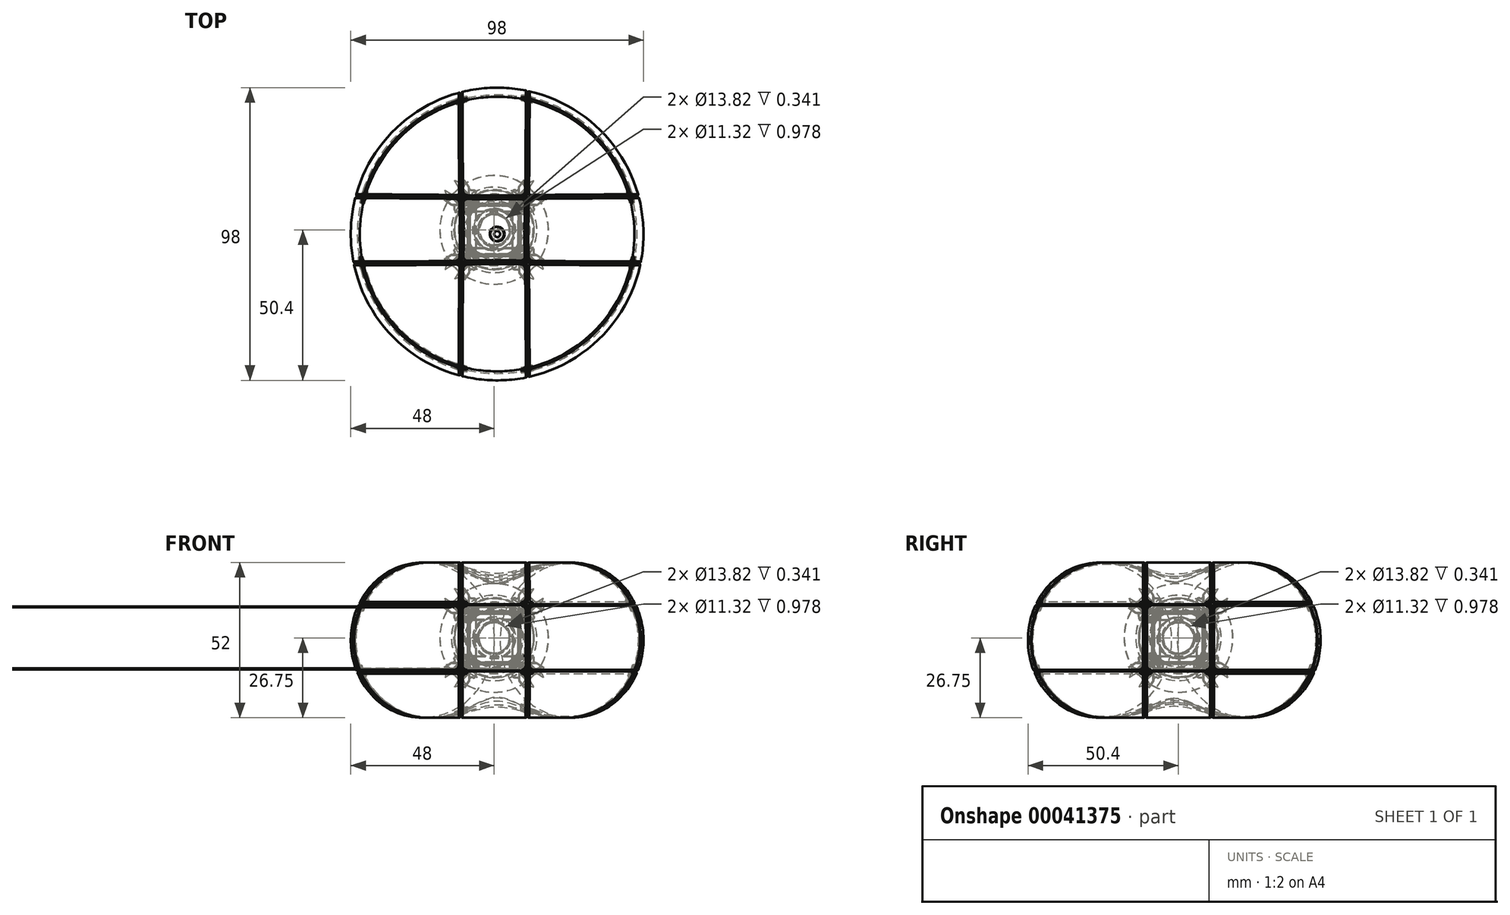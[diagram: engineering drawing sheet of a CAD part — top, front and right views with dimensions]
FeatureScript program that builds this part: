
annotation { "Feature Type Name" : "Feature", "Feature Type Description" : "" }
export const myFeature = defineFeature(function(context is Context, id is Id, definition is map)
    precondition{}
    {
        {
            var Q0;
            Q0=qCreatedBy(makeId("Front.planeOp"),FACE);
            cPlane(context, id + "F0", {"entities" : qUnion([Q0]), "cplaneType" : CPlaneType.OFFSET, "offset" : 1.4 * mm, "width" : 150 * mm, "height" : 150 * mm});
        }
        {
            var Q0;
            Q0=qCreatedBy(id+"F0.planeOp",FACE);
            var sketch = newSketch(context, id + "F1", { "sketchPlane" : qUnion([Q0])});
            skLineSegment(sketch, "E0", {"start": v(1, 6.41) * mm, "end": v(1, -8.32) * mm, "construction": true});
            skLineSegment(sketch, "E1", {"start": v(1, -0.75) * mm, "end": v(26, -0.75) * mm});
            skCircle(sketch, "E2", {"center": v(26, -0.75) * mm, "radius": 24 * mm});
            skEllipse(sketch, "E3", {"center": v(26, -0.75) * mm, "majorRadius": 26 * mm, "minorRadius": 24 * mm, "majorAxis": v(0, 1)});
            skSolve(sketch);
        }
        {
            var Q0;
            {var subQ0=sQuery(id+"F1.wireOp",EDGE,"E3");var subQ1=sQuery(id+"F1.wireOp",EDGE,"E2");var subQ3=makeQuery(id+"F1.imprint","INTERSECT",VERTEX,{"disambiguationData":[OD(0.0)],"derivedFrom":[subQ1,subQ0]});Q0=makeQuery(id+"F1.imprint","IMPRINT",FACE,{"disambiguationData":[TD([[makeQuery(id+"F1.imprint","IMPRINT",EDGE,{"disambiguationData":[TD([[subQ3,1.0]])],"derivedFrom":subQ1}),-1.0]])]});}
            var Q1;
            {var subQ0=sQuery(id+"F1.wireOp",EDGE,"E2");var subQ1=sQuery(id+"F1.wireOp",EDGE,"E3");var subQ3=makeQuery(id+"F1.imprint","INTERSECT",VERTEX,{"disambiguationData":[OD(0.0)],"derivedFrom":[subQ0,subQ1]});Q1=makeQuery(id+"F1.imprint","IMPRINT",FACE,{"disambiguationData":[TD([[makeQuery(id+"F1.imprint","IMPRINT",EDGE,{"disambiguationData":[TD([[subQ3,1.0]])],"derivedFrom":subQ0}),1.0]])]});}
            var Q2;
            {var subQ0=sQuery(id+"F1.wireOp",EDGE,"E3");var subQ1=sQuery(id+"F1.wireOp",EDGE,"E2");var subQ3=makeQuery(id+"F1.imprint","INTERSECT",VERTEX,{"disambiguationData":[OD(0.0)],"derivedFrom":[subQ1,subQ0]});Q2=makeQuery(id+"F1.imprint","IMPRINT",FACE,{"disambiguationData":[TD([[makeQuery(id+"F1.imprint","IMPRINT",EDGE,{"disambiguationData":[TD([[subQ3,-1.0]])],"derivedFrom":subQ1}),-1.0]])]});}
            var Q3;
            Q3=sQuery(id+"F1.wireOp",EDGE,"E0");
            revolve(context, id + "F2", {"entities" : qUnion([Q0, Q1, Q2]), "axis" : qUnion([Q3]), "revolveType" : RevolveType.FULL});
        }
        {
            var Q0;
            Q0=qCreatedBy(makeId("Front.planeOp"),FACE);
            var sketch = newSketch(context, id + "F3", { "sketchPlane" : qUnion([Q0])});
            skLineSegment(sketch, "E4", {"start": v(6, 60.75) * mm, "end": v(6.25, 60.75) * mm});
            skLineSegment(sketch, "E5.bottom", {"start": v(0, 0) * mm, "end": v(20, 0) * mm, "construction": true});
            skLineSegment(sketch, "E5.top", {"start": v(0, 20) * mm, "end": v(20, 20) * mm, "construction": true});
            skLineSegment(sketch, "E5.left", {"start": v(0, 0) * mm, "end": v(0, 20) * mm, "construction": true});
            skLineSegment(sketch, "E5.right", {"start": v(20, 0) * mm, "end": v(20, 20) * mm, "construction": true});
            skLineSegment(sketch, "E6", {"start": v(0, 0) * mm, "end": v(20, 20) * mm, "construction": true});
            skLineSegment(sketch, "E7.top", {"start": v(0, 28.28) * mm, "end": v(20, 28.28) * mm, "construction": true});
            skLineSegment(sketch, "E7.left", {"start": v(0, 0) * mm, "end": v(0, 28.28) * mm, "construction": true});
            skLineSegment(sketch, "E7.right", {"start": v(20, 0) * mm, "end": v(20, 28.28) * mm, "construction": true});
            skLineSegment(sketch, "E8", {"start": v(0, 0) * mm, "end": v(20, 28.28) * mm, "construction": true});
            skLineSegment(sketch, "E9.0", {"start": v(8.25, 14.07) * mm, "end": v(8.25, 14.34) * mm});
            skCircle(sketch, "E10", {"center": v(25, 0) * mm, "radius": 24 * mm, "construction": true});
            skEllipse(sketch, "E11", {"center": v(25, 0) * mm, "majorRadius": 25 * mm, "minorRadius": 24 * mm, "majorAxis": v(0, -1), "construction": true});
            skArc(sketch, "E12", {"start": v(7.21, 13.38) * mm, "mid": v(7.92, 13.44) * mm, "end": v(8.25, 14.07) * mm});
            skArc(sketch, "E13", {"start": v(7.21, 13.38) * mm, "mid": v(6.39, 13.3) * mm, "end": v(6, 12.57) * mm});
            skLineSegment(sketch, "E14", {"start": v(8.25, 14.07) * mm, "end": v(8.25, 14.07) * mm});
            skLineSegment(sketch, "E15", {"start": v(6, 11.54) * mm, "end": v(6, 12.57) * mm});
            skLineSegment(sketch, "E16.0", {"start": v(8.5, 14.07) * mm, "end": v(8.5, 14.26) * mm});
            skLineSegment(sketch, "E16.1", {"start": v(8.5, 14.07) * mm, "end": v(8.5, 14.07) * mm});
            skLineSegment(sketch, "E16.3", {"start": v(6.25, 12) * mm, "end": v(6.25, 12.57) * mm});
            skArc(sketch, "E16.4", {"start": v(7.12, 13.15) * mm, "mid": v(6.53, 13.09) * mm, "end": v(6.25, 12.57) * mm});
            skArc(sketch, "E16.5", {"start": v(7.12, 13.15) * mm, "mid": v(8.05, 13.24) * mm, "end": v(8.5, 14.07) * mm});
            skLineSegment(sketch, "E17", {"start": v(8.25, 14.34) * mm, "end": v(11, 18.23) * mm});
            skLineSegment(sketch, "E18", {"start": v(11, 18.23) * mm, "end": v(11, 58.23) * mm});
            skLineSegment(sketch, "E19.0", {"start": v(11.25, 18.15) * mm, "end": v(11.25, 58.23) * mm});
            skLineSegment(sketch, "E19.1", {"start": v(8.5, 14.26) * mm, "end": v(11.25, 18.15) * mm});
            skLineSegment(sketch, "E20", {"start": v(11, 58.23) * mm, "end": v(11.25, 58.23) * mm});
            skLineSegment(sketch, "E21", {"start": v(0, 8) * mm, "end": v(11.08, 8) * mm, "construction": true});
            skLineSegment(sketch, "E22", {"start": v(8, 6.66) * mm, "end": v(8.98, 6.66) * mm});
            skLineSegment(sketch, "E23", {"start": v(8.98, 5.66) * mm, "end": v(8, 5.66) * mm});
            skLineSegment(sketch, "E24.1", {"start": v(8.43, 6.9) * mm, "end": v(8.77, 6.9) * mm});
            skLineSegment(sketch, "E25", {"start": v(9.5, 6.67) * mm, "end": v(9.5, 5.65) * mm});
            skArc(sketch, "E26", {"start": v(8.98, 5.66) * mm, "mid": v(10.22, 6.16) * mm, "end": v(8.98, 6.66) * mm});
            skArc(sketch, "E27", {"start": v(8.77, 5.4) * mm, "mid": v(10.55, 6.16) * mm, "end": v(8.77, 6.9) * mm});
            skLineSegment(sketch, "E28.trimOffspring", {"start": v(8.77, 5.4) * mm, "end": v(8.25, 5.4) * mm});
            skLineSegment(sketch, "E29", {"start": v(9.5, 6.16) * mm, "end": v(8.75, 6.16) * mm});
            skLineSegment(sketch, "E30", {"start": v(8.77, 5.4) * mm, "end": v(8.77, 6.9) * mm, "construction": true});
            skLineSegment(sketch, "E31", {"start": v(8, 6.66) * mm, "end": v(8, 9.54) * mm});
            skLineSegment(sketch, "E32", {"start": v(8, 5.66) * mm, "end": v(8, 0) * mm});
            skLineSegment(sketch, "E33", {"start": v(8, 0) * mm, "end": v(8.25, 0) * mm});
            skLineSegment(sketch, "E34", {"start": v(8.25, 0) * mm, "end": v(8.25, 5.4) * mm});
            skLineSegment(sketch, "E35", {"start": v(6, 11.54) * mm, "end": v(8, 9.54) * mm});
            skLineSegment(sketch, "E36.0", {"start": v(6.25, 12) * mm, "end": v(8.43, 9.82) * mm});
            skLineSegment(sketch, "E37.trimOffspring", {"start": v(8.43, 9.82) * mm, "end": v(8.43, 6.9) * mm});
            skSolve(sketch);
        }
        {
            var Q0;
            Q0=makeQuery(id+"F3.imprint","IMPRINT",FACE,{"disambiguationData":[TD([[makeQuery(id+"F3.imprint","IMPRINT",EDGE,{"derivedFrom":sQuery(id+"F3.wireOp",EDGE,"E9.0")}),-1.0]])]});
            var Q1;
            Q1=sQuery(id+"F3.wireOp",EDGE,"E33");
            revolve(context, id + "F4", {"entities" : qUnion([Q0]), "axis" : qUnion([Q1]), "revolveType" : RevolveType.FULL, "oppositeDirection" : true});
        }
        {
            var Q0;
            Q0=makeQuery(id+"F4.opRevolve","SWEPT_BODY",BODY,{"disambiguationData":[OSD([sQuery(id+"F3.wireOp",EDGE,"e49f9d83-1361-4242-9c47-cf3f22957d33"),sQuery(id+"F3.wireOp",EDGE,"8730d663-9635-4a8c-ab1e-4514442db75a"),sQuery(id+"F3.wireOp",EDGE,"964f677f-81cd-4849-92fc-20bc6bd24689"),sQuery(id+"F3.wireOp",EDGE,"5875af96-867b-470c-aa94-be0c1ef376cd"),sQuery(id+"F3.wireOp",EDGE,"1ed69cf5-0fa4-4409-b8ec-72a7ec0a6539.trimOffspring"),sQuery(id+"F3.wireOp",EDGE,"80e836a5-1244-4908-9c79-18195465c5bf.0"),sQuery(id+"F3.wireOp",EDGE,"80e836a5-1244-4908-9c79-18195465c5bf.1"),sQuery(id+"F3.wireOp",EDGE,"80e836a5-1244-4908-9c79-18195465c5bf.2"),sQuery(id+"F3.wireOp",EDGE,"80e836a5-1244-4908-9c79-18195465c5bf.3"),sQuery(id+"F3.wireOp",EDGE,"80e836a5-1244-4908-9c79-18195465c5bf.4"),sQuery(id+"F3.wireOp",EDGE,"E4"),sQuery(id+"F3.wireOp",EDGE,"951da4eb-9f43-4ae5-b708-2bc6142b5415")])]});
            var Q1;
            Q1=makeQuery(id+"F4.opRevolve","SWEPT_BODY",BODY,{"disambiguationData":[OSD([sQuery(id+"F3.wireOp",EDGE,"E9.0"),sQuery(id+"F3.wireOp",EDGE,"E9.2"),sQuery(id+"F3.wireOp",EDGE,"E12"),sQuery(id+"F3.wireOp",EDGE,"E13"),sQuery(id+"F3.wireOp",EDGE,"E14"),sQuery(id+"F3.wireOp",EDGE,"E15"),sQuery(id+"F3.wireOp",EDGE,"E16.0"),sQuery(id+"F3.wireOp",EDGE,"E16.1"),sQuery(id+"F3.wireOp",EDGE,"E16.2"),sQuery(id+"F3.wireOp",EDGE,"E16.3"),sQuery(id+"F3.wireOp",EDGE,"E16.4"),sQuery(id+"F3.wireOp",EDGE,"E16.5"),sQuery(id+"F3.wireOp",EDGE,"49baa046-a65a-4210-b3a2-b618f89a0829"),sQuery(id+"F3.wireOp",EDGE,"98141963-c407-4e79-8dff-f83a4dca13c9")])]});
            var Q2;
            Q2=qCreatedBy(makeId("Right.planeOp"),FACE);
            mirror(context, id + "F5", {"entities" : qUnion([Q0, Q1]), "mirrorPlane" : qUnion([Q2])});
        }
        {
            var Q0;
            Q0=qCreatedBy(makeId("Right.planeOp"),FACE);
            var Q1;
            Q1=qCreatedBy(makeId("Front.planeOp"),FACE);
            cPlane(context, id + "F6", {"entities" : qUnion([Q0, Q1]), "cplaneType" : CPlaneType.MID_PLANE, "offset" : 150 * mm, "width" : 150 * mm, "height" : 150 * mm});
        }
        {
            var Q0;
            Q0=qCreatedBy(id+"F6.planeOp",FACE);
            var sketch = newSketch(context, id + "F7", { "sketchPlane" : qUnion([Q0])});
            skLineSegment(sketch, "E38.bottom", {"start": v(0, 0) * mm, "end": v(-70.71, 0) * mm, "construction": true});
            skLineSegment(sketch, "E38.top", {"start": v(0, 50) * mm, "end": v(-70.71, 50) * mm, "construction": true});
            skLineSegment(sketch, "E38.left", {"start": v(0, 0) * mm, "end": v(0, 50) * mm, "construction": true});
            skLineSegment(sketch, "E38.right", {"start": v(-70.71, 0) * mm, "end": v(-70.71, 50) * mm, "construction": true});
            skLineSegment(sketch, "E39", {"start": v(0, 0) * mm, "end": v(-70.71, 50) * mm});
            skSolve(sketch);
        }
        {
            var Q0;
            Q0=makeQuery(id+"F5.opPattern","COPY",BODY,{"derivedFrom":makeQuery(id+"F4.opRevolve","SWEPT_BODY",BODY,{"disambiguationData":[OSD([sQuery(id+"F3.wireOp",EDGE,"e49f9d83-1361-4242-9c47-cf3f22957d33"),sQuery(id+"F3.wireOp",EDGE,"8730d663-9635-4a8c-ab1e-4514442db75a"),sQuery(id+"F3.wireOp",EDGE,"964f677f-81cd-4849-92fc-20bc6bd24689"),sQuery(id+"F3.wireOp",EDGE,"5875af96-867b-470c-aa94-be0c1ef376cd"),sQuery(id+"F3.wireOp",EDGE,"1ed69cf5-0fa4-4409-b8ec-72a7ec0a6539.trimOffspring"),sQuery(id+"F3.wireOp",EDGE,"80e836a5-1244-4908-9c79-18195465c5bf.0"),sQuery(id+"F3.wireOp",EDGE,"80e836a5-1244-4908-9c79-18195465c5bf.1"),sQuery(id+"F3.wireOp",EDGE,"80e836a5-1244-4908-9c79-18195465c5bf.2"),sQuery(id+"F3.wireOp",EDGE,"80e836a5-1244-4908-9c79-18195465c5bf.3"),sQuery(id+"F3.wireOp",EDGE,"80e836a5-1244-4908-9c79-18195465c5bf.4"),sQuery(id+"F3.wireOp",EDGE,"E4"),sQuery(id+"F3.wireOp",EDGE,"951da4eb-9f43-4ae5-b708-2bc6142b5415")])]}),"instanceName":"1"});
            var Q1;
            Q1=makeQuery(id+"F4.opRevolve","SWEPT_BODY",BODY,{"disambiguationData":[OSD([sQuery(id+"F3.wireOp",EDGE,"e49f9d83-1361-4242-9c47-cf3f22957d33"),sQuery(id+"F3.wireOp",EDGE,"8730d663-9635-4a8c-ab1e-4514442db75a"),sQuery(id+"F3.wireOp",EDGE,"964f677f-81cd-4849-92fc-20bc6bd24689"),sQuery(id+"F3.wireOp",EDGE,"5875af96-867b-470c-aa94-be0c1ef376cd"),sQuery(id+"F3.wireOp",EDGE,"1ed69cf5-0fa4-4409-b8ec-72a7ec0a6539.trimOffspring"),sQuery(id+"F3.wireOp",EDGE,"80e836a5-1244-4908-9c79-18195465c5bf.0"),sQuery(id+"F3.wireOp",EDGE,"80e836a5-1244-4908-9c79-18195465c5bf.1"),sQuery(id+"F3.wireOp",EDGE,"80e836a5-1244-4908-9c79-18195465c5bf.2"),sQuery(id+"F3.wireOp",EDGE,"80e836a5-1244-4908-9c79-18195465c5bf.3"),sQuery(id+"F3.wireOp",EDGE,"80e836a5-1244-4908-9c79-18195465c5bf.4"),sQuery(id+"F3.wireOp",EDGE,"E4"),sQuery(id+"F3.wireOp",EDGE,"951da4eb-9f43-4ae5-b708-2bc6142b5415")])]});
            var Q2;
            Q2=makeQuery(id+"F5.opPattern","COPY",BODY,{"derivedFrom":makeQuery(id+"F4.opRevolve","SWEPT_BODY",BODY,{"disambiguationData":[OSD([sQuery(id+"F3.wireOp",EDGE,"E9.0"),sQuery(id+"F3.wireOp",EDGE,"E9.2"),sQuery(id+"F3.wireOp",EDGE,"E12"),sQuery(id+"F3.wireOp",EDGE,"E13"),sQuery(id+"F3.wireOp",EDGE,"E14"),sQuery(id+"F3.wireOp",EDGE,"E15"),sQuery(id+"F3.wireOp",EDGE,"E16.0"),sQuery(id+"F3.wireOp",EDGE,"E16.1"),sQuery(id+"F3.wireOp",EDGE,"E16.2"),sQuery(id+"F3.wireOp",EDGE,"E16.3"),sQuery(id+"F3.wireOp",EDGE,"E16.4"),sQuery(id+"F3.wireOp",EDGE,"E16.5"),sQuery(id+"F3.wireOp",EDGE,"49baa046-a65a-4210-b3a2-b618f89a0829"),sQuery(id+"F3.wireOp",EDGE,"98141963-c407-4e79-8dff-f83a4dca13c9")])]}),"instanceName":"1"});
            var Q3;
            Q3=makeQuery(id+"F4.opRevolve","SWEPT_BODY",BODY,{"disambiguationData":[OSD([sQuery(id+"F3.wireOp",EDGE,"E9.0"),sQuery(id+"F3.wireOp",EDGE,"E9.2"),sQuery(id+"F3.wireOp",EDGE,"E12"),sQuery(id+"F3.wireOp",EDGE,"E13"),sQuery(id+"F3.wireOp",EDGE,"E14"),sQuery(id+"F3.wireOp",EDGE,"E15"),sQuery(id+"F3.wireOp",EDGE,"E16.0"),sQuery(id+"F3.wireOp",EDGE,"E16.1"),sQuery(id+"F3.wireOp",EDGE,"E16.2"),sQuery(id+"F3.wireOp",EDGE,"E16.3"),sQuery(id+"F3.wireOp",EDGE,"E16.4"),sQuery(id+"F3.wireOp",EDGE,"E16.5"),sQuery(id+"F3.wireOp",EDGE,"49baa046-a65a-4210-b3a2-b618f89a0829"),sQuery(id+"F3.wireOp",EDGE,"98141963-c407-4e79-8dff-f83a4dca13c9")])]});
            var Q4;
            Q4=sQuery(id+"F7.wireOp",EDGE,"E39");
            circularPattern(context, id + "F8", {"entities" : qUnion([Q0, Q1, Q2, Q3]), "axis" : qUnion([Q4]), "angle" : 360 * degree, "instanceCount" : 3, "equalSpace" : true});
        }
        {
            var Q0;
            Q0=makeQuery(id+"F4.opRevolve","SWEPT_BODY",BODY,{"disambiguationData":[OSD([sQuery(id+"F3.wireOp",EDGE,"E9.0"),sQuery(id+"F3.wireOp",EDGE,"E9.2"),sQuery(id+"F3.wireOp",EDGE,"E12"),sQuery(id+"F3.wireOp",EDGE,"E13"),sQuery(id+"F3.wireOp",EDGE,"E14"),sQuery(id+"F3.wireOp",EDGE,"E15"),sQuery(id+"F3.wireOp",EDGE,"E16.0"),sQuery(id+"F3.wireOp",EDGE,"E16.1"),sQuery(id+"F3.wireOp",EDGE,"E16.2"),sQuery(id+"F3.wireOp",EDGE,"E16.3"),sQuery(id+"F3.wireOp",EDGE,"E16.4"),sQuery(id+"F3.wireOp",EDGE,"E16.5"),sQuery(id+"F3.wireOp",EDGE,"49baa046-a65a-4210-b3a2-b618f89a0829"),sQuery(id+"F3.wireOp",EDGE,"98141963-c407-4e79-8dff-f83a4dca13c9")])]});
            var Q1;
            Q1=makeQuery(id+"F5.opPattern","COPY",BODY,{"derivedFrom":makeQuery(id+"F4.opRevolve","SWEPT_BODY",BODY,{"disambiguationData":[OSD([sQuery(id+"F3.wireOp",EDGE,"E9.0"),sQuery(id+"F3.wireOp",EDGE,"E9.2"),sQuery(id+"F3.wireOp",EDGE,"E12"),sQuery(id+"F3.wireOp",EDGE,"E13"),sQuery(id+"F3.wireOp",EDGE,"E14"),sQuery(id+"F3.wireOp",EDGE,"E15"),sQuery(id+"F3.wireOp",EDGE,"E16.0"),sQuery(id+"F3.wireOp",EDGE,"E16.1"),sQuery(id+"F3.wireOp",EDGE,"E16.2"),sQuery(id+"F3.wireOp",EDGE,"E16.3"),sQuery(id+"F3.wireOp",EDGE,"E16.4"),sQuery(id+"F3.wireOp",EDGE,"E16.5"),sQuery(id+"F3.wireOp",EDGE,"49baa046-a65a-4210-b3a2-b618f89a0829"),sQuery(id+"F3.wireOp",EDGE,"98141963-c407-4e79-8dff-f83a4dca13c9")])]}),"instanceName":"1"});
            var Q2;
            Q2=makeQuery(id+"F8.opPattern","COPY",BODY,{"derivedFrom":makeQuery(id+"F4.opRevolve","SWEPT_BODY",BODY,{"disambiguationData":[OSD([sQuery(id+"F3.wireOp",EDGE,"E9.0"),sQuery(id+"F3.wireOp",EDGE,"E9.2"),sQuery(id+"F3.wireOp",EDGE,"E12"),sQuery(id+"F3.wireOp",EDGE,"E13"),sQuery(id+"F3.wireOp",EDGE,"E14"),sQuery(id+"F3.wireOp",EDGE,"E15"),sQuery(id+"F3.wireOp",EDGE,"E16.0"),sQuery(id+"F3.wireOp",EDGE,"E16.1"),sQuery(id+"F3.wireOp",EDGE,"E16.2"),sQuery(id+"F3.wireOp",EDGE,"E16.3"),sQuery(id+"F3.wireOp",EDGE,"E16.4"),sQuery(id+"F3.wireOp",EDGE,"E16.5"),sQuery(id+"F3.wireOp",EDGE,"49baa046-a65a-4210-b3a2-b618f89a0829"),sQuery(id+"F3.wireOp",EDGE,"98141963-c407-4e79-8dff-f83a4dca13c9")])]}),"instanceName":"2"});
            var Q3;
            Q3=makeQuery(id+"F8.opPattern","COPY",BODY,{"derivedFrom":makeQuery(id+"F5.opPattern","COPY",BODY,{"derivedFrom":makeQuery(id+"F4.opRevolve","SWEPT_BODY",BODY,{"disambiguationData":[OSD([sQuery(id+"F3.wireOp",EDGE,"E9.0"),sQuery(id+"F3.wireOp",EDGE,"E9.2"),sQuery(id+"F3.wireOp",EDGE,"E12"),sQuery(id+"F3.wireOp",EDGE,"E13"),sQuery(id+"F3.wireOp",EDGE,"E14"),sQuery(id+"F3.wireOp",EDGE,"E15"),sQuery(id+"F3.wireOp",EDGE,"E16.0"),sQuery(id+"F3.wireOp",EDGE,"E16.1"),sQuery(id+"F3.wireOp",EDGE,"E16.2"),sQuery(id+"F3.wireOp",EDGE,"E16.3"),sQuery(id+"F3.wireOp",EDGE,"E16.4"),sQuery(id+"F3.wireOp",EDGE,"E16.5"),sQuery(id+"F3.wireOp",EDGE,"49baa046-a65a-4210-b3a2-b618f89a0829"),sQuery(id+"F3.wireOp",EDGE,"98141963-c407-4e79-8dff-f83a4dca13c9")])]}),"instanceName":"1"}),"instanceName":"2"});
            var Q4;
            Q4=makeQuery(id+"F8.opPattern","COPY",BODY,{"derivedFrom":makeQuery(id+"F4.opRevolve","SWEPT_BODY",BODY,{"disambiguationData":[OSD([sQuery(id+"F3.wireOp",EDGE,"E9.0"),sQuery(id+"F3.wireOp",EDGE,"E9.2"),sQuery(id+"F3.wireOp",EDGE,"E12"),sQuery(id+"F3.wireOp",EDGE,"E13"),sQuery(id+"F3.wireOp",EDGE,"E14"),sQuery(id+"F3.wireOp",EDGE,"E15"),sQuery(id+"F3.wireOp",EDGE,"E16.0"),sQuery(id+"F3.wireOp",EDGE,"E16.1"),sQuery(id+"F3.wireOp",EDGE,"E16.2"),sQuery(id+"F3.wireOp",EDGE,"E16.3"),sQuery(id+"F3.wireOp",EDGE,"E16.4"),sQuery(id+"F3.wireOp",EDGE,"E16.5"),sQuery(id+"F3.wireOp",EDGE,"49baa046-a65a-4210-b3a2-b618f89a0829"),sQuery(id+"F3.wireOp",EDGE,"98141963-c407-4e79-8dff-f83a4dca13c9")])]}),"instanceName":"1"});
            var Q5;
            Q5=makeQuery(id+"F8.opPattern","COPY",BODY,{"derivedFrom":makeQuery(id+"F5.opPattern","COPY",BODY,{"derivedFrom":makeQuery(id+"F4.opRevolve","SWEPT_BODY",BODY,{"disambiguationData":[OSD([sQuery(id+"F3.wireOp",EDGE,"E9.0"),sQuery(id+"F3.wireOp",EDGE,"E9.2"),sQuery(id+"F3.wireOp",EDGE,"E12"),sQuery(id+"F3.wireOp",EDGE,"E13"),sQuery(id+"F3.wireOp",EDGE,"E14"),sQuery(id+"F3.wireOp",EDGE,"E15"),sQuery(id+"F3.wireOp",EDGE,"E16.0"),sQuery(id+"F3.wireOp",EDGE,"E16.1"),sQuery(id+"F3.wireOp",EDGE,"E16.2"),sQuery(id+"F3.wireOp",EDGE,"E16.3"),sQuery(id+"F3.wireOp",EDGE,"E16.4"),sQuery(id+"F3.wireOp",EDGE,"E16.5"),sQuery(id+"F3.wireOp",EDGE,"49baa046-a65a-4210-b3a2-b618f89a0829"),sQuery(id+"F3.wireOp",EDGE,"98141963-c407-4e79-8dff-f83a4dca13c9")])]}),"instanceName":"1"}),"instanceName":"1"});
            booleanBodies(context, id + "F9", {"operationType" : BooleanOperationType.UNION, "tools" : qUnion([Q0, Q1, Q2, Q3, Q4, Q5])});
        }
        {
            var Q0;
            Q0=makeQuery(id+"F4.opRevolve","SWEPT_BODY",BODY,{"disambiguationData":[OSD([sQuery(id+"F3.wireOp",EDGE,"E9.0"),sQuery(id+"F3.wireOp",EDGE,"E9.2"),sQuery(id+"F3.wireOp",EDGE,"E12"),sQuery(id+"F3.wireOp",EDGE,"E13"),sQuery(id+"F3.wireOp",EDGE,"E14"),sQuery(id+"F3.wireOp",EDGE,"E15"),sQuery(id+"F3.wireOp",EDGE,"E16.0"),sQuery(id+"F3.wireOp",EDGE,"E16.1"),sQuery(id+"F3.wireOp",EDGE,"E16.2"),sQuery(id+"F3.wireOp",EDGE,"E16.3"),sQuery(id+"F3.wireOp",EDGE,"E16.4"),sQuery(id+"F3.wireOp",EDGE,"E16.5"),sQuery(id+"F3.wireOp",EDGE,"49baa046-a65a-4210-b3a2-b618f89a0829"),sQuery(id+"F3.wireOp",EDGE,"98141963-c407-4e79-8dff-f83a4dca13c9")])]});
            var Q1;
            Q1=makeQuery(id+"F2.opRevolve","SWEPT_BODY",BODY,{"disambiguationData":[OSD([sQuery(id+"F1.wireOp",EDGE,"E2")])]});
            var Q2;
            Q2=makeQuery(id+"F2.opRevolve","SWEPT_BODY",BODY,{"disambiguationData":[OSD([sQuery(id+"F1.wireOp",EDGE,"E3")])]});
            booleanBodies(context, id + "F10", {"operationType" : BooleanOperationType.SUBTRACTION, "tools" : qUnion([Q0]), "targets" : qUnion([Q1, Q2])});
        }
        {
            var Q0;
            {var subQ0=makeQuery(id+"F4.opRevolve","SWEPT_FACE",FACE,{"disambiguationData":[OSD([sQuery(id+"F3.wireOp",EDGE,"E18")])]});Q0=makeQuery(id+"F10.opBoolean","COPY",EDGE,{"derivedFrom":makeQuery(id+"F9.opBoolean","INTERSECT",EDGE,{"disambiguationData":[OD(0.0)],"derivedFrom":[subQ0,makeQuery(id+"F8.opPattern","COPY",FACE,{"derivedFrom":subQ0,"instanceName":"2"})]})});}
            var Q1;
            {var subQ0=makeQuery(id+"F4.opRevolve","SWEPT_FACE",FACE,{"disambiguationData":[OSD([sQuery(id+"F3.wireOp",EDGE,"E18")])]});Q1=makeQuery(id+"F10.opBoolean","COPY",EDGE,{"derivedFrom":makeQuery(id+"F9.opBoolean","INTERSECT",EDGE,{"disambiguationData":[OD(0.0)],"derivedFrom":[makeQuery(id+"F5.opPattern","COPY",FACE,{"derivedFrom":subQ0,"instanceName":"1"}),makeQuery(id+"F8.opPattern","COPY",FACE,{"derivedFrom":subQ0,"instanceName":"2"})]})});}
            var Q2;
            {var subQ0=makeQuery(id+"F4.opRevolve","SWEPT_FACE",FACE,{"disambiguationData":[OSD([sQuery(id+"F3.wireOp",EDGE,"E18")])]});Q2=makeQuery(id+"F10.opBoolean","COPY",EDGE,{"derivedFrom":makeQuery(id+"F9.opBoolean","INTERSECT",EDGE,{"disambiguationData":[OD(0.0)],"derivedFrom":[subQ0,makeQuery(id+"F8.opPattern","COPY",FACE,{"derivedFrom":makeQuery(id+"F5.opPattern","COPY",FACE,{"derivedFrom":subQ0,"instanceName":"1"}),"instanceName":"2"})]})});}
            var Q3;
            {var subQ0=makeQuery(id+"F5.opPattern","COPY",FACE,{"derivedFrom":makeQuery(id+"F4.opRevolve","SWEPT_FACE",FACE,{"disambiguationData":[OSD([sQuery(id+"F3.wireOp",EDGE,"E18")])]}),"instanceName":"1"});Q3=makeQuery(id+"F10.opBoolean","COPY",EDGE,{"derivedFrom":makeQuery(id+"F9.opBoolean","INTERSECT",EDGE,{"disambiguationData":[OD(0.0)],"derivedFrom":[subQ0,makeQuery(id+"F8.opPattern","COPY",FACE,{"derivedFrom":subQ0,"instanceName":"2"})]})});}
            var Q4;
            {var subQ0=makeQuery(id+"F4.opRevolve","SWEPT_FACE",FACE,{"disambiguationData":[OSD([sQuery(id+"F3.wireOp",EDGE,"E18")])]});Q4=makeQuery(id+"F10.opBoolean","COPY",EDGE,{"derivedFrom":makeQuery(id+"F9.opBoolean","INTERSECT",EDGE,{"disambiguationData":[OD(1.0)],"derivedFrom":[makeQuery(id+"F8.opPattern","COPY",FACE,{"derivedFrom":makeQuery(id+"F5.opPattern","COPY",FACE,{"derivedFrom":subQ0,"instanceName":"1"}),"instanceName":"1"}),makeQuery(id+"F8.opPattern","COPY",FACE,{"derivedFrom":subQ0,"instanceName":"2"})]})});}
            var Q5;
            {var subQ0=makeQuery(id+"F4.opRevolve","SWEPT_FACE",FACE,{"disambiguationData":[OSD([sQuery(id+"F3.wireOp",EDGE,"E18")])]});Q5=makeQuery(id+"F10.opBoolean","COPY",EDGE,{"derivedFrom":makeQuery(id+"F9.opBoolean","INTERSECT",EDGE,{"disambiguationData":[OD(1.0)],"derivedFrom":[makeQuery(id+"F8.opPattern","COPY",FACE,{"derivedFrom":subQ0,"instanceName":"1"}),makeQuery(id+"F8.opPattern","COPY",FACE,{"derivedFrom":subQ0,"instanceName":"2"})]})});}
            var Q6;
            {var subQ0=makeQuery(id+"F4.opRevolve","SWEPT_FACE",FACE,{"disambiguationData":[OSD([sQuery(id+"F3.wireOp",EDGE,"E18")])]});Q6=makeQuery(id+"F10.opBoolean","COPY",EDGE,{"derivedFrom":makeQuery(id+"F9.opBoolean","INTERSECT",EDGE,{"disambiguationData":[OD(1.0)],"derivedFrom":[makeQuery(id+"F8.opPattern","COPY",FACE,{"derivedFrom":subQ0,"instanceName":"1"}),makeQuery(id+"F8.opPattern","COPY",FACE,{"derivedFrom":makeQuery(id+"F5.opPattern","COPY",FACE,{"derivedFrom":subQ0,"instanceName":"1"}),"instanceName":"2"})]})});}
            var Q7;
            {var subQ0=makeQuery(id+"F5.opPattern","COPY",FACE,{"derivedFrom":makeQuery(id+"F4.opRevolve","SWEPT_FACE",FACE,{"disambiguationData":[OSD([sQuery(id+"F3.wireOp",EDGE,"E18")])]}),"instanceName":"1"});Q7=makeQuery(id+"F10.opBoolean","COPY",EDGE,{"derivedFrom":makeQuery(id+"F9.opBoolean","INTERSECT",EDGE,{"disambiguationData":[OD(1.0)],"derivedFrom":[makeQuery(id+"F8.opPattern","COPY",FACE,{"derivedFrom":subQ0,"instanceName":"1"}),makeQuery(id+"F8.opPattern","COPY",FACE,{"derivedFrom":subQ0,"instanceName":"2"})]})});}
            var Q8;
            {var subQ0=makeQuery(id+"F4.opRevolve","SWEPT_FACE",FACE,{"disambiguationData":[OSD([sQuery(id+"F3.wireOp",EDGE,"E18")])]});Q8=makeQuery(id+"F10.opBoolean","COPY",EDGE,{"derivedFrom":makeQuery(id+"F9.opBoolean","INTERSECT",EDGE,{"disambiguationData":[OD(1.0)],"derivedFrom":[subQ0,makeQuery(id+"F8.opPattern","COPY",FACE,{"derivedFrom":makeQuery(id+"F5.opPattern","COPY",FACE,{"derivedFrom":subQ0,"instanceName":"1"}),"instanceName":"1"})]})});}
            var Q9;
            {var subQ0=makeQuery(id+"F5.opPattern","COPY",FACE,{"derivedFrom":makeQuery(id+"F4.opRevolve","SWEPT_FACE",FACE,{"disambiguationData":[OSD([sQuery(id+"F3.wireOp",EDGE,"E18")])]}),"instanceName":"1"});Q9=makeQuery(id+"F10.opBoolean","COPY",EDGE,{"derivedFrom":makeQuery(id+"F9.opBoolean","INTERSECT",EDGE,{"disambiguationData":[OD(1.0)],"derivedFrom":[subQ0,makeQuery(id+"F8.opPattern","COPY",FACE,{"derivedFrom":subQ0,"instanceName":"1"})]})});}
            var Q10;
            {var subQ0=makeQuery(id+"F4.opRevolve","SWEPT_FACE",FACE,{"disambiguationData":[OSD([sQuery(id+"F3.wireOp",EDGE,"E18")])]});Q10=makeQuery(id+"F10.opBoolean","COPY",EDGE,{"derivedFrom":makeQuery(id+"F9.opBoolean","INTERSECT",EDGE,{"disambiguationData":[OD(1.0)],"derivedFrom":[subQ0,makeQuery(id+"F8.opPattern","COPY",FACE,{"derivedFrom":subQ0,"instanceName":"1"})]})});}
            var Q11;
            {var subQ0=makeQuery(id+"F4.opRevolve","SWEPT_FACE",FACE,{"disambiguationData":[OSD([sQuery(id+"F3.wireOp",EDGE,"E18")])]});Q11=makeQuery(id+"F10.opBoolean","COPY",EDGE,{"derivedFrom":makeQuery(id+"F9.opBoolean","INTERSECT",EDGE,{"disambiguationData":[OD(1.0)],"derivedFrom":[makeQuery(id+"F5.opPattern","COPY",FACE,{"derivedFrom":subQ0,"instanceName":"1"}),makeQuery(id+"F8.opPattern","COPY",FACE,{"derivedFrom":subQ0,"instanceName":"1"})]})});}
            var Q12;
            {var subQ0=makeQuery(id+"F4.opRevolve","SWEPT_FACE",FACE,{"disambiguationData":[OSD([sQuery(id+"F3.wireOp",EDGE,"E18")])]});Q12=makeQuery(id+"F10.opBoolean","COPY",EDGE,{"derivedFrom":makeQuery(id+"F9.opBoolean","INTERSECT",EDGE,{"disambiguationData":[OD(1.0)],"derivedFrom":[subQ0,makeQuery(id+"F8.opPattern","COPY",FACE,{"derivedFrom":subQ0,"instanceName":"2"})]})});}
            var Q13;
            {var subQ0=makeQuery(id+"F4.opRevolve","SWEPT_FACE",FACE,{"disambiguationData":[OSD([sQuery(id+"F3.wireOp",EDGE,"E18")])]});Q13=makeQuery(id+"F10.opBoolean","COPY",EDGE,{"derivedFrom":makeQuery(id+"F9.opBoolean","INTERSECT",EDGE,{"disambiguationData":[OD(1.0)],"derivedFrom":[subQ0,makeQuery(id+"F8.opPattern","COPY",FACE,{"derivedFrom":makeQuery(id+"F5.opPattern","COPY",FACE,{"derivedFrom":subQ0,"instanceName":"1"}),"instanceName":"2"})]})});}
            var Q14;
            {var subQ0=makeQuery(id+"F4.opRevolve","SWEPT_FACE",FACE,{"disambiguationData":[OSD([sQuery(id+"F3.wireOp",EDGE,"E18")])]});Q14=makeQuery(id+"F10.opBoolean","COPY",EDGE,{"derivedFrom":makeQuery(id+"F9.opBoolean","INTERSECT",EDGE,{"disambiguationData":[OD(1.0)],"derivedFrom":[makeQuery(id+"F5.opPattern","COPY",FACE,{"derivedFrom":subQ0,"instanceName":"1"}),makeQuery(id+"F8.opPattern","COPY",FACE,{"derivedFrom":subQ0,"instanceName":"2"})]})});}
            var Q15;
            {var subQ0=makeQuery(id+"F5.opPattern","COPY",FACE,{"derivedFrom":makeQuery(id+"F4.opRevolve","SWEPT_FACE",FACE,{"disambiguationData":[OSD([sQuery(id+"F3.wireOp",EDGE,"E18")])]}),"instanceName":"1"});Q15=makeQuery(id+"F10.opBoolean","COPY",EDGE,{"derivedFrom":makeQuery(id+"F9.opBoolean","INTERSECT",EDGE,{"disambiguationData":[OD(1.0)],"derivedFrom":[subQ0,makeQuery(id+"F8.opPattern","COPY",FACE,{"derivedFrom":subQ0,"instanceName":"2"})]})});}
            var Q16;
            {var subQ0=makeQuery(id+"F5.opPattern","COPY",FACE,{"derivedFrom":makeQuery(id+"F4.opRevolve","SWEPT_FACE",FACE,{"disambiguationData":[OSD([sQuery(id+"F3.wireOp",EDGE,"E18")])]}),"instanceName":"1"});Q16=makeQuery(id+"F10.opBoolean","COPY",EDGE,{"derivedFrom":makeQuery(id+"F9.opBoolean","INTERSECT",EDGE,{"disambiguationData":[OD(0.0)],"derivedFrom":[subQ0,makeQuery(id+"F8.opPattern","COPY",FACE,{"derivedFrom":subQ0,"instanceName":"1"})]})});}
            var Q17;
            {var subQ0=makeQuery(id+"F4.opRevolve","SWEPT_FACE",FACE,{"disambiguationData":[OSD([sQuery(id+"F3.wireOp",EDGE,"E18")])]});Q17=makeQuery(id+"F10.opBoolean","COPY",EDGE,{"derivedFrom":makeQuery(id+"F9.opBoolean","INTERSECT",EDGE,{"disambiguationData":[OD(0.0)],"derivedFrom":[subQ0,makeQuery(id+"F8.opPattern","COPY",FACE,{"derivedFrom":makeQuery(id+"F5.opPattern","COPY",FACE,{"derivedFrom":subQ0,"instanceName":"1"}),"instanceName":"1"})]})});}
            var Q18;
            {var subQ0=makeQuery(id+"F4.opRevolve","SWEPT_FACE",FACE,{"disambiguationData":[OSD([sQuery(id+"F3.wireOp",EDGE,"E18")])]});Q18=makeQuery(id+"F10.opBoolean","COPY",EDGE,{"derivedFrom":makeQuery(id+"F9.opBoolean","INTERSECT",EDGE,{"disambiguationData":[OD(0.0)],"derivedFrom":[makeQuery(id+"F5.opPattern","COPY",FACE,{"derivedFrom":subQ0,"instanceName":"1"}),makeQuery(id+"F8.opPattern","COPY",FACE,{"derivedFrom":subQ0,"instanceName":"1"})]})});}
            var Q19;
            {var subQ0=makeQuery(id+"F4.opRevolve","SWEPT_FACE",FACE,{"disambiguationData":[OSD([sQuery(id+"F3.wireOp",EDGE,"E18")])]});Q19=makeQuery(id+"F10.opBoolean","COPY",EDGE,{"derivedFrom":makeQuery(id+"F9.opBoolean","INTERSECT",EDGE,{"disambiguationData":[OD(0.0)],"derivedFrom":[subQ0,makeQuery(id+"F8.opPattern","COPY",FACE,{"derivedFrom":subQ0,"instanceName":"1"})]})});}
            var Q20;
            {var subQ0=makeQuery(id+"F4.opRevolve","SWEPT_FACE",FACE,{"disambiguationData":[OSD([sQuery(id+"F3.wireOp",EDGE,"E18")])]});Q20=makeQuery(id+"F10.opBoolean","COPY",EDGE,{"derivedFrom":makeQuery(id+"F9.opBoolean","INTERSECT",EDGE,{"disambiguationData":[OD(0.0)],"derivedFrom":[makeQuery(id+"F8.opPattern","COPY",FACE,{"derivedFrom":subQ0,"instanceName":"1"}),makeQuery(id+"F8.opPattern","COPY",FACE,{"derivedFrom":subQ0,"instanceName":"2"})]})});}
            var Q21;
            {var subQ0=makeQuery(id+"F4.opRevolve","SWEPT_FACE",FACE,{"disambiguationData":[OSD([sQuery(id+"F3.wireOp",EDGE,"E18")])]});Q21=makeQuery(id+"F10.opBoolean","COPY",EDGE,{"derivedFrom":makeQuery(id+"F9.opBoolean","INTERSECT",EDGE,{"disambiguationData":[OD(0.0)],"derivedFrom":[makeQuery(id+"F8.opPattern","COPY",FACE,{"derivedFrom":subQ0,"instanceName":"1"}),makeQuery(id+"F8.opPattern","COPY",FACE,{"derivedFrom":makeQuery(id+"F5.opPattern","COPY",FACE,{"derivedFrom":subQ0,"instanceName":"1"}),"instanceName":"2"})]})});}
            var Q22;
            {var subQ0=makeQuery(id+"F4.opRevolve","SWEPT_FACE",FACE,{"disambiguationData":[OSD([sQuery(id+"F3.wireOp",EDGE,"E18")])]});Q22=makeQuery(id+"F10.opBoolean","COPY",EDGE,{"derivedFrom":makeQuery(id+"F9.opBoolean","INTERSECT",EDGE,{"disambiguationData":[OD(0.0)],"derivedFrom":[makeQuery(id+"F8.opPattern","COPY",FACE,{"derivedFrom":makeQuery(id+"F5.opPattern","COPY",FACE,{"derivedFrom":subQ0,"instanceName":"1"}),"instanceName":"1"}),makeQuery(id+"F8.opPattern","COPY",FACE,{"derivedFrom":subQ0,"instanceName":"2"})]})});}
            var Q23;
            {var subQ0=makeQuery(id+"F5.opPattern","COPY",FACE,{"derivedFrom":makeQuery(id+"F4.opRevolve","SWEPT_FACE",FACE,{"disambiguationData":[OSD([sQuery(id+"F3.wireOp",EDGE,"E18")])]}),"instanceName":"1"});Q23=makeQuery(id+"F10.opBoolean","COPY",EDGE,{"derivedFrom":makeQuery(id+"F9.opBoolean","INTERSECT",EDGE,{"disambiguationData":[OD(0.0)],"derivedFrom":[makeQuery(id+"F8.opPattern","COPY",FACE,{"derivedFrom":subQ0,"instanceName":"1"}),makeQuery(id+"F8.opPattern","COPY",FACE,{"derivedFrom":subQ0,"instanceName":"2"})]})});}
            fillet(context, id + "F11", {"entities" : qUnion([Q0, Q1, Q2, Q3, Q4, Q5, Q6, Q7, Q8, Q9, Q10, Q11, Q12, Q13, Q14, Q15, Q16, Q17, Q18, Q19, Q20, Q21, Q22, Q23]), "radius" : 2 * mm, "tangentPropagation" : true, "allowEdgeOverflow" : false});
        }
        {
            var Q0;
            {var subQ0=makeQuery(id+"F4.opRevolve","SWEPT_FACE",FACE,{"disambiguationData":[OSD([sQuery(id+"F3.wireOp",EDGE,"E18")])]});var subQ1=makeQuery(id+"F5.opPattern","COPY",FACE,{"derivedFrom":subQ0,"instanceName":"1"});var subQ2=makeQuery(id+"F4.opRevolve","SWEPT_FACE",FACE,{"disambiguationData":[OSD([sQuery(id+"F3.wireOp",EDGE,"E20")])]});var subQ3=makeQuery(id+"F5.opPattern","COPY",FACE,{"derivedFrom":subQ2,"instanceName":"1"});var subQ4=makeQuery(id+"F4.opRevolve","SWEPT_FACE",FACE,{"disambiguationData":[OSD([sQuery(id+"F3.wireOp",EDGE,"E17")])]});var subQ5=makeQuery(id+"F5.opPattern","COPY",FACE,{"derivedFrom":subQ4,"instanceName":"1"});Q0=makeQuery(id+"F10.opBoolean","INTERSECT",EDGE,{"derivedFrom":[makeQuery(id+"F2.opRevolve","SWEPT_FACE",FACE,{"disambiguationData":[OSD([sQuery(id+"F1.wireOp",EDGE,"E3")])]}),makeQuery(id+"F9.opBoolean","SPLIT",FACE,{"disambiguationData":[TD([makeQuery(id+"F8.opPattern","COPY",FACE,{"derivedFrom":subQ5,"instanceName":"1"}),makeQuery(id+"F8.opPattern","COPY",FACE,{"derivedFrom":subQ3,"instanceName":"1"}),makeQuery(id+"F8.opPattern","COPY",FACE,{"derivedFrom":subQ4,"instanceName":"2"}),makeQuery(id+"F8.opPattern","COPY",FACE,{"derivedFrom":subQ0,"instanceName":"2"}),makeQuery(id+"F8.opPattern","COPY",FACE,{"derivedFrom":subQ2,"instanceName":"2"}),makeQuery(id+"F8.opPattern","COPY",FACE,{"derivedFrom":subQ5,"instanceName":"2"}),makeQuery(id+"F8.opPattern","COPY",FACE,{"derivedFrom":subQ1,"instanceName":"2"}),makeQuery(id+"F8.opPattern","COPY",FACE,{"derivedFrom":subQ3,"instanceName":"2"})]),OD(1.0)],"derivedFrom":makeQuery(id+"F8.opPattern","COPY",FACE,{"derivedFrom":subQ1,"instanceName":"1"})})]});}
            var Q1;
            {var subQ0=makeQuery(id+"F4.opRevolve","SWEPT_FACE",FACE,{"disambiguationData":[OSD([sQuery(id+"F3.wireOp",EDGE,"E18")])]});var subQ1=makeQuery(id+"F5.opPattern","COPY",FACE,{"derivedFrom":subQ0,"instanceName":"1"});var subQ2=makeQuery(id+"F4.opRevolve","SWEPT_FACE",FACE,{"disambiguationData":[OSD([sQuery(id+"F3.wireOp",EDGE,"E20")])]});var subQ3=makeQuery(id+"F5.opPattern","COPY",FACE,{"derivedFrom":subQ2,"instanceName":"1"});var subQ4=makeQuery(id+"F4.opRevolve","SWEPT_FACE",FACE,{"disambiguationData":[OSD([sQuery(id+"F3.wireOp",EDGE,"E17")])]});var subQ5=makeQuery(id+"F5.opPattern","COPY",FACE,{"derivedFrom":subQ4,"instanceName":"1"});Q1=makeQuery(id+"F10.opBoolean","INTERSECT",EDGE,{"derivedFrom":[makeQuery(id+"F2.opRevolve","SWEPT_FACE",FACE,{"disambiguationData":[OSD([sQuery(id+"F1.wireOp",EDGE,"E3")])]}),makeQuery(id+"F9.opBoolean","SPLIT",FACE,{"disambiguationData":[TD([subQ4,subQ0,subQ2,subQ5,subQ1,subQ3,makeQuery(id+"F8.opPattern","COPY",FACE,{"derivedFrom":subQ5,"instanceName":"2"}),makeQuery(id+"F8.opPattern","COPY",FACE,{"derivedFrom":subQ3,"instanceName":"2"})]),OD(1.0)],"derivedFrom":makeQuery(id+"F8.opPattern","COPY",FACE,{"derivedFrom":subQ1,"instanceName":"2"})})]});}
            var Q2;
            {var subQ0=makeQuery(id+"F4.opRevolve","SWEPT_FACE",FACE,{"disambiguationData":[OSD([sQuery(id+"F3.wireOp",EDGE,"E18")])]});var subQ1=makeQuery(id+"F5.opPattern","COPY",FACE,{"derivedFrom":subQ0,"instanceName":"1"});var subQ2=makeQuery(id+"F4.opRevolve","SWEPT_FACE",FACE,{"disambiguationData":[OSD([sQuery(id+"F3.wireOp",EDGE,"E20")])]});var subQ3=makeQuery(id+"F5.opPattern","COPY",FACE,{"derivedFrom":subQ2,"instanceName":"1"});var subQ4=makeQuery(id+"F4.opRevolve","SWEPT_FACE",FACE,{"disambiguationData":[OSD([sQuery(id+"F3.wireOp",EDGE,"E17")])]});var subQ5=makeQuery(id+"F5.opPattern","COPY",FACE,{"derivedFrom":subQ4,"instanceName":"1"});Q2=makeQuery(id+"F10.opBoolean","INTERSECT",EDGE,{"derivedFrom":[makeQuery(id+"F2.opRevolve","SWEPT_FACE",FACE,{"disambiguationData":[OSD([sQuery(id+"F1.wireOp",EDGE,"E3")])]}),makeQuery(id+"F9.opBoolean","SPLIT",FACE,{"disambiguationData":[TD([subQ4,subQ0,subQ2,subQ5,subQ1,subQ3,makeQuery(id+"F8.opPattern","COPY",FACE,{"derivedFrom":subQ5,"instanceName":"1"}),makeQuery(id+"F8.opPattern","COPY",FACE,{"derivedFrom":subQ3,"instanceName":"1"})]),OD(1.0)],"derivedFrom":makeQuery(id+"F8.opPattern","COPY",FACE,{"derivedFrom":subQ1,"instanceName":"1"})})]});}
            var Q3;
            {var subQ0=makeQuery(id+"F4.opRevolve","SWEPT_FACE",FACE,{"disambiguationData":[OSD([sQuery(id+"F3.wireOp",EDGE,"E18")])]});var subQ1=makeQuery(id+"F5.opPattern","COPY",FACE,{"derivedFrom":subQ0,"instanceName":"1"});var subQ2=makeQuery(id+"F4.opRevolve","SWEPT_FACE",FACE,{"disambiguationData":[OSD([sQuery(id+"F3.wireOp",EDGE,"E20")])]});var subQ3=makeQuery(id+"F5.opPattern","COPY",FACE,{"derivedFrom":subQ2,"instanceName":"1"});var subQ4=makeQuery(id+"F4.opRevolve","SWEPT_FACE",FACE,{"disambiguationData":[OSD([sQuery(id+"F3.wireOp",EDGE,"E17")])]});var subQ5=makeQuery(id+"F5.opPattern","COPY",FACE,{"derivedFrom":subQ4,"instanceName":"1"});Q3=makeQuery(id+"F10.opBoolean","INTERSECT",EDGE,{"derivedFrom":[makeQuery(id+"F2.opRevolve","SWEPT_FACE",FACE,{"disambiguationData":[OSD([sQuery(id+"F1.wireOp",EDGE,"E3")])]}),makeQuery(id+"F9.opBoolean","SPLIT",FACE,{"disambiguationData":[TD([subQ4,subQ0,subQ2,subQ5,subQ1,subQ3,makeQuery(id+"F8.opPattern","COPY",FACE,{"derivedFrom":subQ5,"instanceName":"1"}),makeQuery(id+"F8.opPattern","COPY",FACE,{"derivedFrom":subQ3,"instanceName":"1"})]),OD(1.0)],"derivedFrom":makeQuery(id+"F8.opPattern","COPY",FACE,{"derivedFrom":subQ1,"instanceName":"1"})})]});}
            var Q4;
            {var subQ0=makeQuery(id+"F4.opRevolve","SWEPT_FACE",FACE,{"disambiguationData":[OSD([sQuery(id+"F3.wireOp",EDGE,"E18")])]});var subQ1=makeQuery(id+"F5.opPattern","COPY",FACE,{"derivedFrom":subQ0,"instanceName":"1"});var subQ2=makeQuery(id+"F4.opRevolve","SWEPT_FACE",FACE,{"disambiguationData":[OSD([sQuery(id+"F3.wireOp",EDGE,"E20")])]});var subQ3=makeQuery(id+"F5.opPattern","COPY",FACE,{"derivedFrom":subQ2,"instanceName":"1"});var subQ4=makeQuery(id+"F4.opRevolve","SWEPT_FACE",FACE,{"disambiguationData":[OSD([sQuery(id+"F3.wireOp",EDGE,"E17")])]});var subQ5=makeQuery(id+"F5.opPattern","COPY",FACE,{"derivedFrom":subQ4,"instanceName":"1"});Q4=makeQuery(id+"F10.opBoolean","INTERSECT",EDGE,{"derivedFrom":[makeQuery(id+"F2.opRevolve","SWEPT_FACE",FACE,{"disambiguationData":[OSD([sQuery(id+"F1.wireOp",EDGE,"E3")])]}),makeQuery(id+"F9.opBoolean","SPLIT",FACE,{"disambiguationData":[TD([makeQuery(id+"F8.opPattern","COPY",FACE,{"derivedFrom":subQ5,"instanceName":"1"}),makeQuery(id+"F8.opPattern","COPY",FACE,{"derivedFrom":subQ3,"instanceName":"1"}),makeQuery(id+"F8.opPattern","COPY",FACE,{"derivedFrom":subQ4,"instanceName":"2"}),makeQuery(id+"F8.opPattern","COPY",FACE,{"derivedFrom":subQ0,"instanceName":"2"}),makeQuery(id+"F8.opPattern","COPY",FACE,{"derivedFrom":subQ2,"instanceName":"2"}),makeQuery(id+"F8.opPattern","COPY",FACE,{"derivedFrom":subQ5,"instanceName":"2"}),makeQuery(id+"F8.opPattern","COPY",FACE,{"derivedFrom":subQ1,"instanceName":"2"}),makeQuery(id+"F8.opPattern","COPY",FACE,{"derivedFrom":subQ3,"instanceName":"2"})]),OD(0.0)],"derivedFrom":makeQuery(id+"F8.opPattern","COPY",FACE,{"derivedFrom":subQ1,"instanceName":"1"})})]});}
            var Q5;
            {var subQ0=makeQuery(id+"F4.opRevolve","SWEPT_FACE",FACE,{"disambiguationData":[OSD([sQuery(id+"F3.wireOp",EDGE,"E18")])]});var subQ1=makeQuery(id+"F5.opPattern","COPY",FACE,{"derivedFrom":subQ0,"instanceName":"1"});var subQ2=makeQuery(id+"F4.opRevolve","SWEPT_FACE",FACE,{"disambiguationData":[OSD([sQuery(id+"F3.wireOp",EDGE,"E20")])]});var subQ3=makeQuery(id+"F5.opPattern","COPY",FACE,{"derivedFrom":subQ2,"instanceName":"1"});var subQ4=makeQuery(id+"F4.opRevolve","SWEPT_FACE",FACE,{"disambiguationData":[OSD([sQuery(id+"F3.wireOp",EDGE,"E17")])]});var subQ5=makeQuery(id+"F5.opPattern","COPY",FACE,{"derivedFrom":subQ4,"instanceName":"1"});Q5=makeQuery(id+"F10.opBoolean","INTERSECT",EDGE,{"derivedFrom":[makeQuery(id+"F2.opRevolve","SWEPT_FACE",FACE,{"disambiguationData":[OSD([sQuery(id+"F1.wireOp",EDGE,"E3")])]}),makeQuery(id+"F9.opBoolean","SPLIT",FACE,{"disambiguationData":[TD([subQ4,subQ0,subQ2,subQ5,subQ1,subQ3,makeQuery(id+"F8.opPattern","COPY",FACE,{"derivedFrom":subQ5,"instanceName":"2"}),makeQuery(id+"F8.opPattern","COPY",FACE,{"derivedFrom":subQ3,"instanceName":"2"})]),OD(0.0)],"derivedFrom":makeQuery(id+"F8.opPattern","COPY",FACE,{"derivedFrom":subQ1,"instanceName":"2"})})]});}
            var Q6;
            {var subQ0=makeQuery(id+"F4.opRevolve","SWEPT_FACE",FACE,{"disambiguationData":[OSD([sQuery(id+"F3.wireOp",EDGE,"E18")])]});var subQ1=makeQuery(id+"F5.opPattern","COPY",FACE,{"derivedFrom":subQ0,"instanceName":"1"});var subQ2=makeQuery(id+"F4.opRevolve","SWEPT_FACE",FACE,{"disambiguationData":[OSD([sQuery(id+"F3.wireOp",EDGE,"E20")])]});var subQ3=makeQuery(id+"F5.opPattern","COPY",FACE,{"derivedFrom":subQ2,"instanceName":"1"});var subQ4=makeQuery(id+"F4.opRevolve","SWEPT_FACE",FACE,{"disambiguationData":[OSD([sQuery(id+"F3.wireOp",EDGE,"E17")])]});var subQ5=makeQuery(id+"F5.opPattern","COPY",FACE,{"derivedFrom":subQ4,"instanceName":"1"});Q6=makeQuery(id+"F10.opBoolean","INTERSECT",EDGE,{"derivedFrom":[makeQuery(id+"F2.opRevolve","SWEPT_FACE",FACE,{"disambiguationData":[OSD([sQuery(id+"F1.wireOp",EDGE,"E3")])]}),makeQuery(id+"F9.opBoolean","SPLIT",FACE,{"disambiguationData":[TD([subQ4,subQ0,subQ2,subQ5,subQ1,subQ3,makeQuery(id+"F8.opPattern","COPY",FACE,{"derivedFrom":subQ5,"instanceName":"1"}),makeQuery(id+"F8.opPattern","COPY",FACE,{"derivedFrom":subQ3,"instanceName":"1"})]),OD(0.0)],"derivedFrom":makeQuery(id+"F8.opPattern","COPY",FACE,{"derivedFrom":subQ1,"instanceName":"1"})})]});}
            fillet(context, id + "F12", {"entities" : qUnion([Q0, Q1, Q2, Q3, Q4, Q5, Q6]), "radius" : .5 * mm, "tangentPropagation" : true, "allowEdgeOverflow" : false});
        }
        {
            var Q0;
            Q0=makeQuery(id+"F10.opBoolean","COPY",EDGE,{"derivedFrom":makeQuery(id+"F9.opBoolean","INTERSECT",EDGE,{"disambiguationData":[OD(1.0)],"derivedFrom":[makeQuery(id+"F5.opPattern","COPY",FACE,{"derivedFrom":makeQuery(id+"F4.opRevolve","SWEPT_FACE",FACE,{"disambiguationData":[OSD([sQuery(id+"F3.wireOp",EDGE,"E19.0")])]}),"instanceName":"1"}),makeQuery(id+"F8.opPattern","COPY",FACE,{"derivedFrom":makeQuery(id+"F4.opRevolve","SWEPT_FACE",FACE,{"disambiguationData":[OSD([sQuery(id+"F3.wireOp",EDGE,"E18")])]}),"instanceName":"2"})]})});
            var Q1;
            Q1=makeQuery(id+"F10.opBoolean","COPY",EDGE,{"derivedFrom":makeQuery(id+"F9.opBoolean","INTERSECT",EDGE,{"disambiguationData":[OD(1.0)],"derivedFrom":[makeQuery(id+"F5.opPattern","COPY",FACE,{"derivedFrom":makeQuery(id+"F4.opRevolve","SWEPT_FACE",FACE,{"disambiguationData":[OSD([sQuery(id+"F3.wireOp",EDGE,"E18")])]}),"instanceName":"1"}),makeQuery(id+"F8.opPattern","COPY",FACE,{"derivedFrom":makeQuery(id+"F4.opRevolve","SWEPT_FACE",FACE,{"disambiguationData":[OSD([sQuery(id+"F3.wireOp",EDGE,"E19.0")])]}),"instanceName":"2"})]})});
            var Q2;
            Q2=makeQuery(id+"F10.opBoolean","COPY",EDGE,{"derivedFrom":makeQuery(id+"F9.opBoolean","INTERSECT",EDGE,{"disambiguationData":[OD(1.0)],"derivedFrom":[makeQuery(id+"F5.opPattern","COPY",FACE,{"derivedFrom":makeQuery(id+"F4.opRevolve","SWEPT_FACE",FACE,{"disambiguationData":[OSD([sQuery(id+"F3.wireOp",EDGE,"E18")])]}),"instanceName":"1"}),makeQuery(id+"F8.opPattern","COPY",FACE,{"derivedFrom":makeQuery(id+"F5.opPattern","COPY",FACE,{"derivedFrom":makeQuery(id+"F4.opRevolve","SWEPT_FACE",FACE,{"disambiguationData":[OSD([sQuery(id+"F3.wireOp",EDGE,"E19.0")])]}),"instanceName":"1"}),"instanceName":"2"})]})});
            var Q3;
            Q3=makeQuery(id+"F10.opBoolean","COPY",EDGE,{"derivedFrom":makeQuery(id+"F9.opBoolean","INTERSECT",EDGE,{"disambiguationData":[OD(1.0)],"derivedFrom":[makeQuery(id+"F5.opPattern","COPY",FACE,{"derivedFrom":makeQuery(id+"F4.opRevolve","SWEPT_FACE",FACE,{"disambiguationData":[OSD([sQuery(id+"F3.wireOp",EDGE,"E19.0")])]}),"instanceName":"1"}),makeQuery(id+"F8.opPattern","COPY",FACE,{"derivedFrom":makeQuery(id+"F5.opPattern","COPY",FACE,{"derivedFrom":makeQuery(id+"F4.opRevolve","SWEPT_FACE",FACE,{"disambiguationData":[OSD([sQuery(id+"F3.wireOp",EDGE,"E18")])]}),"instanceName":"1"}),"instanceName":"2"})]})});
            var Q4;
            Q4=makeQuery(id+"F10.opBoolean","COPY",EDGE,{"derivedFrom":makeQuery(id+"F9.opBoolean","INTERSECT",EDGE,{"disambiguationData":[OD(1.0)],"derivedFrom":[makeQuery(id+"F4.opRevolve","SWEPT_FACE",FACE,{"disambiguationData":[OSD([sQuery(id+"F3.wireOp",EDGE,"E18")])]}),makeQuery(id+"F8.opPattern","COPY",FACE,{"derivedFrom":makeQuery(id+"F5.opPattern","COPY",FACE,{"derivedFrom":makeQuery(id+"F4.opRevolve","SWEPT_FACE",FACE,{"disambiguationData":[OSD([sQuery(id+"F3.wireOp",EDGE,"E19.0")])]}),"instanceName":"1"}),"instanceName":"2"})]})});
            var Q5;
            Q5=makeQuery(id+"F10.opBoolean","COPY",EDGE,{"derivedFrom":makeQuery(id+"F9.opBoolean","INTERSECT",EDGE,{"disambiguationData":[OD(1.0)],"derivedFrom":[makeQuery(id+"F4.opRevolve","SWEPT_FACE",FACE,{"disambiguationData":[OSD([sQuery(id+"F3.wireOp",EDGE,"E19.0")])]}),makeQuery(id+"F8.opPattern","COPY",FACE,{"derivedFrom":makeQuery(id+"F5.opPattern","COPY",FACE,{"derivedFrom":makeQuery(id+"F4.opRevolve","SWEPT_FACE",FACE,{"disambiguationData":[OSD([sQuery(id+"F3.wireOp",EDGE,"E18")])]}),"instanceName":"1"}),"instanceName":"2"})]})});
            var Q6;
            Q6=makeQuery(id+"F10.opBoolean","COPY",EDGE,{"derivedFrom":makeQuery(id+"F9.opBoolean","INTERSECT",EDGE,{"disambiguationData":[OD(1.0)],"derivedFrom":[makeQuery(id+"F4.opRevolve","SWEPT_FACE",FACE,{"disambiguationData":[OSD([sQuery(id+"F3.wireOp",EDGE,"E19.0")])]}),makeQuery(id+"F8.opPattern","COPY",FACE,{"derivedFrom":makeQuery(id+"F4.opRevolve","SWEPT_FACE",FACE,{"disambiguationData":[OSD([sQuery(id+"F3.wireOp",EDGE,"E18")])]}),"instanceName":"2"})]})});
            var Q7;
            Q7=makeQuery(id+"F10.opBoolean","COPY",EDGE,{"derivedFrom":makeQuery(id+"F9.opBoolean","INTERSECT",EDGE,{"disambiguationData":[OD(1.0)],"derivedFrom":[makeQuery(id+"F4.opRevolve","SWEPT_FACE",FACE,{"disambiguationData":[OSD([sQuery(id+"F3.wireOp",EDGE,"E18")])]}),makeQuery(id+"F8.opPattern","COPY",FACE,{"derivedFrom":makeQuery(id+"F4.opRevolve","SWEPT_FACE",FACE,{"disambiguationData":[OSD([sQuery(id+"F3.wireOp",EDGE,"E19.0")])]}),"instanceName":"2"})]})});
            var Q8;
            Q8=makeQuery(id+"F10.opBoolean","COPY",EDGE,{"derivedFrom":makeQuery(id+"F9.opBoolean","INTERSECT",EDGE,{"disambiguationData":[OD(0.0)],"derivedFrom":[makeQuery(id+"F5.opPattern","COPY",FACE,{"derivedFrom":makeQuery(id+"F4.opRevolve","SWEPT_FACE",FACE,{"disambiguationData":[OSD([sQuery(id+"F3.wireOp",EDGE,"E18")])]}),"instanceName":"1"}),makeQuery(id+"F8.opPattern","COPY",FACE,{"derivedFrom":makeQuery(id+"F5.opPattern","COPY",FACE,{"derivedFrom":makeQuery(id+"F4.opRevolve","SWEPT_FACE",FACE,{"disambiguationData":[OSD([sQuery(id+"F3.wireOp",EDGE,"E19.0")])]}),"instanceName":"1"}),"instanceName":"1"})]})});
            var Q9;
            Q9=makeQuery(id+"F10.opBoolean","COPY",EDGE,{"derivedFrom":makeQuery(id+"F9.opBoolean","INTERSECT",EDGE,{"disambiguationData":[OD(0.0)],"derivedFrom":[makeQuery(id+"F5.opPattern","COPY",FACE,{"derivedFrom":makeQuery(id+"F4.opRevolve","SWEPT_FACE",FACE,{"disambiguationData":[OSD([sQuery(id+"F3.wireOp",EDGE,"E19.0")])]}),"instanceName":"1"}),makeQuery(id+"F8.opPattern","COPY",FACE,{"derivedFrom":makeQuery(id+"F5.opPattern","COPY",FACE,{"derivedFrom":makeQuery(id+"F4.opRevolve","SWEPT_FACE",FACE,{"disambiguationData":[OSD([sQuery(id+"F3.wireOp",EDGE,"E18")])]}),"instanceName":"1"}),"instanceName":"1"})]})});
            var Q10;
            Q10=makeQuery(id+"F10.opBoolean","COPY",EDGE,{"derivedFrom":makeQuery(id+"F9.opBoolean","INTERSECT",EDGE,{"disambiguationData":[OD(0.0)],"derivedFrom":[makeQuery(id+"F4.opRevolve","SWEPT_FACE",FACE,{"disambiguationData":[OSD([sQuery(id+"F3.wireOp",EDGE,"E19.0")])]}),makeQuery(id+"F8.opPattern","COPY",FACE,{"derivedFrom":makeQuery(id+"F5.opPattern","COPY",FACE,{"derivedFrom":makeQuery(id+"F4.opRevolve","SWEPT_FACE",FACE,{"disambiguationData":[OSD([sQuery(id+"F3.wireOp",EDGE,"E18")])]}),"instanceName":"1"}),"instanceName":"1"})]})});
            var Q11;
            Q11=makeQuery(id+"F10.opBoolean","COPY",EDGE,{"derivedFrom":makeQuery(id+"F9.opBoolean","INTERSECT",EDGE,{"disambiguationData":[OD(0.0)],"derivedFrom":[makeQuery(id+"F4.opRevolve","SWEPT_FACE",FACE,{"disambiguationData":[OSD([sQuery(id+"F3.wireOp",EDGE,"E18")])]}),makeQuery(id+"F8.opPattern","COPY",FACE,{"derivedFrom":makeQuery(id+"F5.opPattern","COPY",FACE,{"derivedFrom":makeQuery(id+"F4.opRevolve","SWEPT_FACE",FACE,{"disambiguationData":[OSD([sQuery(id+"F3.wireOp",EDGE,"E19.0")])]}),"instanceName":"1"}),"instanceName":"1"})]})});
            var Q12;
            Q12=makeQuery(id+"F10.opBoolean","COPY",EDGE,{"derivedFrom":makeQuery(id+"F9.opBoolean","INTERSECT",EDGE,{"disambiguationData":[OD(0.0)],"derivedFrom":[makeQuery(id+"F5.opPattern","COPY",FACE,{"derivedFrom":makeQuery(id+"F4.opRevolve","SWEPT_FACE",FACE,{"disambiguationData":[OSD([sQuery(id+"F3.wireOp",EDGE,"E18")])]}),"instanceName":"1"}),makeQuery(id+"F8.opPattern","COPY",FACE,{"derivedFrom":makeQuery(id+"F4.opRevolve","SWEPT_FACE",FACE,{"disambiguationData":[OSD([sQuery(id+"F3.wireOp",EDGE,"E19.0")])]}),"instanceName":"1"})]})});
            var Q13;
            Q13=makeQuery(id+"F10.opBoolean","COPY",EDGE,{"derivedFrom":makeQuery(id+"F9.opBoolean","INTERSECT",EDGE,{"disambiguationData":[OD(0.0)],"derivedFrom":[makeQuery(id+"F5.opPattern","COPY",FACE,{"derivedFrom":makeQuery(id+"F4.opRevolve","SWEPT_FACE",FACE,{"disambiguationData":[OSD([sQuery(id+"F3.wireOp",EDGE,"E19.0")])]}),"instanceName":"1"}),makeQuery(id+"F8.opPattern","COPY",FACE,{"derivedFrom":makeQuery(id+"F4.opRevolve","SWEPT_FACE",FACE,{"disambiguationData":[OSD([sQuery(id+"F3.wireOp",EDGE,"E18")])]}),"instanceName":"1"})]})});
            var Q14;
            Q14=makeQuery(id+"F10.opBoolean","COPY",EDGE,{"derivedFrom":makeQuery(id+"F9.opBoolean","INTERSECT",EDGE,{"disambiguationData":[OD(0.0)],"derivedFrom":[makeQuery(id+"F4.opRevolve","SWEPT_FACE",FACE,{"disambiguationData":[OSD([sQuery(id+"F3.wireOp",EDGE,"E19.0")])]}),makeQuery(id+"F8.opPattern","COPY",FACE,{"derivedFrom":makeQuery(id+"F4.opRevolve","SWEPT_FACE",FACE,{"disambiguationData":[OSD([sQuery(id+"F3.wireOp",EDGE,"E18")])]}),"instanceName":"1"})]})});
            var Q15;
            Q15=makeQuery(id+"F10.opBoolean","COPY",EDGE,{"derivedFrom":makeQuery(id+"F9.opBoolean","INTERSECT",EDGE,{"disambiguationData":[OD(0.0)],"derivedFrom":[makeQuery(id+"F4.opRevolve","SWEPT_FACE",FACE,{"disambiguationData":[OSD([sQuery(id+"F3.wireOp",EDGE,"E18")])]}),makeQuery(id+"F8.opPattern","COPY",FACE,{"derivedFrom":makeQuery(id+"F4.opRevolve","SWEPT_FACE",FACE,{"disambiguationData":[OSD([sQuery(id+"F3.wireOp",EDGE,"E19.0")])]}),"instanceName":"1"})]})});
            var Q16;
            Q16=makeQuery(id+"F10.opBoolean","COPY",EDGE,{"derivedFrom":makeQuery(id+"F9.opBoolean","INTERSECT",EDGE,{"disambiguationData":[OD(1.0)],"derivedFrom":[makeQuery(id+"F8.opPattern","COPY",FACE,{"derivedFrom":makeQuery(id+"F4.opRevolve","SWEPT_FACE",FACE,{"disambiguationData":[OSD([sQuery(id+"F3.wireOp",EDGE,"E18")])]}),"instanceName":"1"}),makeQuery(id+"F8.opPattern","COPY",FACE,{"derivedFrom":makeQuery(id+"F5.opPattern","COPY",FACE,{"derivedFrom":makeQuery(id+"F4.opRevolve","SWEPT_FACE",FACE,{"disambiguationData":[OSD([sQuery(id+"F3.wireOp",EDGE,"E19.0")])]}),"instanceName":"1"}),"instanceName":"2"})]})});
            var Q17;
            Q17=makeQuery(id+"F10.opBoolean","COPY",EDGE,{"derivedFrom":makeQuery(id+"F9.opBoolean","INTERSECT",EDGE,{"disambiguationData":[OD(1.0)],"derivedFrom":[makeQuery(id+"F8.opPattern","COPY",FACE,{"derivedFrom":makeQuery(id+"F4.opRevolve","SWEPT_FACE",FACE,{"disambiguationData":[OSD([sQuery(id+"F3.wireOp",EDGE,"E19.0")])]}),"instanceName":"1"}),makeQuery(id+"F8.opPattern","COPY",FACE,{"derivedFrom":makeQuery(id+"F5.opPattern","COPY",FACE,{"derivedFrom":makeQuery(id+"F4.opRevolve","SWEPT_FACE",FACE,{"disambiguationData":[OSD([sQuery(id+"F3.wireOp",EDGE,"E18")])]}),"instanceName":"1"}),"instanceName":"2"})]})});
            var Q18;
            Q18=makeQuery(id+"F10.opBoolean","COPY",EDGE,{"derivedFrom":makeQuery(id+"F9.opBoolean","INTERSECT",EDGE,{"disambiguationData":[OD(1.0)],"derivedFrom":[makeQuery(id+"F8.opPattern","COPY",FACE,{"derivedFrom":makeQuery(id+"F5.opPattern","COPY",FACE,{"derivedFrom":makeQuery(id+"F4.opRevolve","SWEPT_FACE",FACE,{"disambiguationData":[OSD([sQuery(id+"F3.wireOp",EDGE,"E18")])]}),"instanceName":"1"}),"instanceName":"1"}),makeQuery(id+"F8.opPattern","COPY",FACE,{"derivedFrom":makeQuery(id+"F4.opRevolve","SWEPT_FACE",FACE,{"disambiguationData":[OSD([sQuery(id+"F3.wireOp",EDGE,"E19.0")])]}),"instanceName":"2"})]})});
            var Q19;
            Q19=makeQuery(id+"F10.opBoolean","COPY",EDGE,{"derivedFrom":makeQuery(id+"F9.opBoolean","INTERSECT",EDGE,{"disambiguationData":[OD(1.0)],"derivedFrom":[makeQuery(id+"F8.opPattern","COPY",FACE,{"derivedFrom":makeQuery(id+"F5.opPattern","COPY",FACE,{"derivedFrom":makeQuery(id+"F4.opRevolve","SWEPT_FACE",FACE,{"disambiguationData":[OSD([sQuery(id+"F3.wireOp",EDGE,"E19.0")])]}),"instanceName":"1"}),"instanceName":"1"}),makeQuery(id+"F8.opPattern","COPY",FACE,{"derivedFrom":makeQuery(id+"F4.opRevolve","SWEPT_FACE",FACE,{"disambiguationData":[OSD([sQuery(id+"F3.wireOp",EDGE,"E18")])]}),"instanceName":"2"})]})});
            var Q20;
            Q20=makeQuery(id+"F10.opBoolean","COPY",EDGE,{"derivedFrom":makeQuery(id+"F9.opBoolean","INTERSECT",EDGE,{"disambiguationData":[OD(1.0)],"derivedFrom":[makeQuery(id+"F8.opPattern","COPY",FACE,{"derivedFrom":makeQuery(id+"F5.opPattern","COPY",FACE,{"derivedFrom":makeQuery(id+"F4.opRevolve","SWEPT_FACE",FACE,{"disambiguationData":[OSD([sQuery(id+"F3.wireOp",EDGE,"E18")])]}),"instanceName":"1"}),"instanceName":"1"}),makeQuery(id+"F8.opPattern","COPY",FACE,{"derivedFrom":makeQuery(id+"F5.opPattern","COPY",FACE,{"derivedFrom":makeQuery(id+"F4.opRevolve","SWEPT_FACE",FACE,{"disambiguationData":[OSD([sQuery(id+"F3.wireOp",EDGE,"E19.0")])]}),"instanceName":"1"}),"instanceName":"2"})]})});
            var Q21;
            Q21=makeQuery(id+"F10.opBoolean","COPY",EDGE,{"derivedFrom":makeQuery(id+"F9.opBoolean","INTERSECT",EDGE,{"disambiguationData":[OD(1.0)],"derivedFrom":[makeQuery(id+"F8.opPattern","COPY",FACE,{"derivedFrom":makeQuery(id+"F5.opPattern","COPY",FACE,{"derivedFrom":makeQuery(id+"F4.opRevolve","SWEPT_FACE",FACE,{"disambiguationData":[OSD([sQuery(id+"F3.wireOp",EDGE,"E19.0")])]}),"instanceName":"1"}),"instanceName":"1"}),makeQuery(id+"F8.opPattern","COPY",FACE,{"derivedFrom":makeQuery(id+"F5.opPattern","COPY",FACE,{"derivedFrom":makeQuery(id+"F4.opRevolve","SWEPT_FACE",FACE,{"disambiguationData":[OSD([sQuery(id+"F3.wireOp",EDGE,"E18")])]}),"instanceName":"1"}),"instanceName":"2"})]})});
            var Q22;
            Q22=makeQuery(id+"F10.opBoolean","COPY",EDGE,{"derivedFrom":makeQuery(id+"F9.opBoolean","INTERSECT",EDGE,{"disambiguationData":[OD(1.0)],"derivedFrom":[makeQuery(id+"F8.opPattern","COPY",FACE,{"derivedFrom":makeQuery(id+"F4.opRevolve","SWEPT_FACE",FACE,{"disambiguationData":[OSD([sQuery(id+"F3.wireOp",EDGE,"E19.0")])]}),"instanceName":"1"}),makeQuery(id+"F8.opPattern","COPY",FACE,{"derivedFrom":makeQuery(id+"F4.opRevolve","SWEPT_FACE",FACE,{"disambiguationData":[OSD([sQuery(id+"F3.wireOp",EDGE,"E18")])]}),"instanceName":"2"})]})});
            var Q23;
            Q23=makeQuery(id+"F10.opBoolean","COPY",EDGE,{"derivedFrom":makeQuery(id+"F9.opBoolean","INTERSECT",EDGE,{"disambiguationData":[OD(1.0)],"derivedFrom":[makeQuery(id+"F8.opPattern","COPY",FACE,{"derivedFrom":makeQuery(id+"F4.opRevolve","SWEPT_FACE",FACE,{"disambiguationData":[OSD([sQuery(id+"F3.wireOp",EDGE,"E18")])]}),"instanceName":"1"}),makeQuery(id+"F8.opPattern","COPY",FACE,{"derivedFrom":makeQuery(id+"F4.opRevolve","SWEPT_FACE",FACE,{"disambiguationData":[OSD([sQuery(id+"F3.wireOp",EDGE,"E19.0")])]}),"instanceName":"2"})]})});
            fillet(context, id + "F13", {"entities" : qUnion([Q0, Q1, Q2, Q3, Q4, Q5, Q6, Q7, Q8, Q9, Q10, Q11, Q12, Q13, Q14, Q15, Q16, Q17, Q18, Q19, Q20, Q21, Q22, Q23]), "radius" : 2 * mm, "tangentPropagation" : true, "allowEdgeOverflow" : false});
        }
        {
            var Q0;
            Q0=makeQuery(id+"F10.opBoolean","COPY",EDGE,{"derivedFrom":makeQuery(id+"F9.opBoolean","INTERSECT",EDGE,{"disambiguationData":[OD(0.0)],"derivedFrom":[makeQuery(id+"F5.opPattern","COPY",FACE,{"derivedFrom":makeQuery(id+"F4.opRevolve","SWEPT_FACE",FACE,{"disambiguationData":[OSD([sQuery(id+"F3.wireOp",EDGE,"E18")])]}),"instanceName":"1"}),makeQuery(id+"F8.opPattern","COPY",FACE,{"derivedFrom":makeQuery(id+"F4.opRevolve","SWEPT_FACE",FACE,{"disambiguationData":[OSD([sQuery(id+"F3.wireOp",EDGE,"E19.0")])]}),"instanceName":"2"})]})});
            var Q1;
            Q1=makeQuery(id+"F10.opBoolean","COPY",EDGE,{"derivedFrom":makeQuery(id+"F9.opBoolean","INTERSECT",EDGE,{"disambiguationData":[OD(0.0)],"derivedFrom":[makeQuery(id+"F5.opPattern","COPY",FACE,{"derivedFrom":makeQuery(id+"F4.opRevolve","SWEPT_FACE",FACE,{"disambiguationData":[OSD([sQuery(id+"F3.wireOp",EDGE,"E19.0")])]}),"instanceName":"1"}),makeQuery(id+"F8.opPattern","COPY",FACE,{"derivedFrom":makeQuery(id+"F4.opRevolve","SWEPT_FACE",FACE,{"disambiguationData":[OSD([sQuery(id+"F3.wireOp",EDGE,"E18")])]}),"instanceName":"2"})]})});
            var Q2;
            Q2=makeQuery(id+"F10.opBoolean","COPY",EDGE,{"derivedFrom":makeQuery(id+"F9.opBoolean","INTERSECT",EDGE,{"disambiguationData":[OD(0.0)],"derivedFrom":[makeQuery(id+"F4.opRevolve","SWEPT_FACE",FACE,{"disambiguationData":[OSD([sQuery(id+"F3.wireOp",EDGE,"E19.0")])]}),makeQuery(id+"F8.opPattern","COPY",FACE,{"derivedFrom":makeQuery(id+"F4.opRevolve","SWEPT_FACE",FACE,{"disambiguationData":[OSD([sQuery(id+"F3.wireOp",EDGE,"E18")])]}),"instanceName":"2"})]})});
            var Q3;
            Q3=makeQuery(id+"F10.opBoolean","COPY",EDGE,{"derivedFrom":makeQuery(id+"F9.opBoolean","INTERSECT",EDGE,{"disambiguationData":[OD(0.0)],"derivedFrom":[makeQuery(id+"F4.opRevolve","SWEPT_FACE",FACE,{"disambiguationData":[OSD([sQuery(id+"F3.wireOp",EDGE,"E18")])]}),makeQuery(id+"F8.opPattern","COPY",FACE,{"derivedFrom":makeQuery(id+"F4.opRevolve","SWEPT_FACE",FACE,{"disambiguationData":[OSD([sQuery(id+"F3.wireOp",EDGE,"E19.0")])]}),"instanceName":"2"})]})});
            var Q4;
            Q4=makeQuery(id+"F10.opBoolean","COPY",EDGE,{"derivedFrom":makeQuery(id+"F9.opBoolean","INTERSECT",EDGE,{"disambiguationData":[OD(0.0)],"derivedFrom":[makeQuery(id+"F5.opPattern","COPY",FACE,{"derivedFrom":makeQuery(id+"F4.opRevolve","SWEPT_FACE",FACE,{"disambiguationData":[OSD([sQuery(id+"F3.wireOp",EDGE,"E18")])]}),"instanceName":"1"}),makeQuery(id+"F8.opPattern","COPY",FACE,{"derivedFrom":makeQuery(id+"F5.opPattern","COPY",FACE,{"derivedFrom":makeQuery(id+"F4.opRevolve","SWEPT_FACE",FACE,{"disambiguationData":[OSD([sQuery(id+"F3.wireOp",EDGE,"E19.0")])]}),"instanceName":"1"}),"instanceName":"2"})]})});
            var Q5;
            Q5=makeQuery(id+"F10.opBoolean","COPY",EDGE,{"derivedFrom":makeQuery(id+"F9.opBoolean","INTERSECT",EDGE,{"disambiguationData":[OD(0.0)],"derivedFrom":[makeQuery(id+"F5.opPattern","COPY",FACE,{"derivedFrom":makeQuery(id+"F4.opRevolve","SWEPT_FACE",FACE,{"disambiguationData":[OSD([sQuery(id+"F3.wireOp",EDGE,"E19.0")])]}),"instanceName":"1"}),makeQuery(id+"F8.opPattern","COPY",FACE,{"derivedFrom":makeQuery(id+"F5.opPattern","COPY",FACE,{"derivedFrom":makeQuery(id+"F4.opRevolve","SWEPT_FACE",FACE,{"disambiguationData":[OSD([sQuery(id+"F3.wireOp",EDGE,"E18")])]}),"instanceName":"1"}),"instanceName":"2"})]})});
            var Q6;
            Q6=makeQuery(id+"F10.opBoolean","COPY",EDGE,{"derivedFrom":makeQuery(id+"F9.opBoolean","INTERSECT",EDGE,{"disambiguationData":[OD(0.0)],"derivedFrom":[makeQuery(id+"F4.opRevolve","SWEPT_FACE",FACE,{"disambiguationData":[OSD([sQuery(id+"F3.wireOp",EDGE,"E18")])]}),makeQuery(id+"F8.opPattern","COPY",FACE,{"derivedFrom":makeQuery(id+"F5.opPattern","COPY",FACE,{"derivedFrom":makeQuery(id+"F4.opRevolve","SWEPT_FACE",FACE,{"disambiguationData":[OSD([sQuery(id+"F3.wireOp",EDGE,"E19.0")])]}),"instanceName":"1"}),"instanceName":"2"})]})});
            var Q7;
            Q7=makeQuery(id+"F10.opBoolean","COPY",EDGE,{"derivedFrom":makeQuery(id+"F9.opBoolean","INTERSECT",EDGE,{"disambiguationData":[OD(0.0)],"derivedFrom":[makeQuery(id+"F4.opRevolve","SWEPT_FACE",FACE,{"disambiguationData":[OSD([sQuery(id+"F3.wireOp",EDGE,"E19.0")])]}),makeQuery(id+"F8.opPattern","COPY",FACE,{"derivedFrom":makeQuery(id+"F5.opPattern","COPY",FACE,{"derivedFrom":makeQuery(id+"F4.opRevolve","SWEPT_FACE",FACE,{"disambiguationData":[OSD([sQuery(id+"F3.wireOp",EDGE,"E18")])]}),"instanceName":"1"}),"instanceName":"2"})]})});
            var Q8;
            Q8=makeQuery(id+"F10.opBoolean","COPY",EDGE,{"derivedFrom":makeQuery(id+"F9.opBoolean","INTERSECT",EDGE,{"disambiguationData":[OD(0.0)],"derivedFrom":[makeQuery(id+"F8.opPattern","COPY",FACE,{"derivedFrom":makeQuery(id+"F5.opPattern","COPY",FACE,{"derivedFrom":makeQuery(id+"F4.opRevolve","SWEPT_FACE",FACE,{"disambiguationData":[OSD([sQuery(id+"F3.wireOp",EDGE,"E19.0")])]}),"instanceName":"1"}),"instanceName":"1"}),makeQuery(id+"F8.opPattern","COPY",FACE,{"derivedFrom":makeQuery(id+"F4.opRevolve","SWEPT_FACE",FACE,{"disambiguationData":[OSD([sQuery(id+"F3.wireOp",EDGE,"E18")])]}),"instanceName":"2"})]})});
            var Q9;
            Q9=makeQuery(id+"F10.opBoolean","COPY",EDGE,{"derivedFrom":makeQuery(id+"F9.opBoolean","INTERSECT",EDGE,{"disambiguationData":[OD(0.0)],"derivedFrom":[makeQuery(id+"F8.opPattern","COPY",FACE,{"derivedFrom":makeQuery(id+"F5.opPattern","COPY",FACE,{"derivedFrom":makeQuery(id+"F4.opRevolve","SWEPT_FACE",FACE,{"disambiguationData":[OSD([sQuery(id+"F3.wireOp",EDGE,"E18")])]}),"instanceName":"1"}),"instanceName":"1"}),makeQuery(id+"F8.opPattern","COPY",FACE,{"derivedFrom":makeQuery(id+"F4.opRevolve","SWEPT_FACE",FACE,{"disambiguationData":[OSD([sQuery(id+"F3.wireOp",EDGE,"E19.0")])]}),"instanceName":"2"})]})});
            var Q10;
            Q10=makeQuery(id+"F10.opBoolean","COPY",EDGE,{"derivedFrom":makeQuery(id+"F9.opBoolean","INTERSECT",EDGE,{"disambiguationData":[OD(0.0)],"derivedFrom":[makeQuery(id+"F8.opPattern","COPY",FACE,{"derivedFrom":makeQuery(id+"F5.opPattern","COPY",FACE,{"derivedFrom":makeQuery(id+"F4.opRevolve","SWEPT_FACE",FACE,{"disambiguationData":[OSD([sQuery(id+"F3.wireOp",EDGE,"E18")])]}),"instanceName":"1"}),"instanceName":"1"}),makeQuery(id+"F8.opPattern","COPY",FACE,{"derivedFrom":makeQuery(id+"F5.opPattern","COPY",FACE,{"derivedFrom":makeQuery(id+"F4.opRevolve","SWEPT_FACE",FACE,{"disambiguationData":[OSD([sQuery(id+"F3.wireOp",EDGE,"E19.0")])]}),"instanceName":"1"}),"instanceName":"2"})]})});
            var Q11;
            Q11=makeQuery(id+"F10.opBoolean","COPY",EDGE,{"derivedFrom":makeQuery(id+"F9.opBoolean","INTERSECT",EDGE,{"disambiguationData":[OD(0.0)],"derivedFrom":[makeQuery(id+"F8.opPattern","COPY",FACE,{"derivedFrom":makeQuery(id+"F5.opPattern","COPY",FACE,{"derivedFrom":makeQuery(id+"F4.opRevolve","SWEPT_FACE",FACE,{"disambiguationData":[OSD([sQuery(id+"F3.wireOp",EDGE,"E19.0")])]}),"instanceName":"1"}),"instanceName":"1"}),makeQuery(id+"F8.opPattern","COPY",FACE,{"derivedFrom":makeQuery(id+"F5.opPattern","COPY",FACE,{"derivedFrom":makeQuery(id+"F4.opRevolve","SWEPT_FACE",FACE,{"disambiguationData":[OSD([sQuery(id+"F3.wireOp",EDGE,"E18")])]}),"instanceName":"1"}),"instanceName":"2"})]})});
            var Q12;
            Q12=makeQuery(id+"F10.opBoolean","COPY",EDGE,{"derivedFrom":makeQuery(id+"F9.opBoolean","INTERSECT",EDGE,{"disambiguationData":[OD(0.0)],"derivedFrom":[makeQuery(id+"F8.opPattern","COPY",FACE,{"derivedFrom":makeQuery(id+"F4.opRevolve","SWEPT_FACE",FACE,{"disambiguationData":[OSD([sQuery(id+"F3.wireOp",EDGE,"E18")])]}),"instanceName":"1"}),makeQuery(id+"F8.opPattern","COPY",FACE,{"derivedFrom":makeQuery(id+"F5.opPattern","COPY",FACE,{"derivedFrom":makeQuery(id+"F4.opRevolve","SWEPT_FACE",FACE,{"disambiguationData":[OSD([sQuery(id+"F3.wireOp",EDGE,"E19.0")])]}),"instanceName":"1"}),"instanceName":"2"})]})});
            var Q13;
            Q13=makeQuery(id+"F10.opBoolean","COPY",EDGE,{"derivedFrom":makeQuery(id+"F9.opBoolean","INTERSECT",EDGE,{"disambiguationData":[OD(0.0)],"derivedFrom":[makeQuery(id+"F8.opPattern","COPY",FACE,{"derivedFrom":makeQuery(id+"F4.opRevolve","SWEPT_FACE",FACE,{"disambiguationData":[OSD([sQuery(id+"F3.wireOp",EDGE,"E19.0")])]}),"instanceName":"1"}),makeQuery(id+"F8.opPattern","COPY",FACE,{"derivedFrom":makeQuery(id+"F5.opPattern","COPY",FACE,{"derivedFrom":makeQuery(id+"F4.opRevolve","SWEPT_FACE",FACE,{"disambiguationData":[OSD([sQuery(id+"F3.wireOp",EDGE,"E18")])]}),"instanceName":"1"}),"instanceName":"2"})]})});
            var Q14;
            Q14=makeQuery(id+"F10.opBoolean","COPY",EDGE,{"derivedFrom":makeQuery(id+"F9.opBoolean","INTERSECT",EDGE,{"disambiguationData":[OD(0.0)],"derivedFrom":[makeQuery(id+"F8.opPattern","COPY",FACE,{"derivedFrom":makeQuery(id+"F4.opRevolve","SWEPT_FACE",FACE,{"disambiguationData":[OSD([sQuery(id+"F3.wireOp",EDGE,"E19.0")])]}),"instanceName":"1"}),makeQuery(id+"F8.opPattern","COPY",FACE,{"derivedFrom":makeQuery(id+"F4.opRevolve","SWEPT_FACE",FACE,{"disambiguationData":[OSD([sQuery(id+"F3.wireOp",EDGE,"E18")])]}),"instanceName":"2"})]})});
            var Q15;
            Q15=makeQuery(id+"F10.opBoolean","COPY",EDGE,{"derivedFrom":makeQuery(id+"F9.opBoolean","INTERSECT",EDGE,{"disambiguationData":[OD(0.0)],"derivedFrom":[makeQuery(id+"F8.opPattern","COPY",FACE,{"derivedFrom":makeQuery(id+"F4.opRevolve","SWEPT_FACE",FACE,{"disambiguationData":[OSD([sQuery(id+"F3.wireOp",EDGE,"E18")])]}),"instanceName":"1"}),makeQuery(id+"F8.opPattern","COPY",FACE,{"derivedFrom":makeQuery(id+"F4.opRevolve","SWEPT_FACE",FACE,{"disambiguationData":[OSD([sQuery(id+"F3.wireOp",EDGE,"E19.0")])]}),"instanceName":"2"})]})});
            var Q16;
            Q16=makeQuery(id+"F10.opBoolean","COPY",EDGE,{"derivedFrom":makeQuery(id+"F9.opBoolean","INTERSECT",EDGE,{"disambiguationData":[OD(1.0)],"derivedFrom":[makeQuery(id+"F4.opRevolve","SWEPT_FACE",FACE,{"disambiguationData":[OSD([sQuery(id+"F3.wireOp",EDGE,"E19.0")])]}),makeQuery(id+"F8.opPattern","COPY",FACE,{"derivedFrom":makeQuery(id+"F5.opPattern","COPY",FACE,{"derivedFrom":makeQuery(id+"F4.opRevolve","SWEPT_FACE",FACE,{"disambiguationData":[OSD([sQuery(id+"F3.wireOp",EDGE,"E18")])]}),"instanceName":"1"}),"instanceName":"1"})]})});
            var Q17;
            Q17=makeQuery(id+"F10.opBoolean","COPY",EDGE,{"derivedFrom":makeQuery(id+"F9.opBoolean","INTERSECT",EDGE,{"disambiguationData":[OD(1.0)],"derivedFrom":[makeQuery(id+"F4.opRevolve","SWEPT_FACE",FACE,{"disambiguationData":[OSD([sQuery(id+"F3.wireOp",EDGE,"E18")])]}),makeQuery(id+"F8.opPattern","COPY",FACE,{"derivedFrom":makeQuery(id+"F5.opPattern","COPY",FACE,{"derivedFrom":makeQuery(id+"F4.opRevolve","SWEPT_FACE",FACE,{"disambiguationData":[OSD([sQuery(id+"F3.wireOp",EDGE,"E19.0")])]}),"instanceName":"1"}),"instanceName":"1"})]})});
            var Q18;
            Q18=makeQuery(id+"F10.opBoolean","COPY",EDGE,{"derivedFrom":makeQuery(id+"F9.opBoolean","INTERSECT",EDGE,{"disambiguationData":[OD(1.0)],"derivedFrom":[makeQuery(id+"F4.opRevolve","SWEPT_FACE",FACE,{"disambiguationData":[OSD([sQuery(id+"F3.wireOp",EDGE,"E18")])]}),makeQuery(id+"F8.opPattern","COPY",FACE,{"derivedFrom":makeQuery(id+"F4.opRevolve","SWEPT_FACE",FACE,{"disambiguationData":[OSD([sQuery(id+"F3.wireOp",EDGE,"E19.0")])]}),"instanceName":"1"})]})});
            var Q19;
            Q19=makeQuery(id+"F10.opBoolean","COPY",EDGE,{"derivedFrom":makeQuery(id+"F9.opBoolean","INTERSECT",EDGE,{"disambiguationData":[OD(1.0)],"derivedFrom":[makeQuery(id+"F4.opRevolve","SWEPT_FACE",FACE,{"disambiguationData":[OSD([sQuery(id+"F3.wireOp",EDGE,"E19.0")])]}),makeQuery(id+"F8.opPattern","COPY",FACE,{"derivedFrom":makeQuery(id+"F4.opRevolve","SWEPT_FACE",FACE,{"disambiguationData":[OSD([sQuery(id+"F3.wireOp",EDGE,"E18")])]}),"instanceName":"1"})]})});
            var Q20;
            Q20=makeQuery(id+"F10.opBoolean","COPY",EDGE,{"derivedFrom":makeQuery(id+"F9.opBoolean","INTERSECT",EDGE,{"disambiguationData":[OD(1.0)],"derivedFrom":[makeQuery(id+"F5.opPattern","COPY",FACE,{"derivedFrom":makeQuery(id+"F4.opRevolve","SWEPT_FACE",FACE,{"disambiguationData":[OSD([sQuery(id+"F3.wireOp",EDGE,"E19.0")])]}),"instanceName":"1"}),makeQuery(id+"F8.opPattern","COPY",FACE,{"derivedFrom":makeQuery(id+"F4.opRevolve","SWEPT_FACE",FACE,{"disambiguationData":[OSD([sQuery(id+"F3.wireOp",EDGE,"E18")])]}),"instanceName":"1"})]})});
            var Q21;
            Q21=makeQuery(id+"F10.opBoolean","COPY",EDGE,{"derivedFrom":makeQuery(id+"F9.opBoolean","INTERSECT",EDGE,{"disambiguationData":[OD(1.0)],"derivedFrom":[makeQuery(id+"F5.opPattern","COPY",FACE,{"derivedFrom":makeQuery(id+"F4.opRevolve","SWEPT_FACE",FACE,{"disambiguationData":[OSD([sQuery(id+"F3.wireOp",EDGE,"E18")])]}),"instanceName":"1"}),makeQuery(id+"F8.opPattern","COPY",FACE,{"derivedFrom":makeQuery(id+"F4.opRevolve","SWEPT_FACE",FACE,{"disambiguationData":[OSD([sQuery(id+"F3.wireOp",EDGE,"E19.0")])]}),"instanceName":"1"})]})});
            var Q22;
            Q22=makeQuery(id+"F10.opBoolean","COPY",EDGE,{"derivedFrom":makeQuery(id+"F9.opBoolean","INTERSECT",EDGE,{"disambiguationData":[OD(1.0)],"derivedFrom":[makeQuery(id+"F5.opPattern","COPY",FACE,{"derivedFrom":makeQuery(id+"F4.opRevolve","SWEPT_FACE",FACE,{"disambiguationData":[OSD([sQuery(id+"F3.wireOp",EDGE,"E19.0")])]}),"instanceName":"1"}),makeQuery(id+"F8.opPattern","COPY",FACE,{"derivedFrom":makeQuery(id+"F5.opPattern","COPY",FACE,{"derivedFrom":makeQuery(id+"F4.opRevolve","SWEPT_FACE",FACE,{"disambiguationData":[OSD([sQuery(id+"F3.wireOp",EDGE,"E18")])]}),"instanceName":"1"}),"instanceName":"1"})]})});
            var Q23;
            Q23=makeQuery(id+"F10.opBoolean","COPY",EDGE,{"derivedFrom":makeQuery(id+"F9.opBoolean","INTERSECT",EDGE,{"disambiguationData":[OD(1.0)],"derivedFrom":[makeQuery(id+"F5.opPattern","COPY",FACE,{"derivedFrom":makeQuery(id+"F4.opRevolve","SWEPT_FACE",FACE,{"disambiguationData":[OSD([sQuery(id+"F3.wireOp",EDGE,"E18")])]}),"instanceName":"1"}),makeQuery(id+"F8.opPattern","COPY",FACE,{"derivedFrom":makeQuery(id+"F5.opPattern","COPY",FACE,{"derivedFrom":makeQuery(id+"F4.opRevolve","SWEPT_FACE",FACE,{"disambiguationData":[OSD([sQuery(id+"F3.wireOp",EDGE,"E19.0")])]}),"instanceName":"1"}),"instanceName":"1"})]})});
            fillet(context, id + "F14", {"entities" : qUnion([Q0, Q1, Q2, Q3, Q4, Q5, Q6, Q7, Q8, Q9, Q10, Q11, Q12, Q13, Q14, Q15, Q16, Q17, Q18, Q19, Q20, Q21, Q22, Q23]), "radius" : 2 * mm, "tangentPropagation" : true, "allowEdgeOverflow" : false});
        }
        {
            var Q0;
            Q0=makeQuery(id+"F10.opBoolean","COPY",EDGE,{"derivedFrom":makeQuery(id+"F9.opBoolean","INTERSECT",EDGE,{"disambiguationData":[OD(0.0)],"derivedFrom":[makeQuery(id+"F5.opPattern","COPY",FACE,{"derivedFrom":makeQuery(id+"F4.opRevolve","SWEPT_FACE",FACE,{"disambiguationData":[OSD([sQuery(id+"F3.wireOp",EDGE,"E19.1")])]}),"instanceName":"1"}),makeQuery(id+"F8.opPattern","COPY",FACE,{"derivedFrom":makeQuery(id+"F5.opPattern","COPY",FACE,{"derivedFrom":makeQuery(id+"F4.opRevolve","SWEPT_FACE",FACE,{"disambiguationData":[OSD([sQuery(id+"F3.wireOp",EDGE,"E18")])]}),"instanceName":"1"}),"instanceName":"2"})]})});
            var Q1;
            Q1=makeQuery(id+"F10.opBoolean","COPY",EDGE,{"derivedFrom":makeQuery(id+"F9.opBoolean","INTERSECT",EDGE,{"disambiguationData":[OD(0.0)],"derivedFrom":[makeQuery(id+"F5.opPattern","COPY",FACE,{"derivedFrom":makeQuery(id+"F4.opRevolve","SWEPT_FACE",FACE,{"disambiguationData":[OSD([sQuery(id+"F3.wireOp",EDGE,"E18")])]}),"instanceName":"1"}),makeQuery(id+"F8.opPattern","COPY",FACE,{"derivedFrom":makeQuery(id+"F5.opPattern","COPY",FACE,{"derivedFrom":makeQuery(id+"F4.opRevolve","SWEPT_FACE",FACE,{"disambiguationData":[OSD([sQuery(id+"F3.wireOp",EDGE,"E19.1")])]}),"instanceName":"1"}),"instanceName":"2"})]})});
            var Q2;
            Q2=makeQuery(id+"F10.opBoolean","COPY",EDGE,{"derivedFrom":makeQuery(id+"F9.opBoolean","INTERSECT",EDGE,{"disambiguationData":[OD(1.0)],"derivedFrom":[makeQuery(id+"F8.opPattern","COPY",FACE,{"derivedFrom":makeQuery(id+"F4.opRevolve","SWEPT_FACE",FACE,{"disambiguationData":[OSD([sQuery(id+"F3.wireOp",EDGE,"E19.1")])]}),"instanceName":"1"}),makeQuery(id+"F8.opPattern","COPY",FACE,{"derivedFrom":makeQuery(id+"F5.opPattern","COPY",FACE,{"derivedFrom":makeQuery(id+"F4.opRevolve","SWEPT_FACE",FACE,{"disambiguationData":[OSD([sQuery(id+"F3.wireOp",EDGE,"E18")])]}),"instanceName":"1"}),"instanceName":"2"})]})});
            var Q3;
            Q3=makeQuery(id+"F10.opBoolean","COPY",EDGE,{"derivedFrom":makeQuery(id+"F9.opBoolean","INTERSECT",EDGE,{"disambiguationData":[OD(1.0)],"derivedFrom":[makeQuery(id+"F8.opPattern","COPY",FACE,{"derivedFrom":makeQuery(id+"F4.opRevolve","SWEPT_FACE",FACE,{"disambiguationData":[OSD([sQuery(id+"F3.wireOp",EDGE,"E18")])]}),"instanceName":"1"}),makeQuery(id+"F8.opPattern","COPY",FACE,{"derivedFrom":makeQuery(id+"F5.opPattern","COPY",FACE,{"derivedFrom":makeQuery(id+"F4.opRevolve","SWEPT_FACE",FACE,{"disambiguationData":[OSD([sQuery(id+"F3.wireOp",EDGE,"E19.1")])]}),"instanceName":"1"}),"instanceName":"2"})]})});
            var Q4;
            Q4=makeQuery(id+"F10.opBoolean","COPY",EDGE,{"derivedFrom":makeQuery(id+"F9.opBoolean","INTERSECT",EDGE,{"disambiguationData":[OD(1.0)],"derivedFrom":[makeQuery(id+"F5.opPattern","COPY",FACE,{"derivedFrom":makeQuery(id+"F4.opRevolve","SWEPT_FACE",FACE,{"disambiguationData":[OSD([sQuery(id+"F3.wireOp",EDGE,"E19.1")])]}),"instanceName":"1"}),makeQuery(id+"F8.opPattern","COPY",FACE,{"derivedFrom":makeQuery(id+"F4.opRevolve","SWEPT_FACE",FACE,{"disambiguationData":[OSD([sQuery(id+"F3.wireOp",EDGE,"E18")])]}),"instanceName":"1"})]})});
            var Q5;
            Q5=makeQuery(id+"F10.opBoolean","COPY",EDGE,{"derivedFrom":makeQuery(id+"F9.opBoolean","INTERSECT",EDGE,{"disambiguationData":[OD(1.0)],"derivedFrom":[makeQuery(id+"F5.opPattern","COPY",FACE,{"derivedFrom":makeQuery(id+"F4.opRevolve","SWEPT_FACE",FACE,{"disambiguationData":[OSD([sQuery(id+"F3.wireOp",EDGE,"E18")])]}),"instanceName":"1"}),makeQuery(id+"F8.opPattern","COPY",FACE,{"derivedFrom":makeQuery(id+"F4.opRevolve","SWEPT_FACE",FACE,{"disambiguationData":[OSD([sQuery(id+"F3.wireOp",EDGE,"E19.1")])]}),"instanceName":"1"})]})});
            var Q6;
            Q6=makeQuery(id+"F10.opBoolean","COPY",EDGE,{"derivedFrom":makeQuery(id+"F9.opBoolean","INTERSECT",EDGE,{"disambiguationData":[OD(0.0)],"derivedFrom":[makeQuery(id+"F4.opRevolve","SWEPT_FACE",FACE,{"disambiguationData":[OSD([sQuery(id+"F3.wireOp",EDGE,"E19.1")])]}),makeQuery(id+"F8.opPattern","COPY",FACE,{"derivedFrom":makeQuery(id+"F5.opPattern","COPY",FACE,{"derivedFrom":makeQuery(id+"F4.opRevolve","SWEPT_FACE",FACE,{"disambiguationData":[OSD([sQuery(id+"F3.wireOp",EDGE,"E18")])]}),"instanceName":"1"}),"instanceName":"2"})]})});
            var Q7;
            Q7=makeQuery(id+"F10.opBoolean","COPY",EDGE,{"derivedFrom":makeQuery(id+"F9.opBoolean","INTERSECT",EDGE,{"disambiguationData":[OD(0.0)],"derivedFrom":[makeQuery(id+"F8.opPattern","COPY",FACE,{"derivedFrom":makeQuery(id+"F4.opRevolve","SWEPT_FACE",FACE,{"disambiguationData":[OSD([sQuery(id+"F3.wireOp",EDGE,"E19.1")])]}),"instanceName":"1"}),makeQuery(id+"F8.opPattern","COPY",FACE,{"derivedFrom":makeQuery(id+"F5.opPattern","COPY",FACE,{"derivedFrom":makeQuery(id+"F4.opRevolve","SWEPT_FACE",FACE,{"disambiguationData":[OSD([sQuery(id+"F3.wireOp",EDGE,"E18")])]}),"instanceName":"1"}),"instanceName":"2"})]})});
            var Q8;
            Q8=makeQuery(id+"F10.opBoolean","COPY",EDGE,{"derivedFrom":makeQuery(id+"F9.opBoolean","INTERSECT",EDGE,{"disambiguationData":[OD(0.0)],"derivedFrom":[makeQuery(id+"F8.opPattern","COPY",FACE,{"derivedFrom":makeQuery(id+"F4.opRevolve","SWEPT_FACE",FACE,{"disambiguationData":[OSD([sQuery(id+"F3.wireOp",EDGE,"E18")])]}),"instanceName":"1"}),makeQuery(id+"F8.opPattern","COPY",FACE,{"derivedFrom":makeQuery(id+"F5.opPattern","COPY",FACE,{"derivedFrom":makeQuery(id+"F4.opRevolve","SWEPT_FACE",FACE,{"disambiguationData":[OSD([sQuery(id+"F3.wireOp",EDGE,"E19.1")])]}),"instanceName":"1"}),"instanceName":"2"})]})});
            var Q9;
            Q9=makeQuery(id+"F10.opBoolean","COPY",EDGE,{"derivedFrom":makeQuery(id+"F9.opBoolean","INTERSECT",EDGE,{"disambiguationData":[OD(1.0)],"derivedFrom":[makeQuery(id+"F4.opRevolve","SWEPT_FACE",FACE,{"disambiguationData":[OSD([sQuery(id+"F3.wireOp",EDGE,"E19.1")])]}),makeQuery(id+"F8.opPattern","COPY",FACE,{"derivedFrom":makeQuery(id+"F4.opRevolve","SWEPT_FACE",FACE,{"disambiguationData":[OSD([sQuery(id+"F3.wireOp",EDGE,"E18")])]}),"instanceName":"1"})]})});
            var Q10;
            Q10=makeQuery(id+"F10.opBoolean","COPY",EDGE,{"derivedFrom":makeQuery(id+"F9.opBoolean","INTERSECT",EDGE,{"disambiguationData":[OD(0.0)],"derivedFrom":[makeQuery(id+"F4.opRevolve","SWEPT_FACE",FACE,{"disambiguationData":[OSD([sQuery(id+"F3.wireOp",EDGE,"E18")])]}),makeQuery(id+"F8.opPattern","COPY",FACE,{"derivedFrom":makeQuery(id+"F5.opPattern","COPY",FACE,{"derivedFrom":makeQuery(id+"F4.opRevolve","SWEPT_FACE",FACE,{"disambiguationData":[OSD([sQuery(id+"F3.wireOp",EDGE,"E19.1")])]}),"instanceName":"1"}),"instanceName":"2"})]})});
            var Q11;
            Q11=makeQuery(id+"F10.opBoolean","COPY",EDGE,{"derivedFrom":makeQuery(id+"F9.opBoolean","INTERSECT",EDGE,{"disambiguationData":[OD(1.0)],"derivedFrom":[makeQuery(id+"F4.opRevolve","SWEPT_FACE",FACE,{"disambiguationData":[OSD([sQuery(id+"F3.wireOp",EDGE,"E18")])]}),makeQuery(id+"F8.opPattern","COPY",FACE,{"derivedFrom":makeQuery(id+"F4.opRevolve","SWEPT_FACE",FACE,{"disambiguationData":[OSD([sQuery(id+"F3.wireOp",EDGE,"E19.1")])]}),"instanceName":"1"})]})});
            var Q12;
            Q12=makeQuery(id+"F10.opBoolean","COPY",EDGE,{"derivedFrom":makeQuery(id+"F9.opBoolean","INTERSECT",EDGE,{"disambiguationData":[OD(1.0)],"derivedFrom":[makeQuery(id+"F4.opRevolve","SWEPT_FACE",FACE,{"disambiguationData":[OSD([sQuery(id+"F3.wireOp",EDGE,"E18")])]}),makeQuery(id+"F8.opPattern","COPY",FACE,{"derivedFrom":makeQuery(id+"F5.opPattern","COPY",FACE,{"derivedFrom":makeQuery(id+"F4.opRevolve","SWEPT_FACE",FACE,{"disambiguationData":[OSD([sQuery(id+"F3.wireOp",EDGE,"E19.1")])]}),"instanceName":"1"}),"instanceName":"1"})]})});
            var Q13;
            Q13=makeQuery(id+"F10.opBoolean","COPY",EDGE,{"derivedFrom":makeQuery(id+"F9.opBoolean","INTERSECT",EDGE,{"disambiguationData":[OD(1.0)],"derivedFrom":[makeQuery(id+"F4.opRevolve","SWEPT_FACE",FACE,{"disambiguationData":[OSD([sQuery(id+"F3.wireOp",EDGE,"E18")])]}),makeQuery(id+"F8.opPattern","COPY",FACE,{"derivedFrom":makeQuery(id+"F5.opPattern","COPY",FACE,{"derivedFrom":makeQuery(id+"F4.opRevolve","SWEPT_FACE",FACE,{"disambiguationData":[OSD([sQuery(id+"F3.wireOp",EDGE,"E19.1")])]}),"instanceName":"1"}),"instanceName":"2"})]})});
            var Q14;
            Q14=makeQuery(id+"F10.opBoolean","COPY",EDGE,{"derivedFrom":makeQuery(id+"F9.opBoolean","INTERSECT",EDGE,{"disambiguationData":[OD(1.0)],"derivedFrom":[makeQuery(id+"F4.opRevolve","SWEPT_FACE",FACE,{"disambiguationData":[OSD([sQuery(id+"F3.wireOp",EDGE,"E19.1")])]}),makeQuery(id+"F8.opPattern","COPY",FACE,{"derivedFrom":makeQuery(id+"F5.opPattern","COPY",FACE,{"derivedFrom":makeQuery(id+"F4.opRevolve","SWEPT_FACE",FACE,{"disambiguationData":[OSD([sQuery(id+"F3.wireOp",EDGE,"E18")])]}),"instanceName":"1"}),"instanceName":"2"})]})});
            var Q15;
            Q15=makeQuery(id+"F10.opBoolean","COPY",EDGE,{"derivedFrom":makeQuery(id+"F9.opBoolean","INTERSECT",EDGE,{"disambiguationData":[OD(0.0)],"derivedFrom":[makeQuery(id+"F8.opPattern","COPY",FACE,{"derivedFrom":makeQuery(id+"F5.opPattern","COPY",FACE,{"derivedFrom":makeQuery(id+"F4.opRevolve","SWEPT_FACE",FACE,{"disambiguationData":[OSD([sQuery(id+"F3.wireOp",EDGE,"E19.1")])]}),"instanceName":"1"}),"instanceName":"1"}),makeQuery(id+"F8.opPattern","COPY",FACE,{"derivedFrom":makeQuery(id+"F5.opPattern","COPY",FACE,{"derivedFrom":makeQuery(id+"F4.opRevolve","SWEPT_FACE",FACE,{"disambiguationData":[OSD([sQuery(id+"F3.wireOp",EDGE,"E18")])]}),"instanceName":"1"}),"instanceName":"2"})]})});
            var Q16;
            Q16=makeQuery(id+"F10.opBoolean","COPY",EDGE,{"derivedFrom":makeQuery(id+"F9.opBoolean","INTERSECT",EDGE,{"disambiguationData":[OD(0.0)],"derivedFrom":[makeQuery(id+"F8.opPattern","COPY",FACE,{"derivedFrom":makeQuery(id+"F5.opPattern","COPY",FACE,{"derivedFrom":makeQuery(id+"F4.opRevolve","SWEPT_FACE",FACE,{"disambiguationData":[OSD([sQuery(id+"F3.wireOp",EDGE,"E18")])]}),"instanceName":"1"}),"instanceName":"1"}),makeQuery(id+"F8.opPattern","COPY",FACE,{"derivedFrom":makeQuery(id+"F5.opPattern","COPY",FACE,{"derivedFrom":makeQuery(id+"F4.opRevolve","SWEPT_FACE",FACE,{"disambiguationData":[OSD([sQuery(id+"F3.wireOp",EDGE,"E19.1")])]}),"instanceName":"1"}),"instanceName":"2"})]})});
            var Q17;
            Q17=makeQuery(id+"F10.opBoolean","COPY",EDGE,{"derivedFrom":makeQuery(id+"F9.opBoolean","INTERSECT",EDGE,{"disambiguationData":[OD(1.0)],"derivedFrom":[makeQuery(id+"F4.opRevolve","SWEPT_FACE",FACE,{"disambiguationData":[OSD([sQuery(id+"F3.wireOp",EDGE,"E19.1")])]}),makeQuery(id+"F8.opPattern","COPY",FACE,{"derivedFrom":makeQuery(id+"F5.opPattern","COPY",FACE,{"derivedFrom":makeQuery(id+"F4.opRevolve","SWEPT_FACE",FACE,{"disambiguationData":[OSD([sQuery(id+"F3.wireOp",EDGE,"E18")])]}),"instanceName":"1"}),"instanceName":"1"})]})});
            var Q18;
            Q18=makeQuery(id+"F10.opBoolean","COPY",EDGE,{"derivedFrom":makeQuery(id+"F9.opBoolean","INTERSECT",EDGE,{"disambiguationData":[OD(1.0)],"derivedFrom":[makeQuery(id+"F5.opPattern","COPY",FACE,{"derivedFrom":makeQuery(id+"F4.opRevolve","SWEPT_FACE",FACE,{"disambiguationData":[OSD([sQuery(id+"F3.wireOp",EDGE,"E18")])]}),"instanceName":"1"}),makeQuery(id+"F8.opPattern","COPY",FACE,{"derivedFrom":makeQuery(id+"F5.opPattern","COPY",FACE,{"derivedFrom":makeQuery(id+"F4.opRevolve","SWEPT_FACE",FACE,{"disambiguationData":[OSD([sQuery(id+"F3.wireOp",EDGE,"E19.1")])]}),"instanceName":"1"}),"instanceName":"2"})]})});
            var Q19;
            Q19=makeQuery(id+"F10.opBoolean","COPY",EDGE,{"derivedFrom":makeQuery(id+"F9.opBoolean","INTERSECT",EDGE,{"disambiguationData":[OD(1.0)],"derivedFrom":[makeQuery(id+"F5.opPattern","COPY",FACE,{"derivedFrom":makeQuery(id+"F4.opRevolve","SWEPT_FACE",FACE,{"disambiguationData":[OSD([sQuery(id+"F3.wireOp",EDGE,"E19.1")])]}),"instanceName":"1"}),makeQuery(id+"F8.opPattern","COPY",FACE,{"derivedFrom":makeQuery(id+"F5.opPattern","COPY",FACE,{"derivedFrom":makeQuery(id+"F4.opRevolve","SWEPT_FACE",FACE,{"disambiguationData":[OSD([sQuery(id+"F3.wireOp",EDGE,"E18")])]}),"instanceName":"1"}),"instanceName":"2"})]})});
            var Q20;
            Q20=makeQuery(id+"F10.opBoolean","COPY",EDGE,{"derivedFrom":makeQuery(id+"F9.opBoolean","INTERSECT",EDGE,{"disambiguationData":[OD(1.0)],"derivedFrom":[makeQuery(id+"F5.opPattern","COPY",FACE,{"derivedFrom":makeQuery(id+"F4.opRevolve","SWEPT_FACE",FACE,{"disambiguationData":[OSD([sQuery(id+"F3.wireOp",EDGE,"E18")])]}),"instanceName":"1"}),makeQuery(id+"F8.opPattern","COPY",FACE,{"derivedFrom":makeQuery(id+"F5.opPattern","COPY",FACE,{"derivedFrom":makeQuery(id+"F4.opRevolve","SWEPT_FACE",FACE,{"disambiguationData":[OSD([sQuery(id+"F3.wireOp",EDGE,"E19.1")])]}),"instanceName":"1"}),"instanceName":"1"})]})});
            var Q21;
            Q21=makeQuery(id+"F10.opBoolean","COPY",EDGE,{"derivedFrom":makeQuery(id+"F9.opBoolean","INTERSECT",EDGE,{"disambiguationData":[OD(1.0)],"derivedFrom":[makeQuery(id+"F5.opPattern","COPY",FACE,{"derivedFrom":makeQuery(id+"F4.opRevolve","SWEPT_FACE",FACE,{"disambiguationData":[OSD([sQuery(id+"F3.wireOp",EDGE,"E19.1")])]}),"instanceName":"1"}),makeQuery(id+"F8.opPattern","COPY",FACE,{"derivedFrom":makeQuery(id+"F5.opPattern","COPY",FACE,{"derivedFrom":makeQuery(id+"F4.opRevolve","SWEPT_FACE",FACE,{"disambiguationData":[OSD([sQuery(id+"F3.wireOp",EDGE,"E18")])]}),"instanceName":"1"}),"instanceName":"1"})]})});
            var Q22;
            Q22=makeQuery(id+"F10.opBoolean","COPY",EDGE,{"derivedFrom":makeQuery(id+"F9.opBoolean","INTERSECT",EDGE,{"disambiguationData":[OD(1.0)],"derivedFrom":[makeQuery(id+"F8.opPattern","COPY",FACE,{"derivedFrom":makeQuery(id+"F5.opPattern","COPY",FACE,{"derivedFrom":makeQuery(id+"F4.opRevolve","SWEPT_FACE",FACE,{"disambiguationData":[OSD([sQuery(id+"F3.wireOp",EDGE,"E18")])]}),"instanceName":"1"}),"instanceName":"1"}),makeQuery(id+"F8.opPattern","COPY",FACE,{"derivedFrom":makeQuery(id+"F5.opPattern","COPY",FACE,{"derivedFrom":makeQuery(id+"F4.opRevolve","SWEPT_FACE",FACE,{"disambiguationData":[OSD([sQuery(id+"F3.wireOp",EDGE,"E19.1")])]}),"instanceName":"1"}),"instanceName":"2"})]})});
            var Q23;
            Q23=makeQuery(id+"F10.opBoolean","COPY",EDGE,{"derivedFrom":makeQuery(id+"F9.opBoolean","INTERSECT",EDGE,{"disambiguationData":[OD(1.0)],"derivedFrom":[makeQuery(id+"F8.opPattern","COPY",FACE,{"derivedFrom":makeQuery(id+"F5.opPattern","COPY",FACE,{"derivedFrom":makeQuery(id+"F4.opRevolve","SWEPT_FACE",FACE,{"disambiguationData":[OSD([sQuery(id+"F3.wireOp",EDGE,"E19.1")])]}),"instanceName":"1"}),"instanceName":"1"}),makeQuery(id+"F8.opPattern","COPY",FACE,{"derivedFrom":makeQuery(id+"F5.opPattern","COPY",FACE,{"derivedFrom":makeQuery(id+"F4.opRevolve","SWEPT_FACE",FACE,{"disambiguationData":[OSD([sQuery(id+"F3.wireOp",EDGE,"E18")])]}),"instanceName":"1"}),"instanceName":"2"})]})});
            fillet(context, id + "F15", {"entities" : qUnion([Q0, Q1, Q2, Q3, Q4, Q5, Q6, Q7, Q8, Q9, Q10, Q11, Q12, Q13, Q14, Q15, Q16, Q17, Q18, Q19, Q20, Q21, Q22, Q23]), "radius" : 1 * mm, "tangentPropagation" : true, "allowEdgeOverflow" : false});
        }
        {
            var Q0;
            Q0=makeQuery(id+"F10.opBoolean","COPY",EDGE,{"derivedFrom":makeQuery(id+"F9.opBoolean","INTERSECT",EDGE,{"disambiguationData":[OD(0.0)],"derivedFrom":[makeQuery(id+"F5.opPattern","COPY",FACE,{"derivedFrom":makeQuery(id+"F4.opRevolve","SWEPT_FACE",FACE,{"disambiguationData":[OSD([sQuery(id+"F3.wireOp",EDGE,"E18")])]}),"instanceName":"1"}),makeQuery(id+"F8.opPattern","COPY",FACE,{"derivedFrom":makeQuery(id+"F5.opPattern","COPY",FACE,{"derivedFrom":makeQuery(id+"F4.opRevolve","SWEPT_FACE",FACE,{"disambiguationData":[OSD([sQuery(id+"F3.wireOp",EDGE,"E19.1")])]}),"instanceName":"1"}),"instanceName":"1"})]})});
            var Q1;
            Q1=makeQuery(id+"F10.opBoolean","COPY",EDGE,{"derivedFrom":makeQuery(id+"F9.opBoolean","INTERSECT",EDGE,{"disambiguationData":[OD(0.0)],"derivedFrom":[makeQuery(id+"F5.opPattern","COPY",FACE,{"derivedFrom":makeQuery(id+"F4.opRevolve","SWEPT_FACE",FACE,{"disambiguationData":[OSD([sQuery(id+"F3.wireOp",EDGE,"E19.1")])]}),"instanceName":"1"}),makeQuery(id+"F8.opPattern","COPY",FACE,{"derivedFrom":makeQuery(id+"F5.opPattern","COPY",FACE,{"derivedFrom":makeQuery(id+"F4.opRevolve","SWEPT_FACE",FACE,{"disambiguationData":[OSD([sQuery(id+"F3.wireOp",EDGE,"E18")])]}),"instanceName":"1"}),"instanceName":"1"})]})});
            var Q2;
            Q2=makeQuery(id+"F10.opBoolean","COPY",EDGE,{"derivedFrom":makeQuery(id+"F9.opBoolean","INTERSECT",EDGE,{"disambiguationData":[OD(1.0)],"derivedFrom":[makeQuery(id+"F8.opPattern","COPY",FACE,{"derivedFrom":makeQuery(id+"F5.opPattern","COPY",FACE,{"derivedFrom":makeQuery(id+"F4.opRevolve","SWEPT_FACE",FACE,{"disambiguationData":[OSD([sQuery(id+"F3.wireOp",EDGE,"E18")])]}),"instanceName":"1"}),"instanceName":"1"}),makeQuery(id+"F8.opPattern","COPY",FACE,{"derivedFrom":makeQuery(id+"F4.opRevolve","SWEPT_FACE",FACE,{"disambiguationData":[OSD([sQuery(id+"F3.wireOp",EDGE,"E19.1")])]}),"instanceName":"2"})]})});
            var Q3;
            Q3=makeQuery(id+"F10.opBoolean","COPY",EDGE,{"derivedFrom":makeQuery(id+"F9.opBoolean","INTERSECT",EDGE,{"disambiguationData":[OD(1.0)],"derivedFrom":[makeQuery(id+"F8.opPattern","COPY",FACE,{"derivedFrom":makeQuery(id+"F5.opPattern","COPY",FACE,{"derivedFrom":makeQuery(id+"F4.opRevolve","SWEPT_FACE",FACE,{"disambiguationData":[OSD([sQuery(id+"F3.wireOp",EDGE,"E19.1")])]}),"instanceName":"1"}),"instanceName":"1"}),makeQuery(id+"F8.opPattern","COPY",FACE,{"derivedFrom":makeQuery(id+"F4.opRevolve","SWEPT_FACE",FACE,{"disambiguationData":[OSD([sQuery(id+"F3.wireOp",EDGE,"E18")])]}),"instanceName":"2"})]})});
            var Q4;
            Q4=makeQuery(id+"F10.opBoolean","COPY",EDGE,{"derivedFrom":makeQuery(id+"F9.opBoolean","INTERSECT",EDGE,{"disambiguationData":[OD(1.0)],"derivedFrom":[makeQuery(id+"F5.opPattern","COPY",FACE,{"derivedFrom":makeQuery(id+"F4.opRevolve","SWEPT_FACE",FACE,{"disambiguationData":[OSD([sQuery(id+"F3.wireOp",EDGE,"E19.1")])]}),"instanceName":"1"}),makeQuery(id+"F8.opPattern","COPY",FACE,{"derivedFrom":makeQuery(id+"F4.opRevolve","SWEPT_FACE",FACE,{"disambiguationData":[OSD([sQuery(id+"F3.wireOp",EDGE,"E18")])]}),"instanceName":"2"})]})});
            var Q5;
            Q5=makeQuery(id+"F10.opBoolean","COPY",EDGE,{"derivedFrom":makeQuery(id+"F9.opBoolean","INTERSECT",EDGE,{"disambiguationData":[OD(1.0)],"derivedFrom":[makeQuery(id+"F5.opPattern","COPY",FACE,{"derivedFrom":makeQuery(id+"F4.opRevolve","SWEPT_FACE",FACE,{"disambiguationData":[OSD([sQuery(id+"F3.wireOp",EDGE,"E18")])]}),"instanceName":"1"}),makeQuery(id+"F8.opPattern","COPY",FACE,{"derivedFrom":makeQuery(id+"F4.opRevolve","SWEPT_FACE",FACE,{"disambiguationData":[OSD([sQuery(id+"F3.wireOp",EDGE,"E19.1")])]}),"instanceName":"2"})]})});
            var Q6;
            Q6=makeQuery(id+"F10.opBoolean","COPY",EDGE,{"derivedFrom":makeQuery(id+"F9.opBoolean","INTERSECT",EDGE,{"disambiguationData":[OD(1.0)],"derivedFrom":[makeQuery(id+"F4.opRevolve","SWEPT_FACE",FACE,{"disambiguationData":[OSD([sQuery(id+"F3.wireOp",EDGE,"E18")])]}),makeQuery(id+"F8.opPattern","COPY",FACE,{"derivedFrom":makeQuery(id+"F4.opRevolve","SWEPT_FACE",FACE,{"disambiguationData":[OSD([sQuery(id+"F3.wireOp",EDGE,"E19.1")])]}),"instanceName":"2"})]})});
            var Q7;
            Q7=makeQuery(id+"F10.opBoolean","COPY",EDGE,{"derivedFrom":makeQuery(id+"F9.opBoolean","INTERSECT",EDGE,{"disambiguationData":[OD(1.0)],"derivedFrom":[makeQuery(id+"F4.opRevolve","SWEPT_FACE",FACE,{"disambiguationData":[OSD([sQuery(id+"F3.wireOp",EDGE,"E19.1")])]}),makeQuery(id+"F8.opPattern","COPY",FACE,{"derivedFrom":makeQuery(id+"F4.opRevolve","SWEPT_FACE",FACE,{"disambiguationData":[OSD([sQuery(id+"F3.wireOp",EDGE,"E18")])]}),"instanceName":"2"})]})});
            var Q8;
            Q8=makeQuery(id+"F10.opBoolean","COPY",EDGE,{"derivedFrom":makeQuery(id+"F9.opBoolean","INTERSECT",EDGE,{"disambiguationData":[OD(0.0)],"derivedFrom":[makeQuery(id+"F8.opPattern","COPY",FACE,{"derivedFrom":makeQuery(id+"F5.opPattern","COPY",FACE,{"derivedFrom":makeQuery(id+"F4.opRevolve","SWEPT_FACE",FACE,{"disambiguationData":[OSD([sQuery(id+"F3.wireOp",EDGE,"E19.1")])]}),"instanceName":"1"}),"instanceName":"1"}),makeQuery(id+"F8.opPattern","COPY",FACE,{"derivedFrom":makeQuery(id+"F4.opRevolve","SWEPT_FACE",FACE,{"disambiguationData":[OSD([sQuery(id+"F3.wireOp",EDGE,"E18")])]}),"instanceName":"2"})]})});
            var Q9;
            Q9=makeQuery(id+"F10.opBoolean","COPY",EDGE,{"derivedFrom":makeQuery(id+"F9.opBoolean","INTERSECT",EDGE,{"disambiguationData":[OD(0.0)],"derivedFrom":[makeQuery(id+"F8.opPattern","COPY",FACE,{"derivedFrom":makeQuery(id+"F5.opPattern","COPY",FACE,{"derivedFrom":makeQuery(id+"F4.opRevolve","SWEPT_FACE",FACE,{"disambiguationData":[OSD([sQuery(id+"F3.wireOp",EDGE,"E18")])]}),"instanceName":"1"}),"instanceName":"1"}),makeQuery(id+"F8.opPattern","COPY",FACE,{"derivedFrom":makeQuery(id+"F4.opRevolve","SWEPT_FACE",FACE,{"disambiguationData":[OSD([sQuery(id+"F3.wireOp",EDGE,"E19.1")])]}),"instanceName":"2"})]})});
            var Q10;
            Q10=makeQuery(id+"F10.opBoolean","COPY",EDGE,{"derivedFrom":makeQuery(id+"F9.opBoolean","INTERSECT",EDGE,{"disambiguationData":[OD(0.0)],"derivedFrom":[makeQuery(id+"F4.opRevolve","SWEPT_FACE",FACE,{"disambiguationData":[OSD([sQuery(id+"F3.wireOp",EDGE,"E19.1")])]}),makeQuery(id+"F8.opPattern","COPY",FACE,{"derivedFrom":makeQuery(id+"F5.opPattern","COPY",FACE,{"derivedFrom":makeQuery(id+"F4.opRevolve","SWEPT_FACE",FACE,{"disambiguationData":[OSD([sQuery(id+"F3.wireOp",EDGE,"E18")])]}),"instanceName":"1"}),"instanceName":"1"})]})});
            var Q11;
            Q11=makeQuery(id+"F10.opBoolean","COPY",EDGE,{"derivedFrom":makeQuery(id+"F9.opBoolean","INTERSECT",EDGE,{"disambiguationData":[OD(0.0)],"derivedFrom":[makeQuery(id+"F4.opRevolve","SWEPT_FACE",FACE,{"disambiguationData":[OSD([sQuery(id+"F3.wireOp",EDGE,"E18")])]}),makeQuery(id+"F8.opPattern","COPY",FACE,{"derivedFrom":makeQuery(id+"F5.opPattern","COPY",FACE,{"derivedFrom":makeQuery(id+"F4.opRevolve","SWEPT_FACE",FACE,{"disambiguationData":[OSD([sQuery(id+"F3.wireOp",EDGE,"E19.1")])]}),"instanceName":"1"}),"instanceName":"1"})]})});
            var Q12;
            Q12=makeQuery(id+"F10.opBoolean","COPY",EDGE,{"derivedFrom":makeQuery(id+"F9.opBoolean","INTERSECT",EDGE,{"disambiguationData":[OD(0.0)],"derivedFrom":[makeQuery(id+"F4.opRevolve","SWEPT_FACE",FACE,{"disambiguationData":[OSD([sQuery(id+"F3.wireOp",EDGE,"E19.1")])]}),makeQuery(id+"F8.opPattern","COPY",FACE,{"derivedFrom":makeQuery(id+"F4.opRevolve","SWEPT_FACE",FACE,{"disambiguationData":[OSD([sQuery(id+"F3.wireOp",EDGE,"E18")])]}),"instanceName":"1"})]})});
            var Q13;
            Q13=makeQuery(id+"F10.opBoolean","COPY",EDGE,{"derivedFrom":makeQuery(id+"F9.opBoolean","INTERSECT",EDGE,{"disambiguationData":[OD(0.0)],"derivedFrom":[makeQuery(id+"F4.opRevolve","SWEPT_FACE",FACE,{"disambiguationData":[OSD([sQuery(id+"F3.wireOp",EDGE,"E18")])]}),makeQuery(id+"F8.opPattern","COPY",FACE,{"derivedFrom":makeQuery(id+"F4.opRevolve","SWEPT_FACE",FACE,{"disambiguationData":[OSD([sQuery(id+"F3.wireOp",EDGE,"E19.1")])]}),"instanceName":"1"})]})});
            var Q14;
            Q14=makeQuery(id+"F10.opBoolean","COPY",EDGE,{"derivedFrom":makeQuery(id+"F9.opBoolean","INTERSECT",EDGE,{"disambiguationData":[OD(0.0)],"derivedFrom":[makeQuery(id+"F4.opRevolve","SWEPT_FACE",FACE,{"disambiguationData":[OSD([sQuery(id+"F3.wireOp",EDGE,"E18")])]}),makeQuery(id+"F8.opPattern","COPY",FACE,{"derivedFrom":makeQuery(id+"F4.opRevolve","SWEPT_FACE",FACE,{"disambiguationData":[OSD([sQuery(id+"F3.wireOp",EDGE,"E19.1")])]}),"instanceName":"2"})]})});
            var Q15;
            Q15=makeQuery(id+"F10.opBoolean","COPY",EDGE,{"derivedFrom":makeQuery(id+"F9.opBoolean","INTERSECT",EDGE,{"disambiguationData":[OD(0.0)],"derivedFrom":[makeQuery(id+"F4.opRevolve","SWEPT_FACE",FACE,{"disambiguationData":[OSD([sQuery(id+"F3.wireOp",EDGE,"E19.1")])]}),makeQuery(id+"F8.opPattern","COPY",FACE,{"derivedFrom":makeQuery(id+"F4.opRevolve","SWEPT_FACE",FACE,{"disambiguationData":[OSD([sQuery(id+"F3.wireOp",EDGE,"E18")])]}),"instanceName":"2"})]})});
            var Q16;
            Q16=makeQuery(id+"F10.opBoolean","COPY",EDGE,{"derivedFrom":makeQuery(id+"F9.opBoolean","INTERSECT",EDGE,{"disambiguationData":[OD(0.0)],"derivedFrom":[makeQuery(id+"F8.opPattern","COPY",FACE,{"derivedFrom":makeQuery(id+"F4.opRevolve","SWEPT_FACE",FACE,{"disambiguationData":[OSD([sQuery(id+"F3.wireOp",EDGE,"E19.1")])]}),"instanceName":"1"}),makeQuery(id+"F8.opPattern","COPY",FACE,{"derivedFrom":makeQuery(id+"F4.opRevolve","SWEPT_FACE",FACE,{"disambiguationData":[OSD([sQuery(id+"F3.wireOp",EDGE,"E18")])]}),"instanceName":"2"})]})});
            var Q17;
            Q17=makeQuery(id+"F10.opBoolean","COPY",EDGE,{"derivedFrom":makeQuery(id+"F9.opBoolean","INTERSECT",EDGE,{"disambiguationData":[OD(0.0)],"derivedFrom":[makeQuery(id+"F8.opPattern","COPY",FACE,{"derivedFrom":makeQuery(id+"F4.opRevolve","SWEPT_FACE",FACE,{"disambiguationData":[OSD([sQuery(id+"F3.wireOp",EDGE,"E18")])]}),"instanceName":"1"}),makeQuery(id+"F8.opPattern","COPY",FACE,{"derivedFrom":makeQuery(id+"F4.opRevolve","SWEPT_FACE",FACE,{"disambiguationData":[OSD([sQuery(id+"F3.wireOp",EDGE,"E19.1")])]}),"instanceName":"2"})]})});
            var Q18;
            Q18=makeQuery(id+"F10.opBoolean","COPY",EDGE,{"derivedFrom":makeQuery(id+"F9.opBoolean","INTERSECT",EDGE,{"disambiguationData":[OD(0.0)],"derivedFrom":[makeQuery(id+"F5.opPattern","COPY",FACE,{"derivedFrom":makeQuery(id+"F4.opRevolve","SWEPT_FACE",FACE,{"disambiguationData":[OSD([sQuery(id+"F3.wireOp",EDGE,"E19.1")])]}),"instanceName":"1"}),makeQuery(id+"F8.opPattern","COPY",FACE,{"derivedFrom":makeQuery(id+"F4.opRevolve","SWEPT_FACE",FACE,{"disambiguationData":[OSD([sQuery(id+"F3.wireOp",EDGE,"E18")])]}),"instanceName":"1"})]})});
            var Q19;
            Q19=makeQuery(id+"F10.opBoolean","COPY",EDGE,{"derivedFrom":makeQuery(id+"F9.opBoolean","INTERSECT",EDGE,{"disambiguationData":[OD(1.0)],"derivedFrom":[makeQuery(id+"F8.opPattern","COPY",FACE,{"derivedFrom":makeQuery(id+"F4.opRevolve","SWEPT_FACE",FACE,{"disambiguationData":[OSD([sQuery(id+"F3.wireOp",EDGE,"E18")])]}),"instanceName":"1"}),makeQuery(id+"F8.opPattern","COPY",FACE,{"derivedFrom":makeQuery(id+"F4.opRevolve","SWEPT_FACE",FACE,{"disambiguationData":[OSD([sQuery(id+"F3.wireOp",EDGE,"E19.1")])]}),"instanceName":"2"})]})});
            var Q20;
            Q20=makeQuery(id+"F10.opBoolean","COPY",EDGE,{"derivedFrom":makeQuery(id+"F9.opBoolean","INTERSECT",EDGE,{"disambiguationData":[OD(1.0)],"derivedFrom":[makeQuery(id+"F8.opPattern","COPY",FACE,{"derivedFrom":makeQuery(id+"F4.opRevolve","SWEPT_FACE",FACE,{"disambiguationData":[OSD([sQuery(id+"F3.wireOp",EDGE,"E19.1")])]}),"instanceName":"1"}),makeQuery(id+"F8.opPattern","COPY",FACE,{"derivedFrom":makeQuery(id+"F4.opRevolve","SWEPT_FACE",FACE,{"disambiguationData":[OSD([sQuery(id+"F3.wireOp",EDGE,"E18")])]}),"instanceName":"2"})]})});
            var Q21;
            Q21=makeQuery(id+"F10.opBoolean","COPY",EDGE,{"derivedFrom":makeQuery(id+"F9.opBoolean","INTERSECT",EDGE,{"disambiguationData":[OD(0.0)],"derivedFrom":[makeQuery(id+"F5.opPattern","COPY",FACE,{"derivedFrom":makeQuery(id+"F4.opRevolve","SWEPT_FACE",FACE,{"disambiguationData":[OSD([sQuery(id+"F3.wireOp",EDGE,"E19.1")])]}),"instanceName":"1"}),makeQuery(id+"F8.opPattern","COPY",FACE,{"derivedFrom":makeQuery(id+"F4.opRevolve","SWEPT_FACE",FACE,{"disambiguationData":[OSD([sQuery(id+"F3.wireOp",EDGE,"E18")])]}),"instanceName":"2"})]})});
            var Q22;
            Q22=makeQuery(id+"F10.opBoolean","COPY",EDGE,{"derivedFrom":makeQuery(id+"F9.opBoolean","INTERSECT",EDGE,{"disambiguationData":[OD(0.0)],"derivedFrom":[makeQuery(id+"F5.opPattern","COPY",FACE,{"derivedFrom":makeQuery(id+"F4.opRevolve","SWEPT_FACE",FACE,{"disambiguationData":[OSD([sQuery(id+"F3.wireOp",EDGE,"E18")])]}),"instanceName":"1"}),makeQuery(id+"F8.opPattern","COPY",FACE,{"derivedFrom":makeQuery(id+"F4.opRevolve","SWEPT_FACE",FACE,{"disambiguationData":[OSD([sQuery(id+"F3.wireOp",EDGE,"E19.1")])]}),"instanceName":"2"})]})});
            var Q23;
            Q23=makeQuery(id+"F10.opBoolean","COPY",EDGE,{"derivedFrom":makeQuery(id+"F9.opBoolean","INTERSECT",EDGE,{"disambiguationData":[OD(0.0)],"derivedFrom":[makeQuery(id+"F5.opPattern","COPY",FACE,{"derivedFrom":makeQuery(id+"F4.opRevolve","SWEPT_FACE",FACE,{"disambiguationData":[OSD([sQuery(id+"F3.wireOp",EDGE,"E18")])]}),"instanceName":"1"}),makeQuery(id+"F8.opPattern","COPY",FACE,{"derivedFrom":makeQuery(id+"F4.opRevolve","SWEPT_FACE",FACE,{"disambiguationData":[OSD([sQuery(id+"F3.wireOp",EDGE,"E19.1")])]}),"instanceName":"1"})]})});
            fillet(context, id + "F16", {"entities" : qUnion([Q0, Q1, Q2, Q3, Q4, Q5, Q6, Q7, Q8, Q9, Q10, Q11, Q12, Q13, Q14, Q15, Q16, Q17, Q18, Q19, Q20, Q21, Q22, Q23]), "radius" : 1 * mm, "tangentPropagation" : true, "allowEdgeOverflow" : false});
        }
        {
            var Q0;
            {var subQ0=makeQuery(id+"F4.opRevolve","SWEPT_FACE",FACE,{"disambiguationData":[OSD([sQuery(id+"F3.wireOp",EDGE,"E18")])]});var subQ1=makeQuery(id+"F4.opRevolve","SWEPT_FACE",FACE,{"disambiguationData":[OSD([sQuery(id+"F3.wireOp",EDGE,"E19.0")])]});Q0=makeQuery(id+"F10.opBoolean","SPLIT",FACE,{"disambiguationData":[TD([makeQuery(id+"F5.opPattern","COPY",FACE,{"derivedFrom":subQ1,"instanceName":"1"}),makeQuery(id+"F8.opPattern","COPY",FACE,{"derivedFrom":subQ0,"instanceName":"1"}),makeQuery(id+"F8.opPattern","COPY",FACE,{"derivedFrom":makeQuery(id+"F5.opPattern","COPY",FACE,{"derivedFrom":subQ0,"instanceName":"1"}),"instanceName":"1"}),makeQuery(id+"F8.opPattern","COPY",FACE,{"derivedFrom":subQ1,"instanceName":"2"})])],"derivedFrom":makeQuery(id+"F2.opRevolve","SWEPT_FACE",FACE,{"disambiguationData":[OSD([sQuery(id+"F1.wireOp",EDGE,"E3")])]})});}
            var Q1;
            {var subQ0=makeQuery(id+"F4.opRevolve","SWEPT_FACE",FACE,{"disambiguationData":[OSD([sQuery(id+"F3.wireOp",EDGE,"E18")])]});var subQ1=makeQuery(id+"F4.opRevolve","SWEPT_FACE",FACE,{"disambiguationData":[OSD([sQuery(id+"F3.wireOp",EDGE,"E19.0")])]});Q1=makeQuery(id+"F10.opBoolean","SPLIT",FACE,{"disambiguationData":[TD([makeQuery(id+"F5.opPattern","COPY",FACE,{"derivedFrom":subQ1,"instanceName":"1"}),makeQuery(id+"F8.opPattern","COPY",FACE,{"derivedFrom":subQ1,"instanceName":"1"}),makeQuery(id+"F8.opPattern","COPY",FACE,{"derivedFrom":subQ0,"instanceName":"2"}),makeQuery(id+"F8.opPattern","COPY",FACE,{"derivedFrom":makeQuery(id+"F5.opPattern","COPY",FACE,{"derivedFrom":subQ0,"instanceName":"1"}),"instanceName":"2"})])],"derivedFrom":makeQuery(id+"F2.opRevolve","SWEPT_FACE",FACE,{"disambiguationData":[OSD([sQuery(id+"F1.wireOp",EDGE,"E3")])]})});}
            var Q2;
            {var subQ0=makeQuery(id+"F4.opRevolve","SWEPT_FACE",FACE,{"disambiguationData":[OSD([sQuery(id+"F3.wireOp",EDGE,"E19.0")])]});var subQ1=makeQuery(id+"F4.opRevolve","SWEPT_FACE",FACE,{"disambiguationData":[OSD([sQuery(id+"F3.wireOp",EDGE,"E18")])]});Q2=makeQuery(id+"F10.opBoolean","SPLIT",FACE,{"disambiguationData":[TD([subQ1,makeQuery(id+"F5.opPattern","COPY",FACE,{"derivedFrom":subQ1,"instanceName":"1"}),makeQuery(id+"F8.opPattern","COPY",FACE,{"derivedFrom":subQ0,"instanceName":"1"}),makeQuery(id+"F8.opPattern","COPY",FACE,{"derivedFrom":subQ0,"instanceName":"2"})])],"derivedFrom":makeQuery(id+"F2.opRevolve","SWEPT_FACE",FACE,{"disambiguationData":[OSD([sQuery(id+"F1.wireOp",EDGE,"E3")])]})});}
            var Q3;
            {var subQ0=makeQuery(id+"F4.opRevolve","SWEPT_FACE",FACE,{"disambiguationData":[OSD([sQuery(id+"F3.wireOp",EDGE,"E19.0")])]});var subQ1=makeQuery(id+"F4.opRevolve","SWEPT_FACE",FACE,{"disambiguationData":[OSD([sQuery(id+"F3.wireOp",EDGE,"E18")])]});Q3=makeQuery(id+"F10.opBoolean","SPLIT",FACE,{"disambiguationData":[TD([subQ1,makeQuery(id+"F5.opPattern","COPY",FACE,{"derivedFrom":subQ1,"instanceName":"1"}),makeQuery(id+"F8.opPattern","COPY",FACE,{"derivedFrom":subQ0,"instanceName":"1"}),makeQuery(id+"F8.opPattern","COPY",FACE,{"derivedFrom":makeQuery(id+"F5.opPattern","COPY",FACE,{"derivedFrom":subQ0,"instanceName":"1"}),"instanceName":"2"})])],"derivedFrom":makeQuery(id+"F2.opRevolve","SWEPT_FACE",FACE,{"disambiguationData":[OSD([sQuery(id+"F1.wireOp",EDGE,"E3")])]})});}
            var Q4;
            {var subQ0=makeQuery(id+"F4.opRevolve","SWEPT_FACE",FACE,{"disambiguationData":[OSD([sQuery(id+"F3.wireOp",EDGE,"E18")])]});var subQ1=makeQuery(id+"F4.opRevolve","SWEPT_FACE",FACE,{"disambiguationData":[OSD([sQuery(id+"F3.wireOp",EDGE,"E19.0")])]});Q4=makeQuery(id+"F10.opBoolean","SPLIT",FACE,{"disambiguationData":[TD([subQ1,makeQuery(id+"F8.opPattern","COPY",FACE,{"derivedFrom":subQ1,"instanceName":"1"}),makeQuery(id+"F8.opPattern","COPY",FACE,{"derivedFrom":subQ0,"instanceName":"2"}),makeQuery(id+"F8.opPattern","COPY",FACE,{"derivedFrom":makeQuery(id+"F5.opPattern","COPY",FACE,{"derivedFrom":subQ0,"instanceName":"1"}),"instanceName":"2"})])],"derivedFrom":makeQuery(id+"F2.opRevolve","SWEPT_FACE",FACE,{"disambiguationData":[OSD([sQuery(id+"F1.wireOp",EDGE,"E3")])]})});}
            var Q5;
            {var subQ0=makeQuery(id+"F5.opPattern","COPY",FACE,{"derivedFrom":makeQuery(id+"F4.opRevolve","SWEPT_FACE",FACE,{"disambiguationData":[OSD([sQuery(id+"F3.wireOp",EDGE,"E19.0")])]}),"instanceName":"1"});var subQ1=makeQuery(id+"F4.opRevolve","SWEPT_FACE",FACE,{"disambiguationData":[OSD([sQuery(id+"F3.wireOp",EDGE,"E18")])]});Q5=makeQuery(id+"F10.opBoolean","SPLIT",FACE,{"disambiguationData":[TD([subQ0,makeQuery(id+"F8.opPattern","COPY",FACE,{"derivedFrom":subQ1,"instanceName":"1"}),makeQuery(id+"F8.opPattern","COPY",FACE,{"derivedFrom":makeQuery(id+"F5.opPattern","COPY",FACE,{"derivedFrom":subQ1,"instanceName":"1"}),"instanceName":"1"}),makeQuery(id+"F8.opPattern","COPY",FACE,{"derivedFrom":subQ0,"instanceName":"2"})])],"derivedFrom":makeQuery(id+"F2.opRevolve","SWEPT_FACE",FACE,{"disambiguationData":[OSD([sQuery(id+"F1.wireOp",EDGE,"E3")])]})});}
            var Q6;
            {var subQ0=makeQuery(id+"F4.opRevolve","SWEPT_FACE",FACE,{"disambiguationData":[OSD([sQuery(id+"F3.wireOp",EDGE,"E18")])]});var subQ1=makeQuery(id+"F4.opRevolve","SWEPT_FACE",FACE,{"disambiguationData":[OSD([sQuery(id+"F3.wireOp",EDGE,"E19.0")])]});Q6=makeQuery(id+"F10.opBoolean","SPLIT",FACE,{"disambiguationData":[TD([subQ1,makeQuery(id+"F8.opPattern","COPY",FACE,{"derivedFrom":subQ0,"instanceName":"1"}),makeQuery(id+"F8.opPattern","COPY",FACE,{"derivedFrom":makeQuery(id+"F5.opPattern","COPY",FACE,{"derivedFrom":subQ0,"instanceName":"1"}),"instanceName":"1"}),makeQuery(id+"F8.opPattern","COPY",FACE,{"derivedFrom":subQ1,"instanceName":"2"})])],"derivedFrom":makeQuery(id+"F2.opRevolve","SWEPT_FACE",FACE,{"disambiguationData":[OSD([sQuery(id+"F1.wireOp",EDGE,"E3")])]})});}
            var Q7;
            {var subQ0=makeQuery(id+"F4.opRevolve","SWEPT_FACE",FACE,{"disambiguationData":[OSD([sQuery(id+"F3.wireOp",EDGE,"E19.0")])]});var subQ1=makeQuery(id+"F4.opRevolve","SWEPT_FACE",FACE,{"disambiguationData":[OSD([sQuery(id+"F3.wireOp",EDGE,"E18")])]});Q7=makeQuery(id+"F10.opBoolean","SPLIT",FACE,{"disambiguationData":[TD([subQ0,makeQuery(id+"F8.opPattern","COPY",FACE,{"derivedFrom":subQ1,"instanceName":"1"}),makeQuery(id+"F8.opPattern","COPY",FACE,{"derivedFrom":makeQuery(id+"F5.opPattern","COPY",FACE,{"derivedFrom":subQ1,"instanceName":"1"}),"instanceName":"1"}),makeQuery(id+"F8.opPattern","COPY",FACE,{"derivedFrom":makeQuery(id+"F5.opPattern","COPY",FACE,{"derivedFrom":subQ0,"instanceName":"1"}),"instanceName":"2"})])],"derivedFrom":makeQuery(id+"F2.opRevolve","SWEPT_FACE",FACE,{"disambiguationData":[OSD([sQuery(id+"F1.wireOp",EDGE,"E3")])]})});}
            var Q8;
            {var subQ0=makeQuery(id+"F4.opRevolve","SWEPT_FACE",FACE,{"disambiguationData":[OSD([sQuery(id+"F3.wireOp",EDGE,"E18")])]});var subQ1=makeQuery(id+"F4.opRevolve","SWEPT_FACE",FACE,{"disambiguationData":[OSD([sQuery(id+"F3.wireOp",EDGE,"E19.0")])]});Q8=makeQuery(id+"F10.opBoolean","SPLIT",FACE,{"disambiguationData":[TD([subQ1,makeQuery(id+"F8.opPattern","COPY",FACE,{"derivedFrom":makeQuery(id+"F5.opPattern","COPY",FACE,{"derivedFrom":subQ1,"instanceName":"1"}),"instanceName":"1"}),makeQuery(id+"F8.opPattern","COPY",FACE,{"derivedFrom":subQ0,"instanceName":"2"}),makeQuery(id+"F8.opPattern","COPY",FACE,{"derivedFrom":makeQuery(id+"F5.opPattern","COPY",FACE,{"derivedFrom":subQ0,"instanceName":"1"}),"instanceName":"2"})])],"derivedFrom":makeQuery(id+"F2.opRevolve","SWEPT_FACE",FACE,{"disambiguationData":[OSD([sQuery(id+"F1.wireOp",EDGE,"E3")])]})});}
            var Q9;
            {var subQ0=makeQuery(id+"F4.opRevolve","SWEPT_FACE",FACE,{"disambiguationData":[OSD([sQuery(id+"F3.wireOp",EDGE,"E19.0")])]});var subQ1=makeQuery(id+"F4.opRevolve","SWEPT_FACE",FACE,{"disambiguationData":[OSD([sQuery(id+"F3.wireOp",EDGE,"E18")])]});Q9=makeQuery(id+"F10.opBoolean","SPLIT",FACE,{"disambiguationData":[TD([subQ1,makeQuery(id+"F5.opPattern","COPY",FACE,{"derivedFrom":subQ1,"instanceName":"1"}),makeQuery(id+"F8.opPattern","COPY",FACE,{"derivedFrom":makeQuery(id+"F5.opPattern","COPY",FACE,{"derivedFrom":subQ0,"instanceName":"1"}),"instanceName":"1"}),makeQuery(id+"F8.opPattern","COPY",FACE,{"derivedFrom":subQ0,"instanceName":"2"})])],"derivedFrom":makeQuery(id+"F2.opRevolve","SWEPT_FACE",FACE,{"disambiguationData":[OSD([sQuery(id+"F1.wireOp",EDGE,"E3")])]})});}
            var Q10;
            {var subQ0=makeQuery(id+"F4.opRevolve","SWEPT_FACE",FACE,{"disambiguationData":[OSD([sQuery(id+"F3.wireOp",EDGE,"E18")])]});var subQ1=makeQuery(id+"F5.opPattern","COPY",FACE,{"derivedFrom":makeQuery(id+"F4.opRevolve","SWEPT_FACE",FACE,{"disambiguationData":[OSD([sQuery(id+"F3.wireOp",EDGE,"E19.0")])]}),"instanceName":"1"});Q10=makeQuery(id+"F10.opBoolean","SPLIT",FACE,{"disambiguationData":[TD([subQ1,makeQuery(id+"F8.opPattern","COPY",FACE,{"derivedFrom":subQ1,"instanceName":"1"}),makeQuery(id+"F8.opPattern","COPY",FACE,{"derivedFrom":subQ0,"instanceName":"2"}),makeQuery(id+"F8.opPattern","COPY",FACE,{"derivedFrom":makeQuery(id+"F5.opPattern","COPY",FACE,{"derivedFrom":subQ0,"instanceName":"1"}),"instanceName":"2"})])],"derivedFrom":makeQuery(id+"F2.opRevolve","SWEPT_FACE",FACE,{"disambiguationData":[OSD([sQuery(id+"F1.wireOp",EDGE,"E3")])]})});}
            var Q11;
            {var subQ0=makeQuery(id+"F5.opPattern","COPY",FACE,{"derivedFrom":makeQuery(id+"F4.opRevolve","SWEPT_FACE",FACE,{"disambiguationData":[OSD([sQuery(id+"F3.wireOp",EDGE,"E19.0")])]}),"instanceName":"1"});var subQ1=makeQuery(id+"F4.opRevolve","SWEPT_FACE",FACE,{"disambiguationData":[OSD([sQuery(id+"F3.wireOp",EDGE,"E18")])]});Q11=makeQuery(id+"F10.opBoolean","SPLIT",FACE,{"disambiguationData":[TD([subQ1,makeQuery(id+"F5.opPattern","COPY",FACE,{"derivedFrom":subQ1,"instanceName":"1"}),makeQuery(id+"F8.opPattern","COPY",FACE,{"derivedFrom":subQ0,"instanceName":"1"}),makeQuery(id+"F8.opPattern","COPY",FACE,{"derivedFrom":subQ0,"instanceName":"2"})])],"derivedFrom":makeQuery(id+"F2.opRevolve","SWEPT_FACE",FACE,{"disambiguationData":[OSD([sQuery(id+"F1.wireOp",EDGE,"E3")])]})});}
            fillet(context, id + "F17", {"entities" : qUnion([Q0, Q1, Q2, Q3, Q4, Q5, Q6, Q7, Q8, Q9, Q10, Q11]), "radius" : .5 * mm, "tangentPropagation" : true, "allowEdgeOverflow" : false});
        }
        {
            var Q0;
            {var subQ0=makeQuery(id+"F5.opPattern","COPY",FACE,{"derivedFrom":makeQuery(id+"F4.opRevolve","SWEPT_FACE",FACE,{"disambiguationData":[OSD([sQuery(id+"F3.wireOp",EDGE,"E19.0")])]}),"instanceName":"1"});Q0=makeQuery(id+"F10.opBoolean","COPY",EDGE,{"derivedFrom":makeQuery(id+"F9.opBoolean","INTERSECT",EDGE,{"disambiguationData":[OD(1.0)],"derivedFrom":[subQ0,makeQuery(id+"F8.opPattern","COPY",FACE,{"derivedFrom":subQ0,"instanceName":"2"})]})});}
            var Q1;
            {var subQ0=makeQuery(id+"F5.opPattern","COPY",FACE,{"derivedFrom":makeQuery(id+"F4.opRevolve","SWEPT_FACE",FACE,{"disambiguationData":[OSD([sQuery(id+"F3.wireOp",EDGE,"E19.0")])]}),"instanceName":"1"});Q1=makeQuery(id+"F10.opBoolean","COPY",EDGE,{"derivedFrom":makeQuery(id+"F9.opBoolean","INTERSECT",EDGE,{"disambiguationData":[OD(1.0)],"derivedFrom":[subQ0,makeQuery(id+"F8.opPattern","COPY",FACE,{"derivedFrom":subQ0,"instanceName":"1"})]})});}
            var Q2;
            {var subQ0=makeQuery(id+"F5.opPattern","COPY",FACE,{"derivedFrom":makeQuery(id+"F4.opRevolve","SWEPT_FACE",FACE,{"disambiguationData":[OSD([sQuery(id+"F3.wireOp",EDGE,"E19.0")])]}),"instanceName":"1"});Q2=makeQuery(id+"F10.opBoolean","COPY",EDGE,{"derivedFrom":makeQuery(id+"F9.opBoolean","INTERSECT",EDGE,{"disambiguationData":[OD(1.0)],"derivedFrom":[makeQuery(id+"F8.opPattern","COPY",FACE,{"derivedFrom":subQ0,"instanceName":"1"}),makeQuery(id+"F8.opPattern","COPY",FACE,{"derivedFrom":subQ0,"instanceName":"2"})]})});}
            var Q3;
            {var subQ0=makeQuery(id+"F4.opRevolve","SWEPT_FACE",FACE,{"disambiguationData":[OSD([sQuery(id+"F3.wireOp",EDGE,"E19.0")])]});Q3=makeQuery(id+"F10.opBoolean","COPY",EDGE,{"derivedFrom":makeQuery(id+"F9.opBoolean","INTERSECT",EDGE,{"disambiguationData":[OD(1.0)],"derivedFrom":[makeQuery(id+"F5.opPattern","COPY",FACE,{"derivedFrom":subQ0,"instanceName":"1"}),makeQuery(id+"F8.opPattern","COPY",FACE,{"derivedFrom":subQ0,"instanceName":"2"})]})});}
            var Q4;
            {var subQ0=makeQuery(id+"F5.opPattern","COPY",FACE,{"derivedFrom":makeQuery(id+"F4.opRevolve","SWEPT_FACE",FACE,{"disambiguationData":[OSD([sQuery(id+"F3.wireOp",EDGE,"E19.0")])]}),"instanceName":"1"});Q4=makeQuery(id+"F10.opBoolean","COPY",EDGE,{"derivedFrom":makeQuery(id+"F9.opBoolean","INTERSECT",EDGE,{"disambiguationData":[OD(0.0)],"derivedFrom":[subQ0,makeQuery(id+"F8.opPattern","COPY",FACE,{"derivedFrom":subQ0,"instanceName":"1"})]})});}
            var Q5;
            {var subQ0=makeQuery(id+"F4.opRevolve","SWEPT_FACE",FACE,{"disambiguationData":[OSD([sQuery(id+"F3.wireOp",EDGE,"E19.0")])]});Q5=makeQuery(id+"F10.opBoolean","COPY",EDGE,{"derivedFrom":makeQuery(id+"F9.opBoolean","INTERSECT",EDGE,{"disambiguationData":[OD(1.0)],"derivedFrom":[makeQuery(id+"F8.opPattern","COPY",FACE,{"derivedFrom":makeQuery(id+"F5.opPattern","COPY",FACE,{"derivedFrom":subQ0,"instanceName":"1"}),"instanceName":"1"}),makeQuery(id+"F8.opPattern","COPY",FACE,{"derivedFrom":subQ0,"instanceName":"2"})]})});}
            var Q6;
            {var subQ0=makeQuery(id+"F5.opPattern","COPY",FACE,{"derivedFrom":makeQuery(id+"F4.opRevolve","SWEPT_FACE",FACE,{"disambiguationData":[OSD([sQuery(id+"F3.wireOp",EDGE,"E19.0")])]}),"instanceName":"1"});Q6=makeQuery(id+"F10.opBoolean","COPY",EDGE,{"derivedFrom":makeQuery(id+"F9.opBoolean","INTERSECT",EDGE,{"disambiguationData":[OD(0.0)],"derivedFrom":[makeQuery(id+"F8.opPattern","COPY",FACE,{"derivedFrom":subQ0,"instanceName":"1"}),makeQuery(id+"F8.opPattern","COPY",FACE,{"derivedFrom":subQ0,"instanceName":"2"})]})});}
            var Q7;
            {var subQ0=makeQuery(id+"F4.opRevolve","SWEPT_FACE",FACE,{"disambiguationData":[OSD([sQuery(id+"F3.wireOp",EDGE,"E19.0")])]});Q7=makeQuery(id+"F10.opBoolean","COPY",EDGE,{"derivedFrom":makeQuery(id+"F9.opBoolean","INTERSECT",EDGE,{"disambiguationData":[OD(1.0)],"derivedFrom":[subQ0,makeQuery(id+"F8.opPattern","COPY",FACE,{"derivedFrom":makeQuery(id+"F5.opPattern","COPY",FACE,{"derivedFrom":subQ0,"instanceName":"1"}),"instanceName":"2"})]})});}
            var Q8;
            {var subQ0=makeQuery(id+"F4.opRevolve","SWEPT_FACE",FACE,{"disambiguationData":[OSD([sQuery(id+"F3.wireOp",EDGE,"E19.0")])]});Q8=makeQuery(id+"F10.opBoolean","COPY",EDGE,{"derivedFrom":makeQuery(id+"F9.opBoolean","INTERSECT",EDGE,{"disambiguationData":[OD(1.0)],"derivedFrom":[subQ0,makeQuery(id+"F8.opPattern","COPY",FACE,{"derivedFrom":makeQuery(id+"F5.opPattern","COPY",FACE,{"derivedFrom":subQ0,"instanceName":"1"}),"instanceName":"1"})]})});}
            var Q9;
            {var subQ0=makeQuery(id+"F4.opRevolve","SWEPT_FACE",FACE,{"disambiguationData":[OSD([sQuery(id+"F3.wireOp",EDGE,"E19.0")])]});Q9=makeQuery(id+"F10.opBoolean","COPY",EDGE,{"derivedFrom":makeQuery(id+"F9.opBoolean","INTERSECT",EDGE,{"disambiguationData":[OD(0.0)],"derivedFrom":[subQ0,makeQuery(id+"F8.opPattern","COPY",FACE,{"derivedFrom":makeQuery(id+"F5.opPattern","COPY",FACE,{"derivedFrom":subQ0,"instanceName":"1"}),"instanceName":"1"})]})});}
            var Q10;
            {var subQ0=makeQuery(id+"F4.opRevolve","SWEPT_FACE",FACE,{"disambiguationData":[OSD([sQuery(id+"F3.wireOp",EDGE,"E19.0")])]});Q10=makeQuery(id+"F10.opBoolean","COPY",EDGE,{"derivedFrom":makeQuery(id+"F9.opBoolean","INTERSECT",EDGE,{"disambiguationData":[OD(1.0)],"derivedFrom":[subQ0,makeQuery(id+"F8.opPattern","COPY",FACE,{"derivedFrom":subQ0,"instanceName":"2"})]})});}
            var Q11;
            {var subQ0=makeQuery(id+"F4.opRevolve","SWEPT_FACE",FACE,{"disambiguationData":[OSD([sQuery(id+"F3.wireOp",EDGE,"E19.0")])]});Q11=makeQuery(id+"F10.opBoolean","COPY",EDGE,{"derivedFrom":makeQuery(id+"F9.opBoolean","INTERSECT",EDGE,{"disambiguationData":[OD(0.0)],"derivedFrom":[makeQuery(id+"F8.opPattern","COPY",FACE,{"derivedFrom":makeQuery(id+"F5.opPattern","COPY",FACE,{"derivedFrom":subQ0,"instanceName":"1"}),"instanceName":"1"}),makeQuery(id+"F8.opPattern","COPY",FACE,{"derivedFrom":subQ0,"instanceName":"2"})]})});}
            var Q12;
            {var subQ0=makeQuery(id+"F4.opRevolve","SWEPT_FACE",FACE,{"disambiguationData":[OSD([sQuery(id+"F3.wireOp",EDGE,"E19.0")])]});Q12=makeQuery(id+"F10.opBoolean","COPY",EDGE,{"derivedFrom":makeQuery(id+"F9.opBoolean","INTERSECT",EDGE,{"disambiguationData":[OD(0.0)],"derivedFrom":[makeQuery(id+"F8.opPattern","COPY",FACE,{"derivedFrom":subQ0,"instanceName":"1"}),makeQuery(id+"F8.opPattern","COPY",FACE,{"derivedFrom":subQ0,"instanceName":"2"})]})});}
            var Q13;
            {var subQ0=makeQuery(id+"F4.opRevolve","SWEPT_FACE",FACE,{"disambiguationData":[OSD([sQuery(id+"F3.wireOp",EDGE,"E19.0")])]});Q13=makeQuery(id+"F10.opBoolean","COPY",EDGE,{"derivedFrom":makeQuery(id+"F9.opBoolean","INTERSECT",EDGE,{"disambiguationData":[OD(0.0)],"derivedFrom":[subQ0,makeQuery(id+"F8.opPattern","COPY",FACE,{"derivedFrom":subQ0,"instanceName":"1"})]})});}
            var Q14;
            {var subQ0=makeQuery(id+"F4.opRevolve","SWEPT_FACE",FACE,{"disambiguationData":[OSD([sQuery(id+"F3.wireOp",EDGE,"E19.0")])]});Q14=makeQuery(id+"F10.opBoolean","COPY",EDGE,{"derivedFrom":makeQuery(id+"F9.opBoolean","INTERSECT",EDGE,{"disambiguationData":[OD(0.0)],"derivedFrom":[subQ0,makeQuery(id+"F8.opPattern","COPY",FACE,{"derivedFrom":subQ0,"instanceName":"2"})]})});}
            var Q15;
            {var subQ0=makeQuery(id+"F4.opRevolve","SWEPT_FACE",FACE,{"disambiguationData":[OSD([sQuery(id+"F3.wireOp",EDGE,"E19.0")])]});Q15=makeQuery(id+"F10.opBoolean","COPY",EDGE,{"derivedFrom":makeQuery(id+"F9.opBoolean","INTERSECT",EDGE,{"disambiguationData":[OD(0.0)],"derivedFrom":[makeQuery(id+"F5.opPattern","COPY",FACE,{"derivedFrom":subQ0,"instanceName":"1"}),makeQuery(id+"F8.opPattern","COPY",FACE,{"derivedFrom":subQ0,"instanceName":"1"})]})});}
            var Q16;
            {var subQ0=makeQuery(id+"F4.opRevolve","SWEPT_FACE",FACE,{"disambiguationData":[OSD([sQuery(id+"F3.wireOp",EDGE,"E19.0")])]});Q16=makeQuery(id+"F10.opBoolean","COPY",EDGE,{"derivedFrom":makeQuery(id+"F9.opBoolean","INTERSECT",EDGE,{"disambiguationData":[OD(1.0)],"derivedFrom":[makeQuery(id+"F8.opPattern","COPY",FACE,{"derivedFrom":subQ0,"instanceName":"1"}),makeQuery(id+"F8.opPattern","COPY",FACE,{"derivedFrom":subQ0,"instanceName":"2"})]})});}
            var Q17;
            {var subQ0=makeQuery(id+"F4.opRevolve","SWEPT_FACE",FACE,{"disambiguationData":[OSD([sQuery(id+"F3.wireOp",EDGE,"E19.0")])]});Q17=makeQuery(id+"F10.opBoolean","COPY",EDGE,{"derivedFrom":makeQuery(id+"F9.opBoolean","INTERSECT",EDGE,{"disambiguationData":[OD(0.0)],"derivedFrom":[makeQuery(id+"F5.opPattern","COPY",FACE,{"derivedFrom":subQ0,"instanceName":"1"}),makeQuery(id+"F8.opPattern","COPY",FACE,{"derivedFrom":subQ0,"instanceName":"2"})]})});}
            var Q18;
            {var subQ0=makeQuery(id+"F4.opRevolve","SWEPT_FACE",FACE,{"disambiguationData":[OSD([sQuery(id+"F3.wireOp",EDGE,"E19.0")])]});Q18=makeQuery(id+"F10.opBoolean","COPY",EDGE,{"derivedFrom":makeQuery(id+"F9.opBoolean","INTERSECT",EDGE,{"disambiguationData":[OD(1.0)],"derivedFrom":[makeQuery(id+"F8.opPattern","COPY",FACE,{"derivedFrom":subQ0,"instanceName":"1"}),makeQuery(id+"F8.opPattern","COPY",FACE,{"derivedFrom":makeQuery(id+"F5.opPattern","COPY",FACE,{"derivedFrom":subQ0,"instanceName":"1"}),"instanceName":"2"})]})});}
            var Q19;
            {var subQ0=makeQuery(id+"F4.opRevolve","SWEPT_FACE",FACE,{"disambiguationData":[OSD([sQuery(id+"F3.wireOp",EDGE,"E19.0")])]});Q19=makeQuery(id+"F10.opBoolean","COPY",EDGE,{"derivedFrom":makeQuery(id+"F9.opBoolean","INTERSECT",EDGE,{"disambiguationData":[OD(1.0)],"derivedFrom":[makeQuery(id+"F5.opPattern","COPY",FACE,{"derivedFrom":subQ0,"instanceName":"1"}),makeQuery(id+"F8.opPattern","COPY",FACE,{"derivedFrom":subQ0,"instanceName":"1"})]})});}
            var Q20;
            {var subQ0=makeQuery(id+"F5.opPattern","COPY",FACE,{"derivedFrom":makeQuery(id+"F4.opRevolve","SWEPT_FACE",FACE,{"disambiguationData":[OSD([sQuery(id+"F3.wireOp",EDGE,"E19.0")])]}),"instanceName":"1"});Q20=makeQuery(id+"F10.opBoolean","COPY",EDGE,{"derivedFrom":makeQuery(id+"F9.opBoolean","INTERSECT",EDGE,{"disambiguationData":[OD(0.0)],"derivedFrom":[subQ0,makeQuery(id+"F8.opPattern","COPY",FACE,{"derivedFrom":subQ0,"instanceName":"2"})]})});}
            var Q21;
            {var subQ0=makeQuery(id+"F4.opRevolve","SWEPT_FACE",FACE,{"disambiguationData":[OSD([sQuery(id+"F3.wireOp",EDGE,"E19.0")])]});Q21=makeQuery(id+"F10.opBoolean","COPY",EDGE,{"derivedFrom":makeQuery(id+"F9.opBoolean","INTERSECT",EDGE,{"disambiguationData":[OD(1.0)],"derivedFrom":[subQ0,makeQuery(id+"F8.opPattern","COPY",FACE,{"derivedFrom":subQ0,"instanceName":"1"})]})});}
            var Q22;
            {var subQ0=makeQuery(id+"F4.opRevolve","SWEPT_FACE",FACE,{"disambiguationData":[OSD([sQuery(id+"F3.wireOp",EDGE,"E19.0")])]});Q22=makeQuery(id+"F10.opBoolean","COPY",EDGE,{"derivedFrom":makeQuery(id+"F9.opBoolean","INTERSECT",EDGE,{"disambiguationData":[OD(0.0)],"derivedFrom":[makeQuery(id+"F8.opPattern","COPY",FACE,{"derivedFrom":subQ0,"instanceName":"1"}),makeQuery(id+"F8.opPattern","COPY",FACE,{"derivedFrom":makeQuery(id+"F5.opPattern","COPY",FACE,{"derivedFrom":subQ0,"instanceName":"1"}),"instanceName":"2"})]})});}
            var Q23;
            {var subQ0=makeQuery(id+"F4.opRevolve","SWEPT_FACE",FACE,{"disambiguationData":[OSD([sQuery(id+"F3.wireOp",EDGE,"E19.0")])]});Q23=makeQuery(id+"F10.opBoolean","COPY",EDGE,{"derivedFrom":makeQuery(id+"F9.opBoolean","INTERSECT",EDGE,{"disambiguationData":[OD(0.0)],"derivedFrom":[subQ0,makeQuery(id+"F8.opPattern","COPY",FACE,{"derivedFrom":makeQuery(id+"F5.opPattern","COPY",FACE,{"derivedFrom":subQ0,"instanceName":"1"}),"instanceName":"2"})]})});}
            fillet(context, id + "F18", {"entities" : qUnion([Q0, Q1, Q2, Q3, Q4, Q5, Q6, Q7, Q8, Q9, Q10, Q11, Q12, Q13, Q14, Q15, Q16, Q17, Q18, Q19, Q20, Q21, Q22, Q23]), "radius" : 1.5 * mm, "tangentPropagation" : true, "allowEdgeOverflow" : false});
        }
        {
            var Q0;
            {var subQ0=makeQuery(id+"F4.opRevolve","SWEPT_FACE",FACE,{"disambiguationData":[OSD([sQuery(id+"F3.wireOp",EDGE,"E19.1")])]});Q0=makeQuery(id+"F10.opBoolean","COPY",EDGE,{"derivedFrom":makeQuery(id+"F9.opBoolean","INTERSECT",EDGE,{"disambiguationData":[OD(1.0)],"derivedFrom":[subQ0,makeQuery(id+"F8.opPattern","COPY",FACE,{"derivedFrom":subQ0,"instanceName":"1"})]})});}
            var Q1;
            {var subQ0=makeQuery(id+"F4.opRevolve","SWEPT_FACE",FACE,{"disambiguationData":[OSD([sQuery(id+"F3.wireOp",EDGE,"E19.1")])]});Q1=makeQuery(id+"F10.opBoolean","COPY",EDGE,{"derivedFrom":makeQuery(id+"F9.opBoolean","INTERSECT",EDGE,{"disambiguationData":[OD(0.0)],"derivedFrom":[makeQuery(id+"F8.opPattern","COPY",FACE,{"derivedFrom":subQ0,"instanceName":"1"}),makeQuery(id+"F8.opPattern","COPY",FACE,{"derivedFrom":makeQuery(id+"F5.opPattern","COPY",FACE,{"derivedFrom":subQ0,"instanceName":"1"}),"instanceName":"2"})]})});}
            var Q2;
            {var subQ0=makeQuery(id+"F4.opRevolve","SWEPT_FACE",FACE,{"disambiguationData":[OSD([sQuery(id+"F3.wireOp",EDGE,"E19.1")])]});Q2=makeQuery(id+"F10.opBoolean","COPY",EDGE,{"derivedFrom":makeQuery(id+"F9.opBoolean","INTERSECT",EDGE,{"disambiguationData":[OD(0.0)],"derivedFrom":[subQ0,makeQuery(id+"F8.opPattern","COPY",FACE,{"derivedFrom":makeQuery(id+"F5.opPattern","COPY",FACE,{"derivedFrom":subQ0,"instanceName":"1"}),"instanceName":"2"})]})});}
            var Q3;
            {var subQ0=makeQuery(id+"F4.opRevolve","SWEPT_FACE",FACE,{"disambiguationData":[OSD([sQuery(id+"F3.wireOp",EDGE,"E19.1")])]});Q3=makeQuery(id+"F10.opBoolean","COPY",EDGE,{"derivedFrom":makeQuery(id+"F9.opBoolean","INTERSECT",EDGE,{"disambiguationData":[OD(0.0)],"derivedFrom":[makeQuery(id+"F8.opPattern","COPY",FACE,{"derivedFrom":subQ0,"instanceName":"1"}),makeQuery(id+"F8.opPattern","COPY",FACE,{"derivedFrom":subQ0,"instanceName":"2"})]})});}
            var Q4;
            {var subQ0=makeQuery(id+"F4.opRevolve","SWEPT_FACE",FACE,{"disambiguationData":[OSD([sQuery(id+"F3.wireOp",EDGE,"E19.1")])]});Q4=makeQuery(id+"F10.opBoolean","COPY",EDGE,{"derivedFrom":makeQuery(id+"F9.opBoolean","INTERSECT",EDGE,{"disambiguationData":[OD(0.0)],"derivedFrom":[subQ0,makeQuery(id+"F8.opPattern","COPY",FACE,{"derivedFrom":subQ0,"instanceName":"2"})]})});}
            var Q5;
            {var subQ0=makeQuery(id+"F4.opRevolve","SWEPT_FACE",FACE,{"disambiguationData":[OSD([sQuery(id+"F3.wireOp",EDGE,"E19.1")])]});Q5=makeQuery(id+"F10.opBoolean","COPY",EDGE,{"derivedFrom":makeQuery(id+"F9.opBoolean","INTERSECT",EDGE,{"disambiguationData":[OD(0.0)],"derivedFrom":[subQ0,makeQuery(id+"F8.opPattern","COPY",FACE,{"derivedFrom":subQ0,"instanceName":"1"})]})});}
            var Q6;
            {var subQ0=makeQuery(id+"F4.opRevolve","SWEPT_FACE",FACE,{"disambiguationData":[OSD([sQuery(id+"F3.wireOp",EDGE,"E19.1")])]});Q6=makeQuery(id+"F10.opBoolean","COPY",EDGE,{"derivedFrom":makeQuery(id+"F9.opBoolean","INTERSECT",EDGE,{"disambiguationData":[OD(1.0)],"derivedFrom":[makeQuery(id+"F8.opPattern","COPY",FACE,{"derivedFrom":subQ0,"instanceName":"1"}),makeQuery(id+"F8.opPattern","COPY",FACE,{"derivedFrom":makeQuery(id+"F5.opPattern","COPY",FACE,{"derivedFrom":subQ0,"instanceName":"1"}),"instanceName":"2"})]})});}
            var Q7;
            {var subQ0=makeQuery(id+"F4.opRevolve","SWEPT_FACE",FACE,{"disambiguationData":[OSD([sQuery(id+"F3.wireOp",EDGE,"E19.1")])]});Q7=makeQuery(id+"F10.opBoolean","COPY",EDGE,{"derivedFrom":makeQuery(id+"F9.opBoolean","INTERSECT",EDGE,{"disambiguationData":[OD(1.0)],"derivedFrom":[makeQuery(id+"F5.opPattern","COPY",FACE,{"derivedFrom":subQ0,"instanceName":"1"}),makeQuery(id+"F8.opPattern","COPY",FACE,{"derivedFrom":subQ0,"instanceName":"1"})]})});}
            var Q8;
            {var subQ0=makeQuery(id+"F5.opPattern","COPY",FACE,{"derivedFrom":makeQuery(id+"F4.opRevolve","SWEPT_FACE",FACE,{"disambiguationData":[OSD([sQuery(id+"F3.wireOp",EDGE,"E19.1")])]}),"instanceName":"1"});Q8=makeQuery(id+"F10.opBoolean","COPY",EDGE,{"derivedFrom":makeQuery(id+"F9.opBoolean","INTERSECT",EDGE,{"disambiguationData":[OD(0.0)],"derivedFrom":[subQ0,makeQuery(id+"F8.opPattern","COPY",FACE,{"derivedFrom":subQ0,"instanceName":"2"})]})});}
            var Q9;
            {var subQ0=makeQuery(id+"F4.opRevolve","SWEPT_FACE",FACE,{"disambiguationData":[OSD([sQuery(id+"F3.wireOp",EDGE,"E19.1")])]});Q9=makeQuery(id+"F10.opBoolean","COPY",EDGE,{"derivedFrom":makeQuery(id+"F9.opBoolean","INTERSECT",EDGE,{"disambiguationData":[OD(1.0)],"derivedFrom":[makeQuery(id+"F8.opPattern","COPY",FACE,{"derivedFrom":subQ0,"instanceName":"1"}),makeQuery(id+"F8.opPattern","COPY",FACE,{"derivedFrom":subQ0,"instanceName":"2"})]})});}
            var Q10;
            {var subQ0=makeQuery(id+"F4.opRevolve","SWEPT_FACE",FACE,{"disambiguationData":[OSD([sQuery(id+"F3.wireOp",EDGE,"E19.1")])]});Q10=makeQuery(id+"F10.opBoolean","COPY",EDGE,{"derivedFrom":makeQuery(id+"F9.opBoolean","INTERSECT",EDGE,{"disambiguationData":[OD(0.0)],"derivedFrom":[makeQuery(id+"F5.opPattern","COPY",FACE,{"derivedFrom":subQ0,"instanceName":"1"}),makeQuery(id+"F8.opPattern","COPY",FACE,{"derivedFrom":subQ0,"instanceName":"2"})]})});}
            var Q11;
            {var subQ0=makeQuery(id+"F4.opRevolve","SWEPT_FACE",FACE,{"disambiguationData":[OSD([sQuery(id+"F3.wireOp",EDGE,"E19.1")])]});Q11=makeQuery(id+"F10.opBoolean","COPY",EDGE,{"derivedFrom":makeQuery(id+"F9.opBoolean","INTERSECT",EDGE,{"disambiguationData":[OD(0.0)],"derivedFrom":[makeQuery(id+"F5.opPattern","COPY",FACE,{"derivedFrom":subQ0,"instanceName":"1"}),makeQuery(id+"F8.opPattern","COPY",FACE,{"derivedFrom":subQ0,"instanceName":"1"})]})});}
            var Q12;
            {var subQ0=makeQuery(id+"F5.opPattern","COPY",FACE,{"derivedFrom":makeQuery(id+"F4.opRevolve","SWEPT_FACE",FACE,{"disambiguationData":[OSD([sQuery(id+"F3.wireOp",EDGE,"E19.1")])]}),"instanceName":"1"});Q12=makeQuery(id+"F10.opBoolean","COPY",EDGE,{"derivedFrom":makeQuery(id+"F9.opBoolean","INTERSECT",EDGE,{"disambiguationData":[OD(1.0)],"derivedFrom":[subQ0,makeQuery(id+"F8.opPattern","COPY",FACE,{"derivedFrom":subQ0,"instanceName":"1"})]})});}
            var Q13;
            {var subQ0=makeQuery(id+"F5.opPattern","COPY",FACE,{"derivedFrom":makeQuery(id+"F4.opRevolve","SWEPT_FACE",FACE,{"disambiguationData":[OSD([sQuery(id+"F3.wireOp",EDGE,"E19.1")])]}),"instanceName":"1"});Q13=makeQuery(id+"F10.opBoolean","COPY",EDGE,{"derivedFrom":makeQuery(id+"F9.opBoolean","INTERSECT",EDGE,{"disambiguationData":[OD(1.0)],"derivedFrom":[subQ0,makeQuery(id+"F8.opPattern","COPY",FACE,{"derivedFrom":subQ0,"instanceName":"2"})]})});}
            var Q14;
            {var subQ0=makeQuery(id+"F5.opPattern","COPY",FACE,{"derivedFrom":makeQuery(id+"F4.opRevolve","SWEPT_FACE",FACE,{"disambiguationData":[OSD([sQuery(id+"F3.wireOp",EDGE,"E19.1")])]}),"instanceName":"1"});Q14=makeQuery(id+"F10.opBoolean","COPY",EDGE,{"derivedFrom":makeQuery(id+"F9.opBoolean","INTERSECT",EDGE,{"disambiguationData":[OD(1.0)],"derivedFrom":[makeQuery(id+"F8.opPattern","COPY",FACE,{"derivedFrom":subQ0,"instanceName":"1"}),makeQuery(id+"F8.opPattern","COPY",FACE,{"derivedFrom":subQ0,"instanceName":"2"})]})});}
            var Q15;
            {var subQ0=makeQuery(id+"F4.opRevolve","SWEPT_FACE",FACE,{"disambiguationData":[OSD([sQuery(id+"F3.wireOp",EDGE,"E19.1")])]});Q15=makeQuery(id+"F10.opBoolean","COPY",EDGE,{"derivedFrom":makeQuery(id+"F9.opBoolean","INTERSECT",EDGE,{"disambiguationData":[OD(1.0)],"derivedFrom":[makeQuery(id+"F5.opPattern","COPY",FACE,{"derivedFrom":subQ0,"instanceName":"1"}),makeQuery(id+"F8.opPattern","COPY",FACE,{"derivedFrom":subQ0,"instanceName":"2"})]})});}
            var Q16;
            {var subQ0=makeQuery(id+"F4.opRevolve","SWEPT_FACE",FACE,{"disambiguationData":[OSD([sQuery(id+"F3.wireOp",EDGE,"E19.1")])]});Q16=makeQuery(id+"F10.opBoolean","COPY",EDGE,{"derivedFrom":makeQuery(id+"F9.opBoolean","INTERSECT",EDGE,{"disambiguationData":[OD(1.0)],"derivedFrom":[makeQuery(id+"F8.opPattern","COPY",FACE,{"derivedFrom":makeQuery(id+"F5.opPattern","COPY",FACE,{"derivedFrom":subQ0,"instanceName":"1"}),"instanceName":"1"}),makeQuery(id+"F8.opPattern","COPY",FACE,{"derivedFrom":subQ0,"instanceName":"2"})]})});}
            var Q17;
            {var subQ0=makeQuery(id+"F5.opPattern","COPY",FACE,{"derivedFrom":makeQuery(id+"F4.opRevolve","SWEPT_FACE",FACE,{"disambiguationData":[OSD([sQuery(id+"F3.wireOp",EDGE,"E19.1")])]}),"instanceName":"1"});Q17=makeQuery(id+"F10.opBoolean","COPY",EDGE,{"derivedFrom":makeQuery(id+"F9.opBoolean","INTERSECT",EDGE,{"disambiguationData":[OD(0.0)],"derivedFrom":[subQ0,makeQuery(id+"F8.opPattern","COPY",FACE,{"derivedFrom":subQ0,"instanceName":"1"})]})});}
            var Q18;
            {var subQ0=makeQuery(id+"F4.opRevolve","SWEPT_FACE",FACE,{"disambiguationData":[OSD([sQuery(id+"F3.wireOp",EDGE,"E19.1")])]});Q18=makeQuery(id+"F10.opBoolean","COPY",EDGE,{"derivedFrom":makeQuery(id+"F9.opBoolean","INTERSECT",EDGE,{"disambiguationData":[OD(1.0)],"derivedFrom":[subQ0,makeQuery(id+"F8.opPattern","COPY",FACE,{"derivedFrom":subQ0,"instanceName":"2"})]})});}
            var Q19;
            {var subQ0=makeQuery(id+"F4.opRevolve","SWEPT_FACE",FACE,{"disambiguationData":[OSD([sQuery(id+"F3.wireOp",EDGE,"E19.1")])]});Q19=makeQuery(id+"F10.opBoolean","COPY",EDGE,{"derivedFrom":makeQuery(id+"F9.opBoolean","INTERSECT",EDGE,{"disambiguationData":[OD(0.0)],"derivedFrom":[subQ0,makeQuery(id+"F8.opPattern","COPY",FACE,{"derivedFrom":makeQuery(id+"F5.opPattern","COPY",FACE,{"derivedFrom":subQ0,"instanceName":"1"}),"instanceName":"1"})]})});}
            var Q20;
            {var subQ0=makeQuery(id+"F4.opRevolve","SWEPT_FACE",FACE,{"disambiguationData":[OSD([sQuery(id+"F3.wireOp",EDGE,"E19.1")])]});Q20=makeQuery(id+"F10.opBoolean","COPY",EDGE,{"derivedFrom":makeQuery(id+"F9.opBoolean","INTERSECT",EDGE,{"disambiguationData":[OD(0.0)],"derivedFrom":[makeQuery(id+"F8.opPattern","COPY",FACE,{"derivedFrom":makeQuery(id+"F5.opPattern","COPY",FACE,{"derivedFrom":subQ0,"instanceName":"1"}),"instanceName":"1"}),makeQuery(id+"F8.opPattern","COPY",FACE,{"derivedFrom":subQ0,"instanceName":"2"})]})});}
            var Q21;
            {var subQ0=makeQuery(id+"F4.opRevolve","SWEPT_FACE",FACE,{"disambiguationData":[OSD([sQuery(id+"F3.wireOp",EDGE,"E19.1")])]});Q21=makeQuery(id+"F10.opBoolean","COPY",EDGE,{"derivedFrom":makeQuery(id+"F9.opBoolean","INTERSECT",EDGE,{"disambiguationData":[OD(1.0)],"derivedFrom":[subQ0,makeQuery(id+"F8.opPattern","COPY",FACE,{"derivedFrom":makeQuery(id+"F5.opPattern","COPY",FACE,{"derivedFrom":subQ0,"instanceName":"1"}),"instanceName":"2"})]})});}
            var Q22;
            {var subQ0=makeQuery(id+"F5.opPattern","COPY",FACE,{"derivedFrom":makeQuery(id+"F4.opRevolve","SWEPT_FACE",FACE,{"disambiguationData":[OSD([sQuery(id+"F3.wireOp",EDGE,"E19.1")])]}),"instanceName":"1"});Q22=makeQuery(id+"F10.opBoolean","COPY",EDGE,{"derivedFrom":makeQuery(id+"F9.opBoolean","INTERSECT",EDGE,{"disambiguationData":[OD(0.0)],"derivedFrom":[makeQuery(id+"F8.opPattern","COPY",FACE,{"derivedFrom":subQ0,"instanceName":"1"}),makeQuery(id+"F8.opPattern","COPY",FACE,{"derivedFrom":subQ0,"instanceName":"2"})]})});}
            var Q23;
            {var subQ0=makeQuery(id+"F4.opRevolve","SWEPT_FACE",FACE,{"disambiguationData":[OSD([sQuery(id+"F3.wireOp",EDGE,"E19.1")])]});Q23=makeQuery(id+"F10.opBoolean","COPY",EDGE,{"derivedFrom":makeQuery(id+"F9.opBoolean","INTERSECT",EDGE,{"disambiguationData":[OD(1.0)],"derivedFrom":[subQ0,makeQuery(id+"F8.opPattern","COPY",FACE,{"derivedFrom":makeQuery(id+"F5.opPattern","COPY",FACE,{"derivedFrom":subQ0,"instanceName":"1"}),"instanceName":"1"})]})});}
            fillet(context, id + "F19", {"entities" : qUnion([Q0, Q1, Q2, Q3, Q4, Q5, Q6, Q7, Q8, Q9, Q10, Q11, Q12, Q13, Q14, Q15, Q16, Q17, Q18, Q19, Q20, Q21, Q22, Q23]), "radius" : .5 * mm, "tangentPropagation" : true, "allowEdgeOverflow" : false});
        }
        {
            var Q0;
            {var subQ0=makeQuery(id+"F4.opRevolve","SWEPT_FACE",FACE,{"disambiguationData":[OSD([sQuery(id+"F3.wireOp",EDGE,"E19.0")])]});Q0=makeQuery(id+"F10.opBoolean","SPLIT",FACE,{"disambiguationData":[TD([subQ0,makeQuery(id+"F8.opPattern","COPY",FACE,{"derivedFrom":subQ0,"instanceName":"1"}),makeQuery(id+"F8.opPattern","COPY",FACE,{"derivedFrom":subQ0,"instanceName":"2"})])],"derivedFrom":makeQuery(id+"F2.opRevolve","SWEPT_FACE",FACE,{"disambiguationData":[OSD([sQuery(id+"F1.wireOp",EDGE,"E3")])]})});}
            var Q1;
            {var subQ0=makeQuery(id+"F4.opRevolve","SWEPT_FACE",FACE,{"disambiguationData":[OSD([sQuery(id+"F3.wireOp",EDGE,"E19.0")])]});Q1=makeQuery(id+"F10.opBoolean","SPLIT",FACE,{"disambiguationData":[TD([subQ0,makeQuery(id+"F8.opPattern","COPY",FACE,{"derivedFrom":makeQuery(id+"F5.opPattern","COPY",FACE,{"derivedFrom":subQ0,"instanceName":"1"}),"instanceName":"1"}),makeQuery(id+"F8.opPattern","COPY",FACE,{"derivedFrom":subQ0,"instanceName":"2"})])],"derivedFrom":makeQuery(id+"F2.opRevolve","SWEPT_FACE",FACE,{"disambiguationData":[OSD([sQuery(id+"F1.wireOp",EDGE,"E3")])]})});}
            var Q2;
            {var subQ0=makeQuery(id+"F4.opRevolve","SWEPT_FACE",FACE,{"disambiguationData":[OSD([sQuery(id+"F3.wireOp",EDGE,"E19.0")])]});var subQ1=makeQuery(id+"F5.opPattern","COPY",FACE,{"derivedFrom":subQ0,"instanceName":"1"});Q2=makeQuery(id+"F10.opBoolean","SPLIT",FACE,{"disambiguationData":[TD([subQ0,makeQuery(id+"F8.opPattern","COPY",FACE,{"derivedFrom":subQ1,"instanceName":"1"}),makeQuery(id+"F8.opPattern","COPY",FACE,{"derivedFrom":subQ1,"instanceName":"2"})])],"derivedFrom":makeQuery(id+"F2.opRevolve","SWEPT_FACE",FACE,{"disambiguationData":[OSD([sQuery(id+"F1.wireOp",EDGE,"E3")])]})});}
            var Q3;
            {var subQ0=makeQuery(id+"F4.opRevolve","SWEPT_FACE",FACE,{"disambiguationData":[OSD([sQuery(id+"F3.wireOp",EDGE,"E19.0")])]});Q3=makeQuery(id+"F10.opBoolean","SPLIT",FACE,{"disambiguationData":[TD([subQ0,makeQuery(id+"F8.opPattern","COPY",FACE,{"derivedFrom":subQ0,"instanceName":"1"}),makeQuery(id+"F8.opPattern","COPY",FACE,{"derivedFrom":makeQuery(id+"F5.opPattern","COPY",FACE,{"derivedFrom":subQ0,"instanceName":"1"}),"instanceName":"2"})])],"derivedFrom":makeQuery(id+"F2.opRevolve","SWEPT_FACE",FACE,{"disambiguationData":[OSD([sQuery(id+"F1.wireOp",EDGE,"E3")])]})});}
            var Q4;
            {var subQ0=makeQuery(id+"F4.opRevolve","SWEPT_FACE",FACE,{"disambiguationData":[OSD([sQuery(id+"F3.wireOp",EDGE,"E19.0")])]});var subQ1=makeQuery(id+"F5.opPattern","COPY",FACE,{"derivedFrom":subQ0,"instanceName":"1"});Q4=makeQuery(id+"F10.opBoolean","SPLIT",FACE,{"disambiguationData":[TD([subQ1,makeQuery(id+"F8.opPattern","COPY",FACE,{"derivedFrom":subQ0,"instanceName":"1"}),makeQuery(id+"F8.opPattern","COPY",FACE,{"derivedFrom":subQ1,"instanceName":"2"})])],"derivedFrom":makeQuery(id+"F2.opRevolve","SWEPT_FACE",FACE,{"disambiguationData":[OSD([sQuery(id+"F1.wireOp",EDGE,"E3")])]})});}
            var Q5;
            {var subQ0=makeQuery(id+"F4.opRevolve","SWEPT_FACE",FACE,{"disambiguationData":[OSD([sQuery(id+"F3.wireOp",EDGE,"E19.0")])]});Q5=makeQuery(id+"F10.opBoolean","SPLIT",FACE,{"disambiguationData":[TD([makeQuery(id+"F5.opPattern","COPY",FACE,{"derivedFrom":subQ0,"instanceName":"1"}),makeQuery(id+"F8.opPattern","COPY",FACE,{"derivedFrom":subQ0,"instanceName":"1"}),makeQuery(id+"F8.opPattern","COPY",FACE,{"derivedFrom":subQ0,"instanceName":"2"})])],"derivedFrom":makeQuery(id+"F2.opRevolve","SWEPT_FACE",FACE,{"disambiguationData":[OSD([sQuery(id+"F1.wireOp",EDGE,"E3")])]})});}
            var Q6;
            {var subQ0=makeQuery(id+"F4.opRevolve","SWEPT_FACE",FACE,{"disambiguationData":[OSD([sQuery(id+"F3.wireOp",EDGE,"E19.0")])]});var subQ1=makeQuery(id+"F5.opPattern","COPY",FACE,{"derivedFrom":subQ0,"instanceName":"1"});Q6=makeQuery(id+"F10.opBoolean","SPLIT",FACE,{"disambiguationData":[TD([subQ1,makeQuery(id+"F8.opPattern","COPY",FACE,{"derivedFrom":subQ1,"instanceName":"1"}),makeQuery(id+"F8.opPattern","COPY",FACE,{"derivedFrom":subQ0,"instanceName":"2"})])],"derivedFrom":makeQuery(id+"F2.opRevolve","SWEPT_FACE",FACE,{"disambiguationData":[OSD([sQuery(id+"F1.wireOp",EDGE,"E3")])]})});}
            var Q7;
            {var subQ0=makeQuery(id+"F5.opPattern","COPY",FACE,{"derivedFrom":makeQuery(id+"F4.opRevolve","SWEPT_FACE",FACE,{"disambiguationData":[OSD([sQuery(id+"F3.wireOp",EDGE,"E19.0")])]}),"instanceName":"1"});Q7=makeQuery(id+"F10.opBoolean","SPLIT",FACE,{"disambiguationData":[TD([subQ0,makeQuery(id+"F8.opPattern","COPY",FACE,{"derivedFrom":subQ0,"instanceName":"1"}),makeQuery(id+"F8.opPattern","COPY",FACE,{"derivedFrom":subQ0,"instanceName":"2"})])],"derivedFrom":makeQuery(id+"F2.opRevolve","SWEPT_FACE",FACE,{"disambiguationData":[OSD([sQuery(id+"F1.wireOp",EDGE,"E3")])]})});}
            fillet(context, id + "F20", {"entities" : qUnion([Q0, Q1, Q2, Q3, Q4, Q5, Q6, Q7]), "radius" : .5 * mm, "tangentPropagation" : true, "allowEdgeOverflow" : false});
        }
    });
